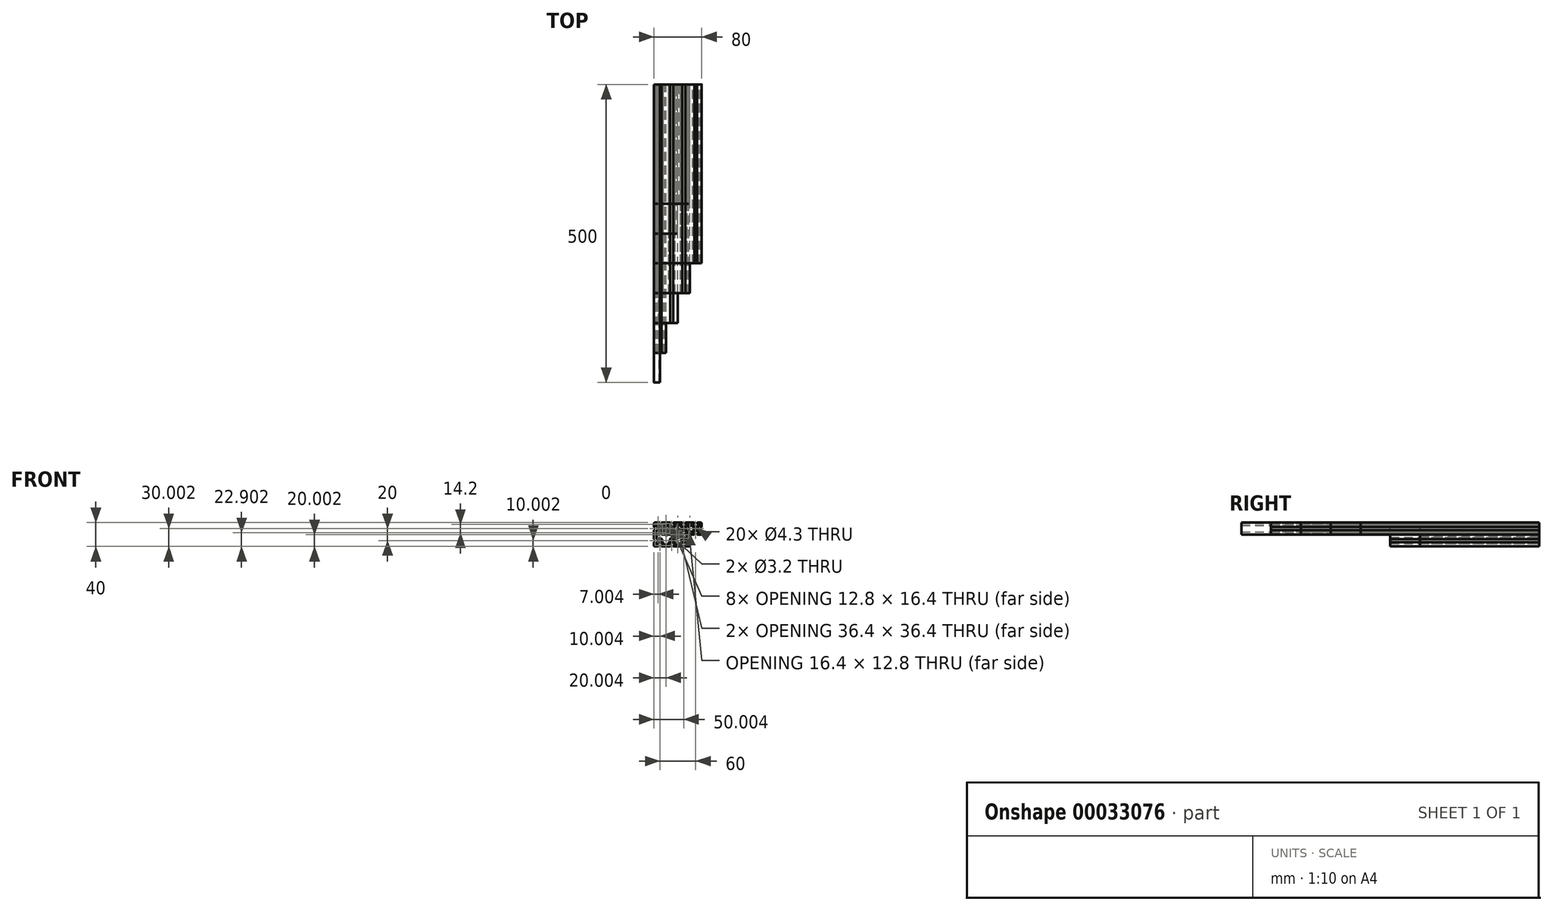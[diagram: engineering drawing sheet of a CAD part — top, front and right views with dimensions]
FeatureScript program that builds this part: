
annotation { "Feature Type Name" : "Feature", "Feature Type Description" : "" }
export const myFeature = defineFeature(function(context is Context, id is Id, definition is map)
    precondition{}
    {
        {
            var Q0;
            Q0=qCreatedBy(makeId("Front.planeOp"),FACE);
            var sketch = newSketch(context, id + "F0", { "sketchPlane" : qUnion([Q0])});
            skLineSegment(sketch, "E0.rect.bottom", {"start": v(-15.75, 9.71) * mm, "end": v(-10.29, 9.71) * mm});
            skLineSegment(sketch, "E0.rect.top", {"start": v(-17.22, -10.29) * mm, "end": v(-3.32, -10.29) * mm});
            skLineSegment(sketch, "E0.rect.left", {"start": v(-17.25, 8.21) * mm, "end": v(-17.25, 3.46) * mm});
            skLineSegment(sketch, "E0.rect.right", {"start": v(2.75, 8.21) * mm, "end": v(2.75, 3.46) * mm});
            skPoint(sketch, "E0.rect.middle", {"position": v(-7.25, -0.29) * mm});
            skCircle(sketch, "E1", {"center": v(-7.25, -0.29) * mm, "radius": 2.15 * mm});
            skPoint(sketch, "E2.visualSharp", {"position": v(-17.25, 9.71) * mm});
            skArc(sketch, "E2.filletArc", {"start": v(-15.75, 9.71) * mm, "mid": v(-16.82, 9.28) * mm, "end": v(-17.25, 8.21) * mm});
            skPoint(sketch, "E3.visualSharp", {"position": v(2.75, 9.71) * mm});
            skArc(sketch, "E3.filletArc", {"start": v(2.75, 8.21) * mm, "mid": v(2.3, 9.28) * mm, "end": v(1.25, 9.71) * mm});
            skPoint(sketch, "E4.visualSharp", {"position": v(2.75, -10.29) * mm});
            skArc(sketch, "E4.filletArc", {"start": v(1.25, -10.29) * mm, "mid": v(2.3, -9.85) * mm, "end": v(2.75, -8.79) * mm});
            skPoint(sketch, "E5.visualSharp", {"position": v(-17.25, -10.29) * mm});
            skArc(sketch, "E5.filletArc", {"start": v(-17.25, -7.29) * mm, "mid": v(-18.72, -8.8) * mm, "end": v(-17.22, -10.29) * mm});
            skLineSegment(sketch, "E6.rect.bottom", {"start": v(-15.7, 2.96) * mm, "end": v(-16.75, 2.96) * mm});
            skLineSegment(sketch, "E6.rect.top", {"start": v(-15.7, -2.04) * mm, "end": v(-16.75, -2.04) * mm});
            skLineSegment(sketch, "E6.rect.left", {"start": v(-10.85, 2.34) * mm, "end": v(-10.85, -2.4) * mm});
            skLineSegment(sketch, "E6.rect.right", {"start": v(-23.65, 2.96) * mm, "end": v(-23.65, -2.04) * mm});
            skPoint(sketch, "E6.rect.middle", {"position": v(-17.25, 0.46) * mm});
            skLineSegment(sketch, "E7.rect.bottom", {"start": v(-9.65, 16.11) * mm, "end": v(-4.65, 16.11) * mm});
            skLineSegment(sketch, "E7.rect.top", {"start": v(-9.24, 3.31) * mm, "end": v(-6.36, 3.31) * mm});
            skLineSegment(sketch, "E7.rect.left", {"start": v(-9.79, 9.21) * mm, "end": v(-9.79, 8.16) * mm});
            skLineSegment(sketch, "E7.rect.right", {"start": v(-4.65, 9.21) * mm, "end": v(-4.65, 8.16) * mm});
            skPoint(sketch, "E7.rect.middle", {"position": v(-7.25, 9.71) * mm});
            skLineSegment(sketch, "E8", {"start": v(-17.25, 9.71) * mm, "end": v(2.75, -10.29) * mm, "construction": true});
            skLineSegment(sketch, "E9", {"start": v(4.78, 7.91) * mm, "end": v(-4.79, 7.91) * mm, "construction": true});
            skLineSegment(sketch, "E10", {"start": v(-15.45, 13.5) * mm, "end": v(-15.45, -13.73) * mm, "construction": true});
            skLineSegment(sketch, "E11.0.MirrorCS", {"start": v(0.55, 2.96) * mm, "end": v(2.25, 2.96) * mm});
            skLineSegment(sketch, "E12.0.MirrorCS", {"start": v(0.94, -3.27) * mm, "end": v(2.34, -3.54) * mm});
            skLineSegment(sketch, "E13.0.MirrorCS", {"start": v(-2.06, 3.04) * mm, "end": v(-3.49, -1.5) * mm});
            skLineSegment(sketch, "E14.0.MirrorCS", {"start": v(-0.42, 17.7) * mm, "end": v(0.94, -9.51) * mm, "construction": true});
            skLineSegment(sketch, "E15.0.MirrorCS", {"start": v(-5.3, -9.79) * mm, "end": v(-5.3, -8.34) * mm});
            skLineSegment(sketch, "E16.0.MirrorCS", {"start": v(-3, -9.4) * mm, "end": v(-4.52, -8.14) * mm});
            skLineSegment(sketch, "E17.0.MirrorCS", {"start": v(-9.53, -2.76) * mm, "end": v(-5.93, -2.76) * mm});
            skLineSegment(sketch, "E18.0.MirrorCS", {"start": v(4.78, -8.09) * mm, "end": v(-18.65, -8.09) * mm, "construction": true});
            skLineSegment(sketch, "E19.0.MirrorCS", {"start": v(-6.64, -13.3) * mm, "end": v(-6.64, 14.98) * mm, "construction": true});
            skLineSegment(sketch, "E20", {"start": v(-10.3, 3.75) * mm, "end": v(-12.58, 6.04) * mm});
            skLineSegment(sketch, "E21", {"start": v(-11.3, 3.4) * mm, "end": v(-13.58, 5.69) * mm});
            skLineSegment(sketch, "E22", {"start": v(-10.85, -2.4) * mm, "end": v(-10.85, -7.57) * mm});
            skLineSegment(sketch, "E23", {"start": v(-11.03, -4.26) * mm, "end": v(-11.03, -6.99) * mm});
            skLineSegment(sketch, "E24", {"start": v(-4.87, -3.2) * mm, "end": v(-1.86, -6.2) * mm});
            skLineSegment(sketch, "E25", {"start": v(-3.12, -3) * mm, "end": v(-1.2, -4.92) * mm});
            skLineSegment(sketch, "E26", {"start": v(-2.13, 2.59) * mm, "end": v(-2.13, 7.9) * mm});
            skLineSegment(sketch, "E27", {"start": v(-4.86, 4.81) * mm, "end": v(-4.86, 6.81) * mm});
            skLineSegment(sketch, "E28", {"start": v(-4.4, 7.91) * mm, "end": v(-5.96, 7.91) * mm});
            skLineSegment(sketch, "E29", {"start": v(-10.04, 7.91) * mm, "end": v(-11.8, 7.91) * mm});
            skLineSegment(sketch, "E30", {"start": v(-15.45, 4.9) * mm, "end": v(-15.45, 3.21) * mm});
            skLineSegment(sketch, "E31", {"start": v(-15.45, -2.29) * mm, "end": v(-15.45, -4.67) * mm});
            skLineSegment(sketch, "E32", {"start": v(-9.93, -8.09) * mm, "end": v(-4.68, -8.09) * mm});
            skLineSegment(sketch, "E33", {"start": v(-5.06, -8.09) * mm, "end": v(-2.63, -8.09) * mm});
            skLineSegment(sketch, "E34", {"start": v(0.67, -4.09) * mm, "end": v(0.64, -3.53) * mm});
            skLineSegment(sketch, "E35", {"start": v(0.3, 3.2) * mm, "end": v(0.07, 7.96) * mm});
            skLineSegment(sketch, "E36.trimOffspring", {"start": v(-17.25, -2.54) * mm, "end": v(-17.25, -7.29) * mm});
            skLineSegment(sketch, "E37.trimOffspring", {"start": v(-4.15, 9.71) * mm, "end": v(1.25, 9.71) * mm});
            skLineSegment(sketch, "E38.trimOffspring", {"start": v(2.75, -4.04) * mm, "end": v(2.75, -8.79) * mm});
            skLineSegment(sketch, "E39.trimOffspring", {"start": v(-9.79, 7.91) * mm, "end": v(-18.65, 7.91) * mm, "construction": true});
            skLineSegment(sketch, "E40.trimOffspring", {"start": v(-4.8, -10.29) * mm, "end": v(1.25, -10.29) * mm});
            skPoint(sketch, "E41.0.MirrorCS.end.orphan", {"position": v(-5.3, -15.56) * mm});
            skPoint(sketch, "E41.0.MirrorCS.start.orphan", {"position": v(-2.3, -9.97) * mm});
            skPoint(sketch, "E42.visualSharp", {"position": v(-9.79, 9.71) * mm});
            skArc(sketch, "E42.filletArc", {"start": v(-9.79, 9.21) * mm, "mid": v(-9.93, 9.57) * mm, "end": v(-10.29, 9.71) * mm});
            skPoint(sketch, "E43.visualSharp", {"position": v(-4.65, 9.71) * mm});
            skArc(sketch, "E43.filletArc", {"start": v(-4.15, 9.71) * mm, "mid": v(-4.5, 9.57) * mm, "end": v(-4.65, 9.21) * mm});
            skPoint(sketch, "E44.visualSharp", {"position": v(2.75, 2.96) * mm});
            skArc(sketch, "E44.filletArc", {"start": v(2.25, 2.96) * mm, "mid": v(2.6, 3.11) * mm, "end": v(2.75, 3.46) * mm});
            skPoint(sketch, "E45.visualSharp", {"position": v(2.75, -3.62) * mm});
            skArc(sketch, "E45.filletArc", {"start": v(2.75, -4.04) * mm, "mid": v(2.63, -3.72) * mm, "end": v(2.34, -3.54) * mm});
            skPoint(sketch, "E46.visualSharp", {"position": v(-5.3, -10.29) * mm});
            skArc(sketch, "E46.filletArc", {"start": v(-5.3, -9.79) * mm, "mid": v(-5.16, -10.14) * mm, "end": v(-4.8, -10.29) * mm});
            skPoint(sketch, "E47.visualSharp", {"position": v(-1.93, -10.29) * mm});
            skArc(sketch, "E47.filletArc", {"start": v(-3.32, -10.29) * mm, "mid": v(-2.85, -9.95) * mm, "end": v(-3, -9.4) * mm});
            skPoint(sketch, "E48.visualSharp", {"position": v(-17.25, -2.04) * mm});
            skArc(sketch, "E48.filletArc", {"start": v(-16.75, -2.04) * mm, "mid": v(-17.1, -2.18) * mm, "end": v(-17.25, -2.54) * mm});
            skPoint(sketch, "E49.visualSharp", {"position": v(-17.25, 2.96) * mm});
            skArc(sketch, "E49.filletArc", {"start": v(-17.25, 3.46) * mm, "mid": v(-17.1, 3.11) * mm, "end": v(-16.75, 2.96) * mm});
            skPoint(sketch, "E50.visualSharp", {"position": v(-9.79, 7.91) * mm});
            skArc(sketch, "E50.filletArc", {"start": v(-10.04, 7.91) * mm, "mid": v(-9.86, 7.99) * mm, "end": v(-9.79, 8.16) * mm});
            skPoint(sketch, "E51.visualSharp", {"position": v(-4.79, 7.91) * mm});
            skArc(sketch, "E51.filletArc", {"start": v(-4.65, 8.16) * mm, "mid": v(-4.58, 7.99) * mm, "end": v(-4.4, 7.91) * mm});
            skPoint(sketch, "E52.visualSharp", {"position": v(0.32, 2.96) * mm});
            skArc(sketch, "E52.filletArc", {"start": v(0.3, 3.2) * mm, "mid": v(0.38, 3.03) * mm, "end": v(0.55, 2.96) * mm});
            skPoint(sketch, "E53.visualSharp", {"position": v(0.63, -3.21) * mm});
            skArc(sketch, "E53.filletArc", {"start": v(0.94, -3.27) * mm, "mid": v(0.73, -3.33) * mm, "end": v(0.64, -3.53) * mm});
            skPoint(sketch, "E54.visualSharp", {"position": v(-5.3, -8.09) * mm});
            skArc(sketch, "E54.filletArc", {"start": v(-5.06, -8.09) * mm, "mid": v(-5.24, -8.16) * mm, "end": v(-5.3, -8.34) * mm});
            skPoint(sketch, "E55.visualSharp", {"position": v(-4.59, -8.09) * mm});
            skArc(sketch, "E55.filletArc", {"start": v(-4.52, -8.14) * mm, "mid": v(-4.6, -8.1) * mm, "end": v(-4.68, -8.09) * mm});
            skPoint(sketch, "E56.visualSharp", {"position": v(-15.45, -2.04) * mm});
            skArc(sketch, "E56.filletArc", {"start": v(-15.45, -2.29) * mm, "mid": v(-15.53, -2.1) * mm, "end": v(-15.7, -2.04) * mm});
            skPoint(sketch, "E57.visualSharp", {"position": v(-15.45, 2.96) * mm});
            skArc(sketch, "E57.filletArc", {"start": v(-15.7, 2.96) * mm, "mid": v(-15.53, 3.04) * mm, "end": v(-15.45, 3.21) * mm});
            skPoint(sketch, "E58.visualSharp", {"position": v(-14.46, 7.91) * mm});
            skArc(sketch, "E58.filletArc", {"start": v(-11.8, 7.91) * mm, "mid": v(-12.82, 7.24) * mm, "end": v(-12.58, 6.04) * mm});
            skPoint(sketch, "E59.visualSharp", {"position": v(-4.86, 7.91) * mm});
            skArc(sketch, "E59.filletArc", {"start": v(-4.86, 6.81) * mm, "mid": v(-5.18, 7.6) * mm, "end": v(-5.96, 7.91) * mm});
            skPoint(sketch, "E60.visualSharp", {"position": v(-2.13, 51.68) * mm});
            skArc(sketch, "E60.filletArc", {"start": v(0.07, 7.96) * mm, "mid": v(-1.06, 9) * mm, "end": v(-2.13, 7.9) * mm});
            skPoint(sketch, "E61.visualSharp", {"position": v(0.81, -6.94) * mm});
            skArc(sketch, "E61.filletArc", {"start": v(-1.2, -4.92) * mm, "mid": v(0.02, -5.15) * mm, "end": v(0.67, -4.09) * mm});
            skPoint(sketch, "E62.visualSharp", {"position": v(0.02, -8.09) * mm});
            skArc(sketch, "E62.filletArc", {"start": v(-2.63, -8.09) * mm, "mid": v(-1.62, -7.4) * mm, "end": v(-1.86, -6.2) * mm});
            skPoint(sketch, "E63.visualSharp", {"position": v(-11.03, -8.09) * mm});
            skArc(sketch, "E63.filletArc", {"start": v(-11.03, -6.99) * mm, "mid": v(-10.7, -7.76) * mm, "end": v(-9.93, -8.09) * mm});
            skPoint(sketch, "E64.visualSharp", {"position": v(-15.45, -40569314724.49) * mm});
            skArc(sketch, "E64.filletArc", {"start": v(-15.45, -21166598987.53) * mm, "mid": v(-14.35, -21166598988.63) * mm, "end": v(-13.25, -21166598987.53) * mm});
            skPoint(sketch, "E65.visualSharp", {"position": v(-15.45, 7.56) * mm});
            skArc(sketch, "E65.filletArc", {"start": v(-13.58, 5.69) * mm, "mid": v(-14.78, 5.93) * mm, "end": v(-15.45, 4.9) * mm});
            skPoint(sketch, "E66.visualSharp", {"position": v(-9.86, 3.31) * mm});
            skArc(sketch, "E66.filletArc", {"start": v(-10.3, 3.75) * mm, "mid": v(-9.81, 3.43) * mm, "end": v(-9.24, 3.31) * mm});
            skPoint(sketch, "E67.visualSharp", {"position": v(-4.86, 3.31) * mm});
            skArc(sketch, "E67.filletArc", {"start": v(-6.36, 3.31) * mm, "mid": v(-5.3, 3.75) * mm, "end": v(-4.86, 4.81) * mm});
            skPoint(sketch, "E68.visualSharp", {"position": v(-2.09, 2.96) * mm});
            skArc(sketch, "E68.filletArc", {"start": v(-2.13, 2.59) * mm, "mid": v(0.85, 2.36) * mm, "end": v(-2.06, 3.04) * mm});
            skPoint(sketch, "E69.visualSharp", {"position": v(-3.76, -2.36) * mm});
            skArc(sketch, "E69.filletArc", {"start": v(-3.49, -1.5) * mm, "mid": v(-3.51, -2.3) * mm, "end": v(-3.12, -3) * mm});
            skPoint(sketch, "E70.visualSharp", {"position": v(-10.85, -2.04) * mm});
            skLineSegment(sketch, "E70.filletArc", {"start": v(-10.85, -2.4) * mm, "end": v(-10.85, -2.4) * mm});
            skPoint(sketch, "E71.visualSharp", {"position": v(-10.85, 2.96) * mm});
            skArc(sketch, "E71.filletArc", {"start": v(-10.85, 2.34) * mm, "mid": v(-10.97, 2.92) * mm, "end": v(-11.3, 3.4) * mm});
            skPoint(sketch, "E72.visualSharp", {"position": v(-11.03, -2.76) * mm});
            skArc(sketch, "E72.filletArc", {"start": v(-9.53, -2.76) * mm, "mid": v(-10.6, -3.2) * mm, "end": v(-11.03, -4.26) * mm});
            skPoint(sketch, "E73.visualSharp", {"position": v(-5.3, -2.76) * mm});
            skArc(sketch, "E73.filletArc", {"start": v(-4.87, -3.2) * mm, "mid": v(-5.36, -2.87) * mm, "end": v(-5.93, -2.76) * mm});
            skLineSegment(sketch, "E74", {"start": v(-15.75, 9.71) * mm, "end": v(-8.79, 9.71) * mm});
            skLineSegment(sketch, "E75.0.MirrorCS", {"start": v(-17.22, -10.29) * mm, "end": v(-8.79, -10.29) * mm});
            skLineSegment(sketch, "E76", {"start": v(-7.29, 8.21) * mm, "end": v(-7.29, -8.79) * mm});
            skPoint(sketch, "E77.visualSharp", {"position": v(-7.29, 9.71) * mm});
            skArc(sketch, "E77.filletArc", {"start": v(-7.29, 8.21) * mm, "mid": v(-7.73, 9.28) * mm, "end": v(-8.79, 9.71) * mm});
            skPoint(sketch, "E78.visualSharp", {"position": v(-7.29, -10.29) * mm});
            skArc(sketch, "E78.filletArc", {"start": v(-8.79, -10.29) * mm, "mid": v(-7.73, -9.85) * mm, "end": v(-7.29, -8.79) * mm});
            skLineSegment(sketch, "E79", {"start": v(-15.45, 7.56) * mm, "end": v(-2.13, 51.68) * mm, "construction": true});
            skLineSegment(sketch, "E80", {"start": v(-7.32, -20284657370.7) * mm, "end": v(0.81, -6.94) * mm, "construction": true});
            skLineSegment(sketch, "E81", {"start": v(-10.29, 9.21) * mm, "end": v(-3.32, -9.79) * mm, "construction": true});
            skCircle(sketch, "E82", {"center": v(-12.85, 16.2) * mm, "radius": 1.6 * mm});
            skCircle(sketch, "E83", {"center": v(0.81, -21.05) * mm, "radius": 1.6 * mm});
            skLineSegment(sketch, "E84", {"start": v(2.75, 9.71) * mm, "end": v(2.75, -10.29) * mm, "construction": true});
            skLineSegment(sketch, "E85.0.MirrorCS", {"start": v(9.64, 9.71) * mm, "end": v(4.25, 9.71) * mm});
            skArc(sketch, "E86.0.MirrorCS", {"start": v(9.64, 9.71) * mm, "mid": v(10, 9.57) * mm, "end": v(10.14, 9.21) * mm});
            skLineSegment(sketch, "E87.0.MirrorCS", {"start": v(10.14, 9.21) * mm, "end": v(10.14, 8.16) * mm});
            skArc(sketch, "E88.0.MirrorCS", {"start": v(10.14, 8.16) * mm, "mid": v(10.07, 7.99) * mm, "end": v(9.9, 7.91) * mm});
            skLineSegment(sketch, "E89.0.MirrorCS", {"start": v(9.9, 7.91) * mm, "end": v(11.45, 7.91) * mm});
            skArc(sketch, "E90.0.MirrorCS", {"start": v(10.35, 6.81) * mm, "mid": v(10.67, 7.6) * mm, "end": v(11.45, 7.91) * mm});
            skLineSegment(sketch, "E91.0.MirrorCS", {"start": v(10.35, 4.81) * mm, "end": v(10.35, 6.81) * mm});
            skArc(sketch, "E92.0.MirrorCS", {"start": v(11.85, 3.31) * mm, "mid": v(10.79, 3.75) * mm, "end": v(10.35, 4.81) * mm});
            skLineSegment(sketch, "E93.0.MirrorCS", {"start": v(14.73, 3.31) * mm, "end": v(11.85, 3.31) * mm});
            skArc(sketch, "E94.0.MirrorCS", {"start": v(15.79, 3.75) * mm, "mid": v(15.3, 3.43) * mm, "end": v(14.73, 3.31) * mm});
            skLineSegment(sketch, "E95.0.MirrorCS", {"start": v(15.79, 3.75) * mm, "end": v(18.07, 6.04) * mm});
            skArc(sketch, "E96.0.MirrorCS", {"start": v(17.3, 7.91) * mm, "mid": v(18.31, 7.24) * mm, "end": v(18.07, 6.04) * mm});
            skLineSegment(sketch, "E97.0.MirrorCS", {"start": v(15.53, 7.91) * mm, "end": v(17.3, 7.91) * mm});
            skArc(sketch, "E98.0.MirrorCS", {"start": v(15.53, 7.91) * mm, "mid": v(15.35, 7.99) * mm, "end": v(15.28, 8.16) * mm});
            skLineSegment(sketch, "E99.0.MirrorCS", {"start": v(15.28, 9.21) * mm, "end": v(15.28, 8.16) * mm});
            skArc(sketch, "E100.0.MirrorCS", {"start": v(15.28, 9.21) * mm, "mid": v(15.42, 9.57) * mm, "end": v(15.78, 9.71) * mm});
            skLineSegment(sketch, "E101.0.MirrorCS", {"start": v(21.25, 9.71) * mm, "end": v(15.78, 9.71) * mm});
            skArc(sketch, "E102.0.MirrorCS", {"start": v(21.25, 9.71) * mm, "mid": v(22.3, 9.28) * mm, "end": v(22.75, 8.21) * mm});
            skLineSegment(sketch, "E103.0.MirrorCS", {"start": v(22.75, 8.21) * mm, "end": v(22.75, 3.46) * mm});
            skArc(sketch, "E104.0.MirrorCS", {"start": v(22.75, 3.46) * mm, "mid": v(22.6, 3.11) * mm, "end": v(22.25, 2.96) * mm});
            skLineSegment(sketch, "E105.0.MirrorCS", {"start": v(21.2, 2.96) * mm, "end": v(22.25, 2.96) * mm});
            skArc(sketch, "E106.0.MirrorCS", {"start": v(21.2, 2.96) * mm, "mid": v(21.02, 3.04) * mm, "end": v(20.95, 3.21) * mm});
            skLineSegment(sketch, "E107.0.MirrorCS", {"start": v(20.95, 4.9) * mm, "end": v(20.95, 3.21) * mm});
            skArc(sketch, "E108.0.MirrorCS", {"start": v(19.07, 5.69) * mm, "mid": v(20.27, 5.93) * mm, "end": v(20.95, 4.9) * mm});
            skLineSegment(sketch, "E109.0.MirrorCS", {"start": v(16.78, 3.4) * mm, "end": v(19.07, 5.69) * mm});
            skArc(sketch, "E110.0.MirrorCS", {"start": v(16.35, 2.34) * mm, "mid": v(16.46, 2.92) * mm, "end": v(16.78, 3.4) * mm});
            skLineSegment(sketch, "E111.0.MirrorCS", {"start": v(16.35, 2.34) * mm, "end": v(16.35, -2.4) * mm});
            skLineSegment(sketch, "E112.0.MirrorCS", {"start": v(16.35, -2.4) * mm, "end": v(16.35, -2.4) * mm});
            skLineSegment(sketch, "E113.0.MirrorCS", {"start": v(16.35, -2.4) * mm, "end": v(16.35, -4.7) * mm});
            skArc(sketch, "E114.0.MirrorCS", {"start": v(20.95, -21166598987.53) * mm, "mid": v(19.85, -21166598988.63) * mm, "end": v(18.75, -21166598987.53) * mm});
            skLineSegment(sketch, "E115.0.MirrorCS", {"start": v(20.95, -2.29) * mm, "end": v(20.95, -4.67) * mm});
            skArc(sketch, "E116.0.MirrorCS", {"start": v(20.95, -2.29) * mm, "mid": v(21.02, -2.1) * mm, "end": v(21.2, -2.04) * mm});
            skLineSegment(sketch, "E117.0.MirrorCS", {"start": v(21.2, -2.04) * mm, "end": v(22.25, -2.04) * mm});
            skArc(sketch, "E118.0.MirrorCS", {"start": v(22.25, -2.04) * mm, "mid": v(22.6, -2.18) * mm, "end": v(22.75, -2.54) * mm});
            skLineSegment(sketch, "E119.0.MirrorCS", {"start": v(22.75, -2.54) * mm, "end": v(22.75, -7.29) * mm});
            skArc(sketch, "E120.0.MirrorCS", {"start": v(22.75, -7.29) * mm, "mid": v(24.2, -8.8) * mm, "end": v(22.7, -10.29) * mm});
            skLineSegment(sketch, "E121.0.MirrorCS", {"start": v(22.7, -10.29) * mm, "end": v(8.8, -10.29) * mm});
            skArc(sketch, "E122.0.MirrorCS", {"start": v(8.8, -10.29) * mm, "mid": v(8.34, -9.95) * mm, "end": v(8.49, -9.4) * mm});
            skLineSegment(sketch, "E123.0.MirrorCS", {"start": v(8.49, -9.4) * mm, "end": v(10, -8.14) * mm});
            skArc(sketch, "E124.0.MirrorCS", {"start": v(10, -8.14) * mm, "mid": v(10.08, -8.1) * mm, "end": v(10.17, -8.09) * mm});
            skLineSegment(sketch, "E125.0.MirrorCS", {"start": v(15.42, -8.09) * mm, "end": v(10.17, -8.09) * mm});
            skArc(sketch, "E126.0.MirrorCS", {"start": v(16.52, -6.99) * mm, "mid": v(16.2, -7.76) * mm, "end": v(15.42, -8.09) * mm});
            skLineSegment(sketch, "E127.0.MirrorCS", {"start": v(16.52, -4.26) * mm, "end": v(16.52, -6.99) * mm});
            skArc(sketch, "E128.0.MirrorCS", {"start": v(15.02, -2.76) * mm, "mid": v(16.08, -3.2) * mm, "end": v(16.52, -4.26) * mm});
            skLineSegment(sketch, "E129.0.MirrorCS", {"start": v(15.02, -2.76) * mm, "end": v(11.42, -2.76) * mm});
            skArc(sketch, "E130.0.MirrorCS", {"start": v(10.36, -3.2) * mm, "mid": v(10.85, -2.87) * mm, "end": v(11.42, -2.76) * mm});
            skLineSegment(sketch, "E131.0.MirrorCS", {"start": v(10.36, -3.2) * mm, "end": v(7.35, -6.2) * mm});
            skArc(sketch, "E132.0.MirrorCS", {"start": v(8.12, -8.09) * mm, "mid": v(7.1, -7.4) * mm, "end": v(7.35, -6.2) * mm});
            skLineSegment(sketch, "E133.0.MirrorCS", {"start": v(10.55, -8.09) * mm, "end": v(8.12, -8.09) * mm});
            skArc(sketch, "E134.0.MirrorCS", {"start": v(10.55, -8.09) * mm, "mid": v(10.73, -8.16) * mm, "end": v(10.8, -8.34) * mm});
            skLineSegment(sketch, "E135.0.MirrorCS", {"start": v(10.8, -9.79) * mm, "end": v(10.8, -8.34) * mm});
            skArc(sketch, "E136.0.MirrorCS", {"start": v(10.8, -9.79) * mm, "mid": v(10.65, -10.14) * mm, "end": v(10.3, -10.29) * mm});
            skLineSegment(sketch, "E137.0.MirrorCS", {"start": v(10.3, -10.29) * mm, "end": v(4.25, -10.29) * mm});
            skCircle(sketch, "E138.0.MirrorC", {"center": v(12.75, -0.29) * mm, "radius": 2.15 * mm});
            skLineSegment(sketch, "E139.0.MirrorCS", {"start": v(7.55, 3.04) * mm, "end": v(8.98, -1.5) * mm});
            skArc(sketch, "E140.0.MirrorCS", {"start": v(7.62, 2.59) * mm, "mid": v(4.64, 2.36) * mm, "end": v(7.55, 3.04) * mm});
            skArc(sketch, "E141.0.MirrorCS", {"start": v(8.98, -1.5) * mm, "mid": v(9, -2.3) * mm, "end": v(8.6, -3) * mm});
            skLineSegment(sketch, "E142.0.MirrorCS", {"start": v(8.6, -3) * mm, "end": v(6.7, -4.92) * mm});
            skLineSegment(sketch, "E143.0.MirrorCS", {"start": v(7.62, 2.59) * mm, "end": v(7.62, 7.9) * mm});
            skArc(sketch, "E144.0.MirrorCS", {"start": v(5.42, 7.96) * mm, "mid": v(6.55, 9) * mm, "end": v(7.62, 7.9) * mm});
            skArc(sketch, "E145.0.MirrorCS", {"start": v(6.7, -4.92) * mm, "mid": v(5.47, -5.15) * mm, "end": v(4.82, -4.09) * mm});
            skLineSegment(sketch, "E146.0.MirrorCS", {"start": v(5.91, 17.7) * mm, "end": v(4.55, -9.51) * mm, "construction": true});
            skLineSegment(sketch, "E147.0.MirrorCS", {"start": v(20.95, 13.5) * mm, "end": v(20.95, -13.73) * mm, "construction": true});
            skLineSegment(sketch, "E148.0.MirrorCS", {"start": v(0.71, -8.09) * mm, "end": v(24.14, -8.09) * mm, "construction": true});
            skLineSegment(sketch, "E149.0.MirrorCS", {"start": v(15.28, 7.91) * mm, "end": v(24.14, 7.91) * mm, "construction": true});
            skLineSegment(sketch, "E150.0.MirrorCS", {"start": v(0.71, 7.91) * mm, "end": v(10.28, 7.91) * mm, "construction": true});
            skPoint(sketch, "E151.orphan", {"position": v(14.28, 9.71) * mm});
            skPoint(sketch, "E152.orphan", {"position": v(14.28, -10.29) * mm});
            skLineSegment(sketch, "E153", {"start": v(4.25, 9.71) * mm, "end": v(1.25, 9.71) * mm});
            skLineSegment(sketch, "E154", {"start": v(4.25, -10.29) * mm, "end": v(1.25, -10.29) * mm});
            skLineSegment(sketch, "E155", {"start": v(-2.13, 6.41) * mm, "end": v(-2.13, 7.9) * mm});
            skLineSegment(sketch, "E156", {"start": v(7.62, 6.41) * mm, "end": v(7.62, 7.9) * mm});
            skLineSegment(sketch, "E157", {"start": v(6.12, 7.91) * mm, "end": v(-0.63, 7.91) * mm});
            skLineSegment(sketch, "E158", {"start": v(-1.2, -4.92) * mm, "end": v(1.52, -7.65) * mm});
            skLineSegment(sketch, "E159", {"start": v(6.7, -4.92) * mm, "end": v(3.97, -7.65) * mm});
            skLineSegment(sketch, "E160", {"start": v(2.9, -8.09) * mm, "end": v(2.58, -8.09) * mm});
            skPoint(sketch, "E161.visualSharp", {"position": v(-2.13, 7.91) * mm});
            skArc(sketch, "E161.filletArc", {"start": v(-0.63, 7.91) * mm, "mid": v(-1.7, 7.48) * mm, "end": v(-2.13, 6.41) * mm});
            skPoint(sketch, "E162.visualSharp", {"position": v(7.62, 7.91) * mm});
            skArc(sketch, "E162.filletArc", {"start": v(7.62, 6.41) * mm, "mid": v(7.18, 7.48) * mm, "end": v(6.12, 7.91) * mm});
            skPoint(sketch, "E163.visualSharp", {"position": v(3.53, -8.09) * mm});
            skArc(sketch, "E163.filletArc", {"start": v(2.9, -8.09) * mm, "mid": v(3.48, -7.97) * mm, "end": v(3.97, -7.65) * mm});
            skPoint(sketch, "E164.visualSharp", {"position": v(1.96, -8.09) * mm});
            skArc(sketch, "E164.filletArc", {"start": v(1.52, -7.65) * mm, "mid": v(2, -7.97) * mm, "end": v(2.58, -8.09) * mm});
            skSolve(sketch);
        }
        {
            var Q0;
            Q0=qCreatedBy(makeId("Front.planeOp"),FACE);
            var sketch = newSketch(context, id + "F1", { "sketchPlane" : qUnion([Q0])});
            skLineSegment(sketch, "E165.0", {"start": v(-17.29, 8.5) * mm, "end": v(-17.29, 3) * mm});
            skArc(sketch, "E166.0", {"start": v(-15.79, 10) * mm, "mid": v(-16.85, 9.56) * mm, "end": v(-17.29, 8.5) * mm});
            skArc(sketch, "E167.0", {"start": v(-7.29, 8.5) * mm, "mid": v(-7.73, 9.56) * mm, "end": v(-8.79, 10) * mm});
            skLineSegment(sketch, "E168.0", {"start": v(-7.29, 8.5) * mm, "end": v(-7.29, -8.5) * mm});
            skArc(sketch, "E169.0", {"start": v(-8.79, -10) * mm, "mid": v(-7.73, -9.56) * mm, "end": v(-7.29, -8.5) * mm});
            skArc(sketch, "E170.0", {"start": v(-17.29, -8.5) * mm, "mid": v(-16.85, -9.56) * mm, "end": v(-15.79, -10) * mm});
            skLineSegment(sketch, "E171.0", {"start": v(-17.29, -3) * mm, "end": v(-17.29, -8.5) * mm});
            skArc(sketch, "E172.0", {"start": v(-17.29, 3) * mm, "mid": v(-17.14, 2.65) * mm, "end": v(-16.79, 2.5) * mm});
            skArc(sketch, "E173.0", {"start": v(-16.79, -2.5) * mm, "mid": v(-17.14, -2.64) * mm, "end": v(-17.29, -3) * mm});
            skLineSegment(sketch, "E174.0", {"start": v(-15.74, -2.5) * mm, "end": v(-16.79, -2.5) * mm});
            skLineSegment(sketch, "E175.0", {"start": v(-15.74, 2.5) * mm, "end": v(-16.79, 2.5) * mm});
            skArc(sketch, "E176.0", {"start": v(-15.74, 2.5) * mm, "mid": v(-15.56, 2.58) * mm, "end": v(-15.49, 2.75) * mm});
            skArc(sketch, "E177.0", {"start": v(-15.49, -2.75) * mm, "mid": v(-15.56, -2.57) * mm, "end": v(-15.74, -2.5) * mm});
            skLineSegment(sketch, "E178.0", {"start": v(-15.49, -2.75) * mm, "end": v(-15.49, -4.44) * mm});
            skLineSegment(sketch, "E179.0", {"start": v(-15.49, 4.45) * mm, "end": v(-15.49, 2.75) * mm});
            skArc(sketch, "E180.0", {"start": v(-13.6, 5.22) * mm, "mid": v(-14.8, 5.46) * mm, "end": v(-15.49, 4.45) * mm});
            skLineSegment(sketch, "E181.0", {"start": v(-11.33, 2.94) * mm, "end": v(-13.6, 5.22) * mm});
            skArc(sketch, "E182.0", {"start": v(-10.89, 1.88) * mm, "mid": v(-11, 2.45) * mm, "end": v(-11.33, 2.94) * mm});
            skLineSegment(sketch, "E183.0", {"start": v(-10.89, 1.88) * mm, "end": v(-10.89, -1.88) * mm});
            skArc(sketch, "E184.0", {"start": v(-11.33, -2.94) * mm, "mid": v(-11, -2.45) * mm, "end": v(-10.89, -1.88) * mm});
            skLineSegment(sketch, "E185.0", {"start": v(-11.33, -2.94) * mm, "end": v(-13.6, -5.22) * mm});
            skArc(sketch, "E186.0", {"start": v(-15.49, -4.44) * mm, "mid": v(-14.8, -5.46) * mm, "end": v(-13.6, -5.22) * mm});
            skCircle(sketch, "E187.0", {"center": v(-10.29, -7.1) * mm, "radius": 1.6 * mm});
            skCircle(sketch, "E188.0", {"center": v(-10.29, 7.1) * mm, "radius": 1.6 * mm});
            skLineSegment(sketch, "E189", {"start": v(-15.79, 10) * mm, "end": v(-8.79, 10) * mm});
            skLineSegment(sketch, "E190", {"start": v(-15.79, -10) * mm, "end": v(-8.79, -10) * mm});
            skSolve(sketch);
        }
        {
            var Q0;
            Q0=qCreatedBy(makeId("Front.planeOp"),FACE);
            var sketch = newSketch(context, id + "F2", { "sketchPlane" : qUnion([Q0])});
            skArc(sketch, "E191.0", {"start": v(-15.79, 10) * mm, "mid": v(-16.85, 9.56) * mm, "end": v(-17.29, 8.5) * mm});
            skLineSegment(sketch, "E192.0", {"start": v(-17.29, 8.5) * mm, "end": v(-17.29, 3) * mm});
            skArc(sketch, "E193.0", {"start": v(-9.79, 9.5) * mm, "mid": v(-9.93, 9.86) * mm, "end": v(-10.29, 10) * mm});
            skLineSegment(sketch, "E194.0", {"start": v(-9.79, 9.5) * mm, "end": v(-9.79, 8.45) * mm});
            skLineSegment(sketch, "E195.0", {"start": v(-10.04, 8.2) * mm, "end": v(-11.73, 8.2) * mm});
            skArc(sketch, "E196.0", {"start": v(-11.73, 8.2) * mm, "mid": v(-12.75, 7.52) * mm, "end": v(-12.5, 6.32) * mm});
            skLineSegment(sketch, "E197.0", {"start": v(-10.23, 4.04) * mm, "end": v(-12.5, 6.32) * mm});
            skArc(sketch, "E198.0", {"start": v(-10.23, 4.04) * mm, "mid": v(-9.74, 3.72) * mm, "end": v(-9.16, 3.6) * mm});
            skLineSegment(sketch, "E199.0", {"start": v(-9.16, 3.6) * mm, "end": v(-5.4, 3.6) * mm});
            skArc(sketch, "E200.0", {"start": v(-5.4, 3.6) * mm, "mid": v(-4.83, 3.72) * mm, "end": v(-4.35, 4.04) * mm});
            skLineSegment(sketch, "E201.0", {"start": v(-4.35, 4.04) * mm, "end": v(-2.06, 6.32) * mm});
            skArc(sketch, "E202.0", {"start": v(-2.06, 6.32) * mm, "mid": v(-1.83, 7.52) * mm, "end": v(-2.84, 8.2) * mm});
            skLineSegment(sketch, "E203.0", {"start": v(-2.84, 8.2) * mm, "end": v(-4.54, 8.2) * mm});
            skArc(sketch, "E204.0", {"start": v(-4.29, 10) * mm, "mid": v(-4.64, 9.86) * mm, "end": v(-4.79, 9.5) * mm});
            skLineSegment(sketch, "E205.0", {"start": v(-4.29, 10) * mm, "end": v(1.21, 10) * mm});
            skArc(sketch, "E206.0", {"start": v(2.71, 8.5) * mm, "mid": v(2.27, 9.56) * mm, "end": v(1.21, 10) * mm});
            skLineSegment(sketch, "E207.0", {"start": v(2.71, 8.5) * mm, "end": v(2.71, 3) * mm});
            skArc(sketch, "E208.0", {"start": v(2.21, 2.5) * mm, "mid": v(2.57, 2.65) * mm, "end": v(2.71, 3) * mm});
            skLineSegment(sketch, "E209.0", {"start": v(1.16, 2.5) * mm, "end": v(2.21, 2.5) * mm});
            skLineSegment(sketch, "E210.0", {"start": v(-15.79, 10) * mm, "end": v(-10.29, 10) * mm});
            skArc(sketch, "E211.0", {"start": v(-17.29, 3) * mm, "mid": v(-17.14, 2.65) * mm, "end": v(-16.79, 2.5) * mm});
            skLineSegment(sketch, "E212.0", {"start": v(-15.74, 2.5) * mm, "end": v(-16.79, 2.5) * mm});
            skArc(sketch, "E213.0", {"start": v(-15.74, 2.5) * mm, "mid": v(-15.56, 2.58) * mm, "end": v(-15.49, 2.75) * mm});
            skLineSegment(sketch, "E213.1", {"start": v(-15.49, 4.45) * mm, "end": v(-15.49, 2.75) * mm});
            skArc(sketch, "E213.2", {"start": v(-13.6, 5.22) * mm, "mid": v(-14.8, 5.46) * mm, "end": v(-15.49, 4.45) * mm});
            skLineSegment(sketch, "E214.0", {"start": v(-11.33, 2.94) * mm, "end": v(-13.6, 5.22) * mm});
            skArc(sketch, "E215.0", {"start": v(-10.89, 1.88) * mm, "mid": v(-11, 2.45) * mm, "end": v(-11.33, 2.94) * mm});
            skLineSegment(sketch, "E216.0", {"start": v(-10.89, 1.88) * mm, "end": v(-10.89, -1.88) * mm});
            skArc(sketch, "E217.0", {"start": v(-11.33, -2.94) * mm, "mid": v(-11, -2.45) * mm, "end": v(-10.89, -1.88) * mm});
            skLineSegment(sketch, "E218.0", {"start": v(-11.33, -2.94) * mm, "end": v(-13.6, -5.22) * mm});
            skArc(sketch, "E219.0", {"start": v(-15.49, -4.44) * mm, "mid": v(-14.8, -5.46) * mm, "end": v(-13.6, -5.22) * mm});
            skLineSegment(sketch, "E220.0", {"start": v(-15.49, -2.75) * mm, "end": v(-15.49, -4.44) * mm});
            skArc(sketch, "E221.0", {"start": v(-15.49, -2.75) * mm, "mid": v(-15.56, -2.57) * mm, "end": v(-15.74, -2.5) * mm});
            skLineSegment(sketch, "E222.0", {"start": v(-15.74, -2.5) * mm, "end": v(-16.79, -2.5) * mm});
            skArc(sketch, "E223.0", {"start": v(-16.79, -2.5) * mm, "mid": v(-17.14, -2.64) * mm, "end": v(-17.29, -3) * mm});
            skLineSegment(sketch, "E224.0", {"start": v(-17.29, -3) * mm, "end": v(-17.29, -8.5) * mm});
            skArc(sketch, "E225.0", {"start": v(-17.29, -8.5) * mm, "mid": v(-16.85, -9.56) * mm, "end": v(-15.79, -10) * mm});
            skLineSegment(sketch, "E226.0", {"start": v(-15.79, -10) * mm, "end": v(-10.29, -10) * mm});
            skArc(sketch, "E227.0", {"start": v(-10.29, -10) * mm, "mid": v(-9.93, -9.85) * mm, "end": v(-9.79, -9.5) * mm});
            skLineSegment(sketch, "E228.0", {"start": v(-9.79, -9.5) * mm, "end": v(-9.79, -8.45) * mm});
            skArc(sketch, "E229.0", {"start": v(-9.79, -8.45) * mm, "mid": v(-9.86, -8.27) * mm, "end": v(-10.04, -8.2) * mm});
            skLineSegment(sketch, "E230.0", {"start": v(-11.73, -8.2) * mm, "end": v(-10.04, -8.2) * mm});
            skArc(sketch, "E231.0", {"start": v(-12.5, -6.32) * mm, "mid": v(-12.75, -7.52) * mm, "end": v(-11.73, -8.2) * mm});
            skLineSegment(sketch, "E232.0", {"start": v(-10.23, -4.04) * mm, "end": v(-12.5, -6.32) * mm});
            skArc(sketch, "E233.0", {"start": v(-9.16, -3.6) * mm, "mid": v(-9.74, -3.71) * mm, "end": v(-10.23, -4.04) * mm});
            skLineSegment(sketch, "E234.0", {"start": v(-9.16, -3.6) * mm, "end": v(-5.4, -3.6) * mm});
            skArc(sketch, "E235.0", {"start": v(-4.35, -4.04) * mm, "mid": v(-4.83, -3.71) * mm, "end": v(-5.4, -3.6) * mm});
            skLineSegment(sketch, "E236.0", {"start": v(-4.35, -4.04) * mm, "end": v(-2.06, -6.32) * mm});
            skArc(sketch, "E237.0", {"start": v(-2.84, -8.2) * mm, "mid": v(-1.83, -7.52) * mm, "end": v(-2.06, -6.32) * mm});
            skLineSegment(sketch, "E238.0", {"start": v(-4.54, -8.2) * mm, "end": v(-2.84, -8.2) * mm});
            skArc(sketch, "E239.0", {"start": v(-4.54, -8.2) * mm, "mid": v(-4.71, -8.27) * mm, "end": v(-4.79, -8.45) * mm});
            skLineSegment(sketch, "E240.0", {"start": v(-4.79, -9.5) * mm, "end": v(-4.79, -8.45) * mm});
            skArc(sketch, "E241.0", {"start": v(-4.79, -9.5) * mm, "mid": v(-4.64, -9.85) * mm, "end": v(-4.29, -10) * mm});
            skLineSegment(sketch, "E242.0", {"start": v(-4.29, -10) * mm, "end": v(1.21, -10) * mm});
            skArc(sketch, "E243.0", {"start": v(1.21, -10) * mm, "mid": v(2.27, -9.56) * mm, "end": v(2.71, -8.5) * mm});
            skLineSegment(sketch, "E244.0", {"start": v(2.71, -3) * mm, "end": v(2.71, -8.5) * mm});
            skArc(sketch, "E245.0", {"start": v(2.71, -3) * mm, "mid": v(2.57, -2.64) * mm, "end": v(2.21, -2.5) * mm});
            skLineSegment(sketch, "E246.0", {"start": v(1.16, -2.5) * mm, "end": v(2.21, -2.5) * mm});
            skArc(sketch, "E247.0", {"start": v(1.16, -2.5) * mm, "mid": v(0.99, -2.57) * mm, "end": v(0.91, -2.75) * mm});
            skLineSegment(sketch, "E248.0", {"start": v(0.91, -4.44) * mm, "end": v(0.91, -2.75) * mm});
            skArc(sketch, "E249.0", {"start": v(-0.96, -5.22) * mm, "mid": v(0.23, -5.46) * mm, "end": v(0.91, -4.44) * mm});
            skLineSegment(sketch, "E250.0", {"start": v(-3.25, -2.94) * mm, "end": v(-0.96, -5.22) * mm});
            skArc(sketch, "E251.0", {"start": v(-3.69, -1.88) * mm, "mid": v(-3.57, -2.45) * mm, "end": v(-3.25, -2.94) * mm});
            skLineSegment(sketch, "E252.0", {"start": v(-3.69, 1.88) * mm, "end": v(-3.69, -1.88) * mm});
            skArc(sketch, "E253.0", {"start": v(-3.25, 2.94) * mm, "mid": v(-3.57, 2.45) * mm, "end": v(-3.69, 1.88) * mm});
            skLineSegment(sketch, "E254.0", {"start": v(-3.25, 2.94) * mm, "end": v(-0.96, 5.22) * mm});
            skArc(sketch, "E255.0", {"start": v(0.91, 4.45) * mm, "mid": v(0.23, 5.46) * mm, "end": v(-0.96, 5.22) * mm});
            skLineSegment(sketch, "E256.0", {"start": v(0.91, 2.75) * mm, "end": v(0.91, 4.45) * mm});
            skArc(sketch, "E257.0", {"start": v(0.91, 2.75) * mm, "mid": v(0.99, 2.58) * mm, "end": v(1.16, 2.5) * mm});
            skLineSegment(sketch, "E258.0", {"start": v(-4.79, 9.5) * mm, "end": v(-4.79, 8.45) * mm});
            skArc(sketch, "E259.0", {"start": v(-4.79, 8.45) * mm, "mid": v(-4.71, 8.28) * mm, "end": v(-4.54, 8.2) * mm});
            skArc(sketch, "E260.0", {"start": v(-10.04, 8.2) * mm, "mid": v(-9.86, 8.28) * mm, "end": v(-9.79, 8.45) * mm});
            skCircle(sketch, "E261.0", {"center": v(-7.29, 0) * mm, "radius": 2.15 * mm});
            skSolve(sketch);
        }
        {
            var Q0;
            Q0=qCreatedBy(makeId("Front.planeOp"),FACE);
            var sketch = newSketch(context, id + "F3", { "sketchPlane" : qUnion([Q0])});
            skArc(sketch, "E262.0", {"start": v(-15.79, 10) * mm, "mid": v(-16.85, 9.56) * mm, "end": v(-17.29, 8.5) * mm});
            skLineSegment(sketch, "E263.0", {"start": v(-15.79, 10) * mm, "end": v(-10.29, 10) * mm});
            skArc(sketch, "E264.0", {"start": v(-9.79, 9.5) * mm, "mid": v(-9.93, 9.86) * mm, "end": v(-10.29, 10) * mm});
            skLineSegment(sketch, "E265.0", {"start": v(-9.79, 9.5) * mm, "end": v(-9.79, 8.45) * mm});
            skArc(sketch, "E266.0", {"start": v(-10.04, 8.2) * mm, "mid": v(-9.86, 8.28) * mm, "end": v(-9.79, 8.45) * mm});
            skLineSegment(sketch, "E267.0", {"start": v(-10.04, 8.2) * mm, "end": v(-11.73, 8.2) * mm});
            skArc(sketch, "E268.0", {"start": v(-11.73, 8.2) * mm, "mid": v(-12.75, 7.52) * mm, "end": v(-12.5, 6.32) * mm});
            skLineSegment(sketch, "E269.0", {"start": v(-10.23, 4.04) * mm, "end": v(-12.5, 6.32) * mm});
            skArc(sketch, "E270.0", {"start": v(-10.23, 4.04) * mm, "mid": v(-9.74, 3.72) * mm, "end": v(-9.16, 3.6) * mm});
            skLineSegment(sketch, "E271.0", {"start": v(-9.16, 3.6) * mm, "end": v(-5.4, 3.6) * mm});
            skArc(sketch, "E272.0", {"start": v(-5.4, 3.6) * mm, "mid": v(-4.83, 3.72) * mm, "end": v(-4.35, 4.04) * mm});
            skLineSegment(sketch, "E273.0", {"start": v(-4.35, 4.04) * mm, "end": v(-2.06, 6.32) * mm});
            skArc(sketch, "E274.0", {"start": v(-2.06, 6.32) * mm, "mid": v(-1.83, 7.52) * mm, "end": v(-2.84, 8.2) * mm});
            skLineSegment(sketch, "E275.0", {"start": v(-2.84, 8.2) * mm, "end": v(-4.54, 8.2) * mm});
            skArc(sketch, "E276.0", {"start": v(-4.79, 8.45) * mm, "mid": v(-4.71, 8.28) * mm, "end": v(-4.54, 8.2) * mm});
            skLineSegment(sketch, "E277.0", {"start": v(-4.79, 9.5) * mm, "end": v(-4.79, 8.45) * mm});
            skArc(sketch, "E278.0", {"start": v(-4.29, 10) * mm, "mid": v(-4.64, 9.86) * mm, "end": v(-4.79, 9.5) * mm});
            skLineSegment(sketch, "E279.0", {"start": v(-17.29, 8.5) * mm, "end": v(-17.29, 3) * mm});
            skArc(sketch, "E280.0", {"start": v(-17.29, 3) * mm, "mid": v(-17.14, 2.65) * mm, "end": v(-16.79, 2.5) * mm});
            skLineSegment(sketch, "E281.0", {"start": v(-15.74, 2.5) * mm, "end": v(-16.79, 2.5) * mm});
            skArc(sketch, "E282.0", {"start": v(-15.74, 2.5) * mm, "mid": v(-15.56, 2.58) * mm, "end": v(-15.49, 2.75) * mm});
            skLineSegment(sketch, "E283.0", {"start": v(-15.49, 4.45) * mm, "end": v(-15.49, 2.75) * mm});
            skArc(sketch, "E284.0", {"start": v(-13.6, 5.22) * mm, "mid": v(-14.8, 5.46) * mm, "end": v(-15.49, 4.45) * mm});
            skLineSegment(sketch, "E285.0", {"start": v(-11.33, 2.94) * mm, "end": v(-13.6, 5.22) * mm});
            skArc(sketch, "E286.0", {"start": v(-10.89, 1.88) * mm, "mid": v(-11, 2.45) * mm, "end": v(-11.33, 2.94) * mm});
            skLineSegment(sketch, "E287.0", {"start": v(-10.89, 1.88) * mm, "end": v(-10.89, -1.88) * mm});
            skArc(sketch, "E288.0", {"start": v(-11.33, -2.94) * mm, "mid": v(-11, -2.45) * mm, "end": v(-10.89, -1.88) * mm});
            skLineSegment(sketch, "E289.0", {"start": v(-11.33, -2.94) * mm, "end": v(-13.6, -5.22) * mm});
            skArc(sketch, "E290.0", {"start": v(-15.49, -4.44) * mm, "mid": v(-14.8, -5.46) * mm, "end": v(-13.6, -5.22) * mm});
            skLineSegment(sketch, "E291.0", {"start": v(-15.49, -2.75) * mm, "end": v(-15.49, -4.44) * mm});
            skArc(sketch, "E292.0", {"start": v(-15.49, -2.75) * mm, "mid": v(-15.56, -2.57) * mm, "end": v(-15.74, -2.5) * mm});
            skLineSegment(sketch, "E293.0", {"start": v(-15.74, -2.5) * mm, "end": v(-16.79, -2.5) * mm});
            skArc(sketch, "E294.0", {"start": v(-16.79, -2.5) * mm, "mid": v(-17.14, -2.64) * mm, "end": v(-17.29, -3) * mm});
            skLineSegment(sketch, "E295.0", {"start": v(-17.29, -3) * mm, "end": v(-17.29, -8.5) * mm});
            skArc(sketch, "E296.0", {"start": v(-17.29, -8.5) * mm, "mid": v(-16.85, -9.56) * mm, "end": v(-15.79, -10) * mm});
            skLineSegment(sketch, "E297.0", {"start": v(-15.79, -10) * mm, "end": v(-10.29, -10) * mm});
            skArc(sketch, "E298.0", {"start": v(-10.29, -10) * mm, "mid": v(-9.93, -9.85) * mm, "end": v(-9.79, -9.5) * mm});
            skLineSegment(sketch, "E299.0", {"start": v(-9.79, -9.5) * mm, "end": v(-9.79, -8.45) * mm});
            skArc(sketch, "E300.0", {"start": v(-9.79, -8.45) * mm, "mid": v(-9.86, -8.27) * mm, "end": v(-10.04, -8.2) * mm});
            skLineSegment(sketch, "E301.0", {"start": v(-11.73, -8.2) * mm, "end": v(-10.04, -8.2) * mm});
            skArc(sketch, "E302.0", {"start": v(-12.5, -6.32) * mm, "mid": v(-12.75, -7.52) * mm, "end": v(-11.73, -8.2) * mm});
            skLineSegment(sketch, "E303.0", {"start": v(-10.23, -4.04) * mm, "end": v(-12.5, -6.32) * mm});
            skArc(sketch, "E304.0", {"start": v(-9.16, -3.6) * mm, "mid": v(-9.74, -3.71) * mm, "end": v(-10.23, -4.04) * mm});
            skLineSegment(sketch, "E305.0", {"start": v(-9.16, -3.6) * mm, "end": v(-5.4, -3.6) * mm});
            skArc(sketch, "E306.0", {"start": v(-4.35, -4.04) * mm, "mid": v(-4.83, -3.71) * mm, "end": v(-5.4, -3.6) * mm});
            skCircle(sketch, "E307.0", {"center": v(-7.29, 0) * mm, "radius": 2.15 * mm});
            skLineSegment(sketch, "E308.0", {"start": v(-4.35, -4.04) * mm, "end": v(-2.06, -6.32) * mm});
            skArc(sketch, "E309.0", {"start": v(-2.84, -8.2) * mm, "mid": v(-1.83, -7.52) * mm, "end": v(-2.06, -6.32) * mm});
            skLineSegment(sketch, "E310.0", {"start": v(-4.54, -8.2) * mm, "end": v(-2.84, -8.2) * mm});
            skArc(sketch, "E311.0", {"start": v(-4.54, -8.2) * mm, "mid": v(-4.71, -8.27) * mm, "end": v(-4.79, -8.45) * mm});
            skLineSegment(sketch, "E312.0", {"start": v(-4.79, -9.5) * mm, "end": v(-4.79, -8.45) * mm});
            skArc(sketch, "E313.0", {"start": v(-4.79, -9.5) * mm, "mid": v(-4.64, -9.85) * mm, "end": v(-4.29, -10) * mm});
            skArc(sketch, "E314.0", {"start": v(-3.25, 2.94) * mm, "mid": v(-3.57, 2.45) * mm, "end": v(-3.69, 1.88) * mm});
            skLineSegment(sketch, "E315.0", {"start": v(-3.69, 1.88) * mm, "end": v(-3.69, -1.88) * mm});
            skArc(sketch, "E316.0", {"start": v(-3.69, -1.88) * mm, "mid": v(-3.57, -2.45) * mm, "end": v(-3.25, -2.94) * mm});
            skArc(sketch, "E317.0", {"start": v(2.64, 8.2) * mm, "mid": v(2.06, 8.09) * mm, "end": v(1.57, 7.76) * mm});
            skArc(sketch, "E318.0", {"start": v(3.85, 7.76) * mm, "mid": v(3.37, 8.09) * mm, "end": v(2.8, 8.2) * mm});
            skArc(sketch, "E319.0", {"start": v(8.67, 2.94) * mm, "mid": v(9, 2.45) * mm, "end": v(9.11, 1.88) * mm});
            skLineSegment(sketch, "E320.0", {"start": v(9.11, 1.88) * mm, "end": v(9.11, -1.88) * mm});
            skArc(sketch, "E321.0", {"start": v(9.11, -1.88) * mm, "mid": v(9, -2.45) * mm, "end": v(8.67, -2.94) * mm});
            skArc(sketch, "E322.0", {"start": v(1.57, -7.76) * mm, "mid": v(2.06, -8.08) * mm, "end": v(2.64, -8.2) * mm});
            skArc(sketch, "E323.0", {"start": v(2.8, -8.2) * mm, "mid": v(3.37, -8.08) * mm, "end": v(3.85, -7.76) * mm});
            skLineSegment(sketch, "E324.0", {"start": v(2.8, -8.2) * mm, "end": v(2.64, -8.2) * mm});
            skLineSegment(sketch, "E325.0", {"start": v(2.8, 8.2) * mm, "end": v(2.64, 8.2) * mm});
            skArc(sketch, "E326.0", {"start": v(9.71, 10) * mm, "mid": v(10.07, 9.86) * mm, "end": v(10.21, 9.5) * mm});
            skLineSegment(sketch, "E327.0", {"start": v(10.21, 9.5) * mm, "end": v(10.21, 8.45) * mm});
            skArc(sketch, "E328.0", {"start": v(10.21, 8.45) * mm, "mid": v(10.14, 8.28) * mm, "end": v(9.96, 8.2) * mm});
            skLineSegment(sketch, "E329.0", {"start": v(8.27, 8.2) * mm, "end": v(9.96, 8.2) * mm});
            skArc(sketch, "E330.0", {"start": v(7.5, 6.32) * mm, "mid": v(7.25, 7.52) * mm, "end": v(8.27, 8.2) * mm});
            skLineSegment(sketch, "E331.0", {"start": v(9.77, 4.04) * mm, "end": v(7.5, 6.32) * mm});
            skArc(sketch, "E332.0", {"start": v(10.84, 3.6) * mm, "mid": v(10.26, 3.72) * mm, "end": v(9.77, 4.04) * mm});
            skLineSegment(sketch, "E333.0", {"start": v(14.6, 3.6) * mm, "end": v(10.84, 3.6) * mm});
            skArc(sketch, "E334.0", {"start": v(15.65, 4.04) * mm, "mid": v(15.17, 3.72) * mm, "end": v(14.6, 3.6) * mm});
            skLineSegment(sketch, "E335.0", {"start": v(15.65, 4.04) * mm, "end": v(17.94, 6.32) * mm});
            skArc(sketch, "E336.0", {"start": v(17.16, 8.2) * mm, "mid": v(18.17, 7.52) * mm, "end": v(17.94, 6.32) * mm});
            skLineSegment(sketch, "E337.0", {"start": v(15.46, 8.2) * mm, "end": v(17.16, 8.2) * mm});
            skArc(sketch, "E338.0", {"start": v(15.46, 8.2) * mm, "mid": v(15.29, 8.28) * mm, "end": v(15.21, 8.45) * mm});
            skLineSegment(sketch, "E339.0", {"start": v(15.21, 9.5) * mm, "end": v(15.21, 8.45) * mm});
            skArc(sketch, "E340.0", {"start": v(15.21, 9.5) * mm, "mid": v(15.36, 9.86) * mm, "end": v(15.71, 10) * mm});
            skLineSegment(sketch, "E341.0", {"start": v(21.21, 10) * mm, "end": v(15.71, 10) * mm});
            skArc(sketch, "E342.0", {"start": v(21.21, 10) * mm, "mid": v(22.27, 9.56) * mm, "end": v(22.71, 8.5) * mm});
            skLineSegment(sketch, "E343.0", {"start": v(22.71, 8.5) * mm, "end": v(22.71, 3) * mm});
            skArc(sketch, "E344.0", {"start": v(22.71, 3) * mm, "mid": v(22.57, 2.65) * mm, "end": v(22.21, 2.5) * mm});
            skLineSegment(sketch, "E345.0", {"start": v(21.16, 2.5) * mm, "end": v(22.21, 2.5) * mm});
            skArc(sketch, "E346.0", {"start": v(21.16, 2.5) * mm, "mid": v(20.99, 2.58) * mm, "end": v(20.91, 2.75) * mm});
            skLineSegment(sketch, "E347.0", {"start": v(20.91, 4.45) * mm, "end": v(20.91, 2.75) * mm});
            skArc(sketch, "E348.0", {"start": v(19.04, 5.22) * mm, "mid": v(20.23, 5.46) * mm, "end": v(20.91, 4.45) * mm});
            skLineSegment(sketch, "E349.0", {"start": v(16.75, 2.94) * mm, "end": v(19.04, 5.22) * mm});
            skArc(sketch, "E350.0", {"start": v(16.31, 1.88) * mm, "mid": v(16.43, 2.45) * mm, "end": v(16.75, 2.94) * mm});
            skLineSegment(sketch, "E351.0", {"start": v(16.31, 1.88) * mm, "end": v(16.31, -1.88) * mm});
            skCircle(sketch, "E352.0", {"center": v(12.71, 0) * mm, "radius": 2.15 * mm});
            skArc(sketch, "E353.0", {"start": v(16.75, -2.94) * mm, "mid": v(16.43, -2.45) * mm, "end": v(16.31, -1.88) * mm});
            skLineSegment(sketch, "E354.0", {"start": v(16.75, -2.94) * mm, "end": v(19.04, -5.22) * mm});
            skArc(sketch, "E355.0", {"start": v(20.91, -4.44) * mm, "mid": v(20.23, -5.46) * mm, "end": v(19.04, -5.22) * mm});
            skLineSegment(sketch, "E356.0", {"start": v(20.91, -2.75) * mm, "end": v(20.91, -4.44) * mm});
            skArc(sketch, "E357.0", {"start": v(20.91, -2.75) * mm, "mid": v(20.99, -2.57) * mm, "end": v(21.16, -2.5) * mm});
            skLineSegment(sketch, "E358.0", {"start": v(21.16, -2.5) * mm, "end": v(22.21, -2.5) * mm});
            skArc(sketch, "E359.0", {"start": v(22.21, -2.5) * mm, "mid": v(22.57, -2.64) * mm, "end": v(22.71, -3) * mm});
            skLineSegment(sketch, "E360.0", {"start": v(22.71, -3) * mm, "end": v(22.71, -8.5) * mm});
            skArc(sketch, "E361.0", {"start": v(22.71, -8.5) * mm, "mid": v(22.27, -9.56) * mm, "end": v(21.21, -10) * mm});
            skLineSegment(sketch, "E362.0", {"start": v(21.21, -10) * mm, "end": v(15.71, -10) * mm});
            skArc(sketch, "E363.0", {"start": v(15.71, -10) * mm, "mid": v(15.36, -9.85) * mm, "end": v(15.21, -9.5) * mm});
            skLineSegment(sketch, "E364.0", {"start": v(15.21, -9.5) * mm, "end": v(15.21, -8.45) * mm});
            skArc(sketch, "E365.0", {"start": v(15.21, -8.45) * mm, "mid": v(15.29, -8.27) * mm, "end": v(15.46, -8.2) * mm});
            skLineSegment(sketch, "E366.0", {"start": v(17.16, -8.2) * mm, "end": v(15.46, -8.2) * mm});
            skArc(sketch, "E367.0", {"start": v(17.94, -6.32) * mm, "mid": v(18.17, -7.52) * mm, "end": v(17.16, -8.2) * mm});
            skLineSegment(sketch, "E368.0", {"start": v(15.65, -4.04) * mm, "end": v(17.94, -6.32) * mm});
            skArc(sketch, "E369.0", {"start": v(14.6, -3.6) * mm, "mid": v(15.17, -3.71) * mm, "end": v(15.65, -4.04) * mm});
            skLineSegment(sketch, "E370.0", {"start": v(14.6, -3.6) * mm, "end": v(10.84, -3.6) * mm});
            skArc(sketch, "E371.0", {"start": v(9.77, -4.04) * mm, "mid": v(10.26, -3.71) * mm, "end": v(10.84, -3.6) * mm});
            skLineSegment(sketch, "E372.0", {"start": v(9.77, -4.04) * mm, "end": v(7.5, -6.32) * mm});
            skArc(sketch, "E373.0", {"start": v(8.27, -8.2) * mm, "mid": v(7.25, -7.52) * mm, "end": v(7.5, -6.32) * mm});
            skLineSegment(sketch, "E374.0", {"start": v(9.96, -8.2) * mm, "end": v(8.27, -8.2) * mm});
            skArc(sketch, "E375.0", {"start": v(9.96, -8.2) * mm, "mid": v(10.14, -8.27) * mm, "end": v(10.21, -8.45) * mm});
            skLineSegment(sketch, "E376.0", {"start": v(10.21, -9.5) * mm, "end": v(10.21, -8.45) * mm});
            skArc(sketch, "E377.0", {"start": v(10.21, -9.5) * mm, "mid": v(10.07, -9.85) * mm, "end": v(9.71, -10) * mm});
            skLineSegment(sketch, "E378", {"start": v(-4.29, 10) * mm, "end": v(9.71, 10) * mm});
            skLineSegment(sketch, "E379", {"start": v(-3.25, 2.94) * mm, "end": v(1.57, 7.76) * mm});
            skLineSegment(sketch, "E380", {"start": v(3.85, 7.76) * mm, "end": v(8.67, 2.94) * mm});
            skLineSegment(sketch, "E381", {"start": v(8.67, -2.94) * mm, "end": v(3.85, -7.76) * mm});
            skLineSegment(sketch, "E382", {"start": v(1.57, -7.76) * mm, "end": v(-3.25, -2.94) * mm});
            skLineSegment(sketch, "E383", {"start": v(-4.29, -10) * mm, "end": v(9.71, -10) * mm});
            skSolve(sketch);
        }
        {
            var Q0;
            Q0=qCreatedBy(makeId("Front.planeOp"),FACE);
            var sketch = newSketch(context, id + "F4", { "sketchPlane" : qUnion([Q0])});
            skLineSegment(sketch, "E384.0.0", {"start": v(-10.29, 10) * mm, "end": v(-15.79, 10) * mm});
            skArc(sketch, "E384.0.1", {"start": v(-15.79, 10) * mm, "mid": v(-16.85, 9.56) * mm, "end": v(-17.29, 8.5) * mm});
            skLineSegment(sketch, "E384.0.2", {"start": v(-17.29, 8.5) * mm, "end": v(-17.29, 3) * mm});
            skArc(sketch, "E384.0.3", {"start": v(-17.29, 3) * mm, "mid": v(-17.14, 2.65) * mm, "end": v(-16.79, 2.5) * mm});
            skLineSegment(sketch, "E384.0.4", {"start": v(-16.79, 2.5) * mm, "end": v(-15.74, 2.5) * mm});
            skArc(sketch, "E384.0.5", {"start": v(-15.74, 2.5) * mm, "mid": v(-15.56, 2.58) * mm, "end": v(-15.49, 2.75) * mm});
            skLineSegment(sketch, "E384.0.6", {"start": v(-15.49, 2.75) * mm, "end": v(-15.49, 4.45) * mm});
            skArc(sketch, "E384.0.7", {"start": v(-15.49, 4.45) * mm, "mid": v(-14.8, 5.46) * mm, "end": v(-13.6, 5.22) * mm});
            skLineSegment(sketch, "E384.0.8", {"start": v(-13.6, 5.22) * mm, "end": v(-11.33, 2.94) * mm});
            skArc(sketch, "E384.0.9", {"start": v(-11.33, 2.94) * mm, "mid": v(-11, 2.45) * mm, "end": v(-10.89, 1.88) * mm});
            skLineSegment(sketch, "E384.0.10", {"start": v(-10.89, 1.88) * mm, "end": v(-10.89, -1.88) * mm});
            skArc(sketch, "E384.0.11", {"start": v(-10.89, -1.88) * mm, "mid": v(-11, -2.45) * mm, "end": v(-11.33, -2.94) * mm});
            skLineSegment(sketch, "E384.0.12", {"start": v(-11.33, -2.94) * mm, "end": v(-13.6, -5.22) * mm});
            skArc(sketch, "E384.0.13", {"start": v(-13.6, -5.22) * mm, "mid": v(-14.8, -5.46) * mm, "end": v(-15.49, -4.44) * mm});
            skLineSegment(sketch, "E384.0.14", {"start": v(-15.49, -4.44) * mm, "end": v(-15.49, -2.75) * mm});
            skArc(sketch, "E384.0.15", {"start": v(-15.49, -2.75) * mm, "mid": v(-15.56, -2.57) * mm, "end": v(-15.74, -2.5) * mm});
            skLineSegment(sketch, "E384.0.16", {"start": v(-15.74, -2.5) * mm, "end": v(-16.79, -2.5) * mm});
            skArc(sketch, "E384.0.17", {"start": v(-16.79, -2.5) * mm, "mid": v(-17.14, -2.64) * mm, "end": v(-17.29, -3) * mm});
            skLineSegment(sketch, "E384.0.18", {"start": v(-17.29, -3) * mm, "end": v(-17.29, -8.5) * mm});
            skArc(sketch, "E384.0.19", {"start": v(-17.29, -8.5) * mm, "mid": v(-16.85, -9.56) * mm, "end": v(-15.79, -10) * mm});
            skLineSegment(sketch, "E384.0.20", {"start": v(-15.79, -10) * mm, "end": v(-10.29, -10) * mm});
            skArc(sketch, "E384.0.21", {"start": v(-10.29, -10) * mm, "mid": v(-9.93, -9.85) * mm, "end": v(-9.79, -9.5) * mm});
            skLineSegment(sketch, "E384.0.22", {"start": v(-9.79, -9.5) * mm, "end": v(-9.79, -8.45) * mm});
            skArc(sketch, "E384.0.23", {"start": v(-9.79, -8.45) * mm, "mid": v(-9.86, -8.27) * mm, "end": v(-10.04, -8.2) * mm});
            skLineSegment(sketch, "E384.0.24", {"start": v(-10.04, -8.2) * mm, "end": v(-11.73, -8.2) * mm});
            skArc(sketch, "E384.0.25", {"start": v(-11.73, -8.2) * mm, "mid": v(-12.75, -7.52) * mm, "end": v(-12.5, -6.32) * mm});
            skLineSegment(sketch, "E384.0.26", {"start": v(-12.5, -6.32) * mm, "end": v(-10.23, -4.04) * mm});
            skArc(sketch, "E384.0.27", {"start": v(-10.23, -4.04) * mm, "mid": v(-9.74, -3.71) * mm, "end": v(-9.16, -3.6) * mm});
            skLineSegment(sketch, "E384.0.28", {"start": v(-9.16, -3.6) * mm, "end": v(-5.4, -3.6) * mm});
            skArc(sketch, "E384.0.29", {"start": v(-5.4, -3.6) * mm, "mid": v(-4.83, -3.71) * mm, "end": v(-4.35, -4.04) * mm});
            skLineSegment(sketch, "E384.0.30", {"start": v(-4.35, -4.04) * mm, "end": v(-2.06, -6.32) * mm});
            skArc(sketch, "E384.0.31", {"start": v(-2.06, -6.32) * mm, "mid": v(-1.83, -7.52) * mm, "end": v(-2.84, -8.2) * mm});
            skLineSegment(sketch, "E384.0.32", {"start": v(-2.84, -8.2) * mm, "end": v(-4.54, -8.2) * mm});
            skArc(sketch, "E384.0.33", {"start": v(-4.54, -8.2) * mm, "mid": v(-4.71, -8.27) * mm, "end": v(-4.79, -8.45) * mm});
            skLineSegment(sketch, "E384.0.34", {"start": v(-4.79, -8.45) * mm, "end": v(-4.79, -9.5) * mm});
            skArc(sketch, "E384.0.35", {"start": v(-4.79, -9.5) * mm, "mid": v(-4.64, -9.85) * mm, "end": v(-4.29, -10) * mm});
            skLineSegment(sketch, "E384.0.36", {"start": v(-4.29, -10) * mm, "end": v(9.71, -10) * mm});
            skArc(sketch, "E384.0.37", {"start": v(9.71, -10) * mm, "mid": v(10.07, -9.85) * mm, "end": v(10.21, -9.5) * mm});
            skLineSegment(sketch, "E384.0.38", {"start": v(10.21, -9.5) * mm, "end": v(10.21, -8.45) * mm});
            skArc(sketch, "E384.0.39", {"start": v(10.21, -8.45) * mm, "mid": v(10.14, -8.27) * mm, "end": v(9.96, -8.2) * mm});
            skLineSegment(sketch, "E384.0.40", {"start": v(9.96, -8.2) * mm, "end": v(8.27, -8.2) * mm});
            skArc(sketch, "E384.0.41", {"start": v(8.27, -8.2) * mm, "mid": v(7.25, -7.52) * mm, "end": v(7.5, -6.32) * mm});
            skLineSegment(sketch, "E384.0.42", {"start": v(7.5, -6.32) * mm, "end": v(9.77, -4.04) * mm});
            skArc(sketch, "E384.0.43", {"start": v(9.77, -4.04) * mm, "mid": v(10.26, -3.71) * mm, "end": v(10.84, -3.6) * mm});
            skLineSegment(sketch, "E384.0.44", {"start": v(10.84, -3.6) * mm, "end": v(14.6, -3.6) * mm});
            skArc(sketch, "E384.0.45", {"start": v(14.6, -3.6) * mm, "mid": v(15.17, -3.71) * mm, "end": v(15.65, -4.04) * mm});
            skLineSegment(sketch, "E384.0.46", {"start": v(15.65, -4.04) * mm, "end": v(17.94, -6.32) * mm});
            skArc(sketch, "E384.0.47", {"start": v(17.94, -6.32) * mm, "mid": v(18.17, -7.52) * mm, "end": v(17.16, -8.2) * mm});
            skLineSegment(sketch, "E384.0.48", {"start": v(17.16, -8.2) * mm, "end": v(15.46, -8.2) * mm});
            skArc(sketch, "E384.0.49", {"start": v(15.46, -8.2) * mm, "mid": v(15.29, -8.27) * mm, "end": v(15.21, -8.45) * mm});
            skLineSegment(sketch, "E384.0.50", {"start": v(15.21, -8.45) * mm, "end": v(15.21, -9.5) * mm});
            skArc(sketch, "E384.0.51", {"start": v(15.21, -9.5) * mm, "mid": v(15.36, -9.85) * mm, "end": v(15.71, -10) * mm});
            skArc(sketch, "E384.0.61", {"start": v(16.75, -2.94) * mm, "mid": v(16.43, -2.45) * mm, "end": v(16.31, -1.88) * mm});
            skLineSegment(sketch, "E384.0.62", {"start": v(16.31, -1.88) * mm, "end": v(16.31, 1.88) * mm});
            skArc(sketch, "E384.0.63", {"start": v(16.31, 1.88) * mm, "mid": v(16.43, 2.45) * mm, "end": v(16.75, 2.94) * mm});
            skArc(sketch, "E384.0.73", {"start": v(15.71, 10) * mm, "mid": v(15.36, 9.86) * mm, "end": v(15.21, 9.5) * mm});
            skLineSegment(sketch, "E384.0.74", {"start": v(15.21, 9.5) * mm, "end": v(15.21, 8.45) * mm});
            skArc(sketch, "E384.0.75", {"start": v(15.21, 8.45) * mm, "mid": v(15.29, 8.28) * mm, "end": v(15.46, 8.2) * mm});
            skLineSegment(sketch, "E384.0.76", {"start": v(15.46, 8.2) * mm, "end": v(17.16, 8.2) * mm});
            skArc(sketch, "E384.0.77", {"start": v(17.16, 8.2) * mm, "mid": v(18.17, 7.52) * mm, "end": v(17.94, 6.32) * mm});
            skLineSegment(sketch, "E384.0.78", {"start": v(17.94, 6.32) * mm, "end": v(15.65, 4.04) * mm});
            skArc(sketch, "E384.0.79", {"start": v(15.65, 4.04) * mm, "mid": v(15.17, 3.72) * mm, "end": v(14.6, 3.6) * mm});
            skLineSegment(sketch, "E384.0.80", {"start": v(14.6, 3.6) * mm, "end": v(10.84, 3.6) * mm});
            skArc(sketch, "E384.0.81", {"start": v(10.84, 3.6) * mm, "mid": v(10.26, 3.72) * mm, "end": v(9.77, 4.04) * mm});
            skLineSegment(sketch, "E384.0.82", {"start": v(9.77, 4.04) * mm, "end": v(7.5, 6.32) * mm});
            skArc(sketch, "E384.0.83", {"start": v(7.5, 6.32) * mm, "mid": v(7.25, 7.52) * mm, "end": v(8.27, 8.2) * mm});
            skLineSegment(sketch, "E384.0.84", {"start": v(8.27, 8.2) * mm, "end": v(9.96, 8.2) * mm});
            skArc(sketch, "E384.0.85", {"start": v(9.96, 8.2) * mm, "mid": v(10.14, 8.28) * mm, "end": v(10.21, 8.45) * mm});
            skLineSegment(sketch, "E384.0.86", {"start": v(10.21, 8.45) * mm, "end": v(10.21, 9.5) * mm});
            skArc(sketch, "E384.0.87", {"start": v(10.21, 9.5) * mm, "mid": v(10.07, 9.86) * mm, "end": v(9.71, 10) * mm});
            skLineSegment(sketch, "E384.0.88", {"start": v(9.71, 10) * mm, "end": v(-4.29, 10) * mm});
            skArc(sketch, "E384.0.89", {"start": v(-4.29, 10) * mm, "mid": v(-4.64, 9.86) * mm, "end": v(-4.79, 9.5) * mm});
            skLineSegment(sketch, "E384.0.90", {"start": v(-4.79, 9.5) * mm, "end": v(-4.79, 8.45) * mm});
            skArc(sketch, "E384.0.91", {"start": v(-4.79, 8.45) * mm, "mid": v(-4.71, 8.28) * mm, "end": v(-4.54, 8.2) * mm});
            skLineSegment(sketch, "E384.0.92", {"start": v(-4.54, 8.2) * mm, "end": v(-2.84, 8.2) * mm});
            skArc(sketch, "E384.0.93", {"start": v(-2.84, 8.2) * mm, "mid": v(-1.83, 7.52) * mm, "end": v(-2.06, 6.32) * mm});
            skLineSegment(sketch, "E384.0.94", {"start": v(-2.06, 6.32) * mm, "end": v(-4.35, 4.04) * mm});
            skArc(sketch, "E384.0.95", {"start": v(-4.35, 4.04) * mm, "mid": v(-4.83, 3.72) * mm, "end": v(-5.4, 3.6) * mm});
            skLineSegment(sketch, "E384.0.96", {"start": v(-5.4, 3.6) * mm, "end": v(-9.16, 3.6) * mm});
            skArc(sketch, "E384.0.97", {"start": v(-9.16, 3.6) * mm, "mid": v(-9.74, 3.72) * mm, "end": v(-10.23, 4.04) * mm});
            skLineSegment(sketch, "E384.0.98", {"start": v(-10.23, 4.04) * mm, "end": v(-12.5, 6.32) * mm});
            skArc(sketch, "E384.0.99", {"start": v(-12.5, 6.32) * mm, "mid": v(-12.75, 7.52) * mm, "end": v(-11.73, 8.2) * mm});
            skLineSegment(sketch, "E384.0.100", {"start": v(-11.73, 8.2) * mm, "end": v(-10.04, 8.2) * mm});
            skArc(sketch, "E384.0.101", {"start": v(-10.04, 8.2) * mm, "mid": v(-9.86, 8.28) * mm, "end": v(-9.79, 8.45) * mm});
            skLineSegment(sketch, "E384.0.102", {"start": v(-9.79, 8.45) * mm, "end": v(-9.79, 9.5) * mm});
            skArc(sketch, "E384.0.103", {"start": v(-9.79, 9.5) * mm, "mid": v(-9.93, 9.86) * mm, "end": v(-10.29, 10) * mm});
            skLineSegment(sketch, "E385.0.0", {"start": v(1.57, 7.76) * mm, "end": v(-3.25, 2.94) * mm});
            skArc(sketch, "E385.0.1", {"start": v(-3.25, 2.94) * mm, "mid": v(-3.57, 2.45) * mm, "end": v(-3.69, 1.88) * mm});
            skLineSegment(sketch, "E385.0.2", {"start": v(-3.69, 1.88) * mm, "end": v(-3.69, -1.88) * mm});
            skArc(sketch, "E385.0.3", {"start": v(-3.69, -1.88) * mm, "mid": v(-3.57, -2.45) * mm, "end": v(-3.25, -2.94) * mm});
            skLineSegment(sketch, "E385.0.4", {"start": v(-3.25, -2.94) * mm, "end": v(1.57, -7.76) * mm});
            skArc(sketch, "E385.0.5", {"start": v(1.57, -7.76) * mm, "mid": v(2.06, -8.08) * mm, "end": v(2.64, -8.2) * mm});
            skLineSegment(sketch, "E385.0.6", {"start": v(2.64, -8.2) * mm, "end": v(2.8, -8.2) * mm});
            skArc(sketch, "E385.0.7", {"start": v(2.8, -8.2) * mm, "mid": v(3.37, -8.08) * mm, "end": v(3.85, -7.76) * mm});
            skLineSegment(sketch, "E385.0.8", {"start": v(3.85, -7.76) * mm, "end": v(8.67, -2.94) * mm});
            skArc(sketch, "E385.0.9", {"start": v(8.67, -2.94) * mm, "mid": v(9, -2.45) * mm, "end": v(9.11, -1.88) * mm});
            skLineSegment(sketch, "E385.0.10", {"start": v(9.11, -1.88) * mm, "end": v(9.11, 1.88) * mm});
            skArc(sketch, "E385.0.11", {"start": v(9.11, 1.88) * mm, "mid": v(9, 2.45) * mm, "end": v(8.67, 2.94) * mm});
            skLineSegment(sketch, "E385.0.12", {"start": v(8.67, 2.94) * mm, "end": v(3.85, 7.76) * mm});
            skArc(sketch, "E385.0.13", {"start": v(3.85, 7.76) * mm, "mid": v(3.37, 8.09) * mm, "end": v(2.8, 8.2) * mm});
            skLineSegment(sketch, "E385.0.14", {"start": v(2.8, 8.2) * mm, "end": v(2.64, 8.2) * mm});
            skArc(sketch, "E385.0.15", {"start": v(2.64, 8.2) * mm, "mid": v(2.06, 8.09) * mm, "end": v(1.57, 7.76) * mm});
            skCircle(sketch, "E386.0", {"center": v(-7.29, 0) * mm, "radius": 2.15 * mm});
            skCircle(sketch, "E387.0", {"center": v(12.71, 0) * mm, "radius": 2.15 * mm});
            skLineSegment(sketch, "E388", {"start": v(12.71, 11.72) * mm, "end": v(12.71, -12.08) * mm, "construction": true});
            skLineSegment(sketch, "E389.0.MirrorCS", {"start": v(16.75, 2.94) * mm, "end": v(21.57, 7.76) * mm});
            skLineSegment(sketch, "E390.0.MirrorCS", {"start": v(21.57, -7.76) * mm, "end": v(16.75, -2.94) * mm});
            skArc(sketch, "E391.0.MirrorCS", {"start": v(22.64, -8.2) * mm, "mid": v(22.06, -8.08) * mm, "end": v(21.57, -7.76) * mm});
            skArc(sketch, "E392.0.MirrorCS", {"start": v(21.57, 7.76) * mm, "mid": v(22.06, 8.09) * mm, "end": v(22.64, 8.2) * mm});
            skLineSegment(sketch, "E393.0.MirrorCS", {"start": v(22.64, 8.2) * mm, "end": v(22.8, 8.2) * mm});
            skArc(sketch, "E394.0.MirrorCS", {"start": v(22.8, 8.2) * mm, "mid": v(23.37, 8.09) * mm, "end": v(23.85, 7.76) * mm});
            skLineSegment(sketch, "E395.0.MirrorCS", {"start": v(23.85, 7.76) * mm, "end": v(28.67, 2.94) * mm});
            skArc(sketch, "E396.0.MirrorCS", {"start": v(28.67, 2.94) * mm, "mid": v(29, 2.45) * mm, "end": v(29.11, 1.88) * mm});
            skLineSegment(sketch, "E397.0.MirrorCS", {"start": v(29.11, 1.88) * mm, "end": v(29.11, -1.88) * mm});
            skArc(sketch, "E398.0.MirrorCS", {"start": v(29.11, -1.88) * mm, "mid": v(29, -2.45) * mm, "end": v(28.67, -2.94) * mm});
            skLineSegment(sketch, "E399.0.MirrorCS", {"start": v(28.67, -2.94) * mm, "end": v(23.85, -7.76) * mm});
            skArc(sketch, "E400.0.MirrorCS", {"start": v(23.85, -7.76) * mm, "mid": v(23.37, -8.08) * mm, "end": v(22.8, -8.2) * mm});
            skLineSegment(sketch, "E401.0.MirrorCS", {"start": v(22.8, -8.2) * mm, "end": v(22.64, -8.2) * mm});
            skLineSegment(sketch, "E402.0.MirrorCS", {"start": v(29.71, -10) * mm, "end": v(15.71, -10) * mm});
            skLineSegment(sketch, "E403.0.MirrorCS", {"start": v(15.71, 10) * mm, "end": v(29.71, 10) * mm});
            skArc(sketch, "E404.0.MirrorCS", {"start": v(29.71, 10) * mm, "mid": v(30.07, 9.86) * mm, "end": v(30.21, 9.5) * mm});
            skLineSegment(sketch, "E405.0.MirrorCS", {"start": v(30.21, 9.5) * mm, "end": v(30.21, 8.45) * mm});
            skArc(sketch, "E406.0.MirrorCS", {"start": v(30.21, 8.45) * mm, "mid": v(30.14, 8.28) * mm, "end": v(29.96, 8.2) * mm});
            skLineSegment(sketch, "E407.0.MirrorCS", {"start": v(29.96, 8.2) * mm, "end": v(28.27, 8.2) * mm});
            skArc(sketch, "E408.0.MirrorCS", {"start": v(28.27, 8.2) * mm, "mid": v(27.25, 7.52) * mm, "end": v(27.5, 6.32) * mm});
            skLineSegment(sketch, "E409.0.MirrorCS", {"start": v(27.5, 6.32) * mm, "end": v(29.77, 4.04) * mm});
            skArc(sketch, "E410.0.MirrorCS", {"start": v(29.77, 4.04) * mm, "mid": v(30.26, 3.72) * mm, "end": v(30.84, 3.6) * mm});
            skLineSegment(sketch, "E411.0.MirrorCS", {"start": v(30.84, 3.6) * mm, "end": v(34.6, 3.6) * mm});
            skArc(sketch, "E412.0.MirrorCS", {"start": v(34.6, 3.6) * mm, "mid": v(35.17, 3.72) * mm, "end": v(35.65, 4.04) * mm});
            skLineSegment(sketch, "E413.0.MirrorCS", {"start": v(35.65, 4.04) * mm, "end": v(37.94, 6.32) * mm});
            skArc(sketch, "E414.0.MirrorCS", {"start": v(37.94, 6.32) * mm, "mid": v(38.17, 7.52) * mm, "end": v(37.16, 8.2) * mm});
            skLineSegment(sketch, "E415.0.MirrorCS", {"start": v(37.16, 8.2) * mm, "end": v(35.46, 8.2) * mm});
            skArc(sketch, "E416.0.MirrorCS", {"start": v(35.46, 8.2) * mm, "mid": v(35.29, 8.28) * mm, "end": v(35.21, 8.45) * mm});
            skLineSegment(sketch, "E417.0.MirrorCS", {"start": v(35.21, 8.45) * mm, "end": v(35.21, 9.5) * mm});
            skArc(sketch, "E418.0.MirrorCS", {"start": v(35.21, 9.5) * mm, "mid": v(35.36, 9.86) * mm, "end": v(35.71, 10) * mm});
            skLineSegment(sketch, "E419.0.MirrorCS", {"start": v(35.71, 10) * mm, "end": v(41.21, 10) * mm});
            skArc(sketch, "E420.0.MirrorCS", {"start": v(41.21, 10) * mm, "mid": v(42.27, 9.56) * mm, "end": v(42.71, 8.5) * mm});
            skLineSegment(sketch, "E421.0.MirrorCS", {"start": v(42.71, 8.5) * mm, "end": v(42.71, 3) * mm});
            skArc(sketch, "E422.0.MirrorCS", {"start": v(42.71, 3) * mm, "mid": v(42.57, 2.65) * mm, "end": v(42.21, 2.5) * mm});
            skLineSegment(sketch, "E423.0.MirrorCS", {"start": v(42.21, 2.5) * mm, "end": v(41.16, 2.5) * mm});
            skArc(sketch, "E424.0.MirrorCS", {"start": v(41.16, 2.5) * mm, "mid": v(40.99, 2.58) * mm, "end": v(40.91, 2.75) * mm});
            skLineSegment(sketch, "E425.0.MirrorCS", {"start": v(40.91, 2.75) * mm, "end": v(40.91, 4.45) * mm});
            skArc(sketch, "E426.0.MirrorCS", {"start": v(40.91, 4.45) * mm, "mid": v(40.23, 5.46) * mm, "end": v(39.04, 5.22) * mm});
            skLineSegment(sketch, "E427.0.MirrorCS", {"start": v(39.04, 5.22) * mm, "end": v(36.75, 2.94) * mm});
            skArc(sketch, "E428.0.MirrorCS", {"start": v(36.75, 2.94) * mm, "mid": v(36.43, 2.45) * mm, "end": v(36.31, 1.88) * mm});
            skLineSegment(sketch, "E429.0.MirrorCS", {"start": v(36.31, 1.88) * mm, "end": v(36.31, -1.88) * mm});
            skArc(sketch, "E430.0.MirrorCS", {"start": v(36.31, -1.88) * mm, "mid": v(36.43, -2.45) * mm, "end": v(36.75, -2.94) * mm});
            skLineSegment(sketch, "E431.0.MirrorCS", {"start": v(36.75, -2.94) * mm, "end": v(39.04, -5.22) * mm});
            skArc(sketch, "E432.0.MirrorCS", {"start": v(39.04, -5.22) * mm, "mid": v(40.23, -5.46) * mm, "end": v(40.91, -4.44) * mm});
            skLineSegment(sketch, "E433.0.MirrorCS", {"start": v(40.91, -4.44) * mm, "end": v(40.91, -2.75) * mm});
            skArc(sketch, "E434.0.MirrorCS", {"start": v(40.91, -2.75) * mm, "mid": v(40.99, -2.57) * mm, "end": v(41.16, -2.5) * mm});
            skLineSegment(sketch, "E435.0.MirrorCS", {"start": v(41.16, -2.5) * mm, "end": v(42.21, -2.5) * mm});
            skArc(sketch, "E436.0.MirrorCS", {"start": v(42.21, -2.5) * mm, "mid": v(42.57, -2.64) * mm, "end": v(42.71, -3) * mm});
            skLineSegment(sketch, "E437.0.MirrorCS", {"start": v(42.71, -3) * mm, "end": v(42.71, -8.5) * mm});
            skArc(sketch, "E438.0.MirrorCS", {"start": v(42.71, -8.5) * mm, "mid": v(42.27, -9.56) * mm, "end": v(41.21, -10) * mm});
            skLineSegment(sketch, "E439.0.MirrorCS", {"start": v(41.21, -10) * mm, "end": v(35.71, -10) * mm});
            skArc(sketch, "E440.0.MirrorCS", {"start": v(35.71, -10) * mm, "mid": v(35.36, -9.85) * mm, "end": v(35.21, -9.5) * mm});
            skLineSegment(sketch, "E441.0.MirrorCS", {"start": v(35.21, -9.5) * mm, "end": v(35.21, -8.45) * mm});
            skArc(sketch, "E442.0.MirrorCS", {"start": v(35.21, -8.45) * mm, "mid": v(35.29, -8.27) * mm, "end": v(35.46, -8.2) * mm});
            skLineSegment(sketch, "E443.0.MirrorCS", {"start": v(35.46, -8.2) * mm, "end": v(37.16, -8.2) * mm});
            skArc(sketch, "E444.0.MirrorCS", {"start": v(37.16, -8.2) * mm, "mid": v(38.17, -7.52) * mm, "end": v(37.94, -6.32) * mm});
            skLineSegment(sketch, "E445.0.MirrorCS", {"start": v(37.94, -6.32) * mm, "end": v(35.65, -4.04) * mm});
            skArc(sketch, "E446.0.MirrorCS", {"start": v(35.65, -4.04) * mm, "mid": v(35.17, -3.71) * mm, "end": v(34.6, -3.6) * mm});
            skLineSegment(sketch, "E447.0.MirrorCS", {"start": v(34.6, -3.6) * mm, "end": v(30.84, -3.6) * mm});
            skArc(sketch, "E448.0.MirrorCS", {"start": v(30.84, -3.6) * mm, "mid": v(30.26, -3.71) * mm, "end": v(29.77, -4.04) * mm});
            skLineSegment(sketch, "E449.0.MirrorCS", {"start": v(29.77, -4.04) * mm, "end": v(27.5, -6.32) * mm});
            skArc(sketch, "E450.0.MirrorCS", {"start": v(27.5, -6.32) * mm, "mid": v(27.25, -7.52) * mm, "end": v(28.27, -8.2) * mm});
            skLineSegment(sketch, "E451.0.MirrorCS", {"start": v(28.27, -8.2) * mm, "end": v(29.96, -8.2) * mm});
            skArc(sketch, "E452.0.MirrorCS", {"start": v(29.96, -8.2) * mm, "mid": v(30.14, -8.27) * mm, "end": v(30.21, -8.45) * mm});
            skLineSegment(sketch, "E453.0.MirrorCS", {"start": v(30.21, -8.45) * mm, "end": v(30.21, -9.5) * mm});
            skArc(sketch, "E454.0.MirrorCS", {"start": v(30.21, -9.5) * mm, "mid": v(30.07, -9.85) * mm, "end": v(29.71, -10) * mm});
            skCircle(sketch, "E455.0.MirrorC", {"center": v(32.71, 0) * mm, "radius": 2.15 * mm});
            skSolve(sketch);
        }
        {
            var Q0;
            Q0=qCreatedBy(makeId("Front.planeOp"),FACE);
            var sketch = newSketch(context, id + "F5", { "sketchPlane" : qUnion([Q0])});
            skLineSegment(sketch, "E456.0.0", {"start": v(-10.29, 10) * mm, "end": v(-15.79, 10) * mm});
            skArc(sketch, "E456.0.1", {"start": v(-15.79, 10) * mm, "mid": v(-16.85, 9.56) * mm, "end": v(-17.29, 8.5) * mm});
            skLineSegment(sketch, "E456.0.2", {"start": v(-17.29, 8.5) * mm, "end": v(-17.29, 3) * mm});
            skArc(sketch, "E456.0.3", {"start": v(-17.29, 3) * mm, "mid": v(-17.14, 2.65) * mm, "end": v(-16.79, 2.5) * mm});
            skLineSegment(sketch, "E456.0.4", {"start": v(-16.79, 2.5) * mm, "end": v(-15.74, 2.5) * mm});
            skArc(sketch, "E456.0.5", {"start": v(-15.74, 2.5) * mm, "mid": v(-15.56, 2.58) * mm, "end": v(-15.49, 2.75) * mm});
            skLineSegment(sketch, "E456.0.6", {"start": v(-15.49, 2.75) * mm, "end": v(-15.49, 4.45) * mm});
            skArc(sketch, "E456.0.7", {"start": v(-15.49, 4.45) * mm, "mid": v(-14.8, 5.46) * mm, "end": v(-13.6, 5.22) * mm});
            skLineSegment(sketch, "E456.0.8", {"start": v(-13.6, 5.22) * mm, "end": v(-11.33, 2.94) * mm});
            skArc(sketch, "E456.0.9", {"start": v(-11.33, 2.94) * mm, "mid": v(-11, 2.45) * mm, "end": v(-10.89, 1.88) * mm});
            skLineSegment(sketch, "E456.0.10", {"start": v(-10.89, 1.88) * mm, "end": v(-10.89, -1.88) * mm});
            skArc(sketch, "E456.0.11", {"start": v(-10.89, -1.88) * mm, "mid": v(-11, -2.45) * mm, "end": v(-11.33, -2.94) * mm});
            skLineSegment(sketch, "E456.0.12", {"start": v(-11.33, -2.94) * mm, "end": v(-13.6, -5.22) * mm});
            skArc(sketch, "E456.0.13", {"start": v(-13.6, -5.22) * mm, "mid": v(-14.8, -5.46) * mm, "end": v(-15.49, -4.44) * mm});
            skLineSegment(sketch, "E456.0.14", {"start": v(-15.49, -4.44) * mm, "end": v(-15.49, -2.75) * mm});
            skArc(sketch, "E456.0.15", {"start": v(-15.49, -2.75) * mm, "mid": v(-15.56, -2.57) * mm, "end": v(-15.74, -2.5) * mm});
            skLineSegment(sketch, "E456.0.16", {"start": v(-15.74, -2.5) * mm, "end": v(-16.79, -2.5) * mm});
            skArc(sketch, "E456.0.17", {"start": v(-16.79, -2.5) * mm, "mid": v(-17.14, -2.64) * mm, "end": v(-17.29, -3) * mm});
            skLineSegment(sketch, "E456.0.18", {"start": v(-17.29, -3) * mm, "end": v(-17.29, -8.5) * mm});
            skArc(sketch, "E456.0.19", {"start": v(-17.29, -8.5) * mm, "mid": v(-16.85, -9.56) * mm, "end": v(-15.79, -10) * mm});
            skLineSegment(sketch, "E456.0.20", {"start": v(-15.79, -10) * mm, "end": v(-10.29, -10) * mm});
            skArc(sketch, "E456.0.21", {"start": v(-10.29, -10) * mm, "mid": v(-9.93, -9.85) * mm, "end": v(-9.79, -9.5) * mm});
            skLineSegment(sketch, "E456.0.22", {"start": v(-9.79, -9.5) * mm, "end": v(-9.79, -8.45) * mm});
            skArc(sketch, "E456.0.23", {"start": v(-9.79, -8.45) * mm, "mid": v(-9.86, -8.27) * mm, "end": v(-10.04, -8.2) * mm});
            skLineSegment(sketch, "E456.0.24", {"start": v(-10.04, -8.2) * mm, "end": v(-11.73, -8.2) * mm});
            skArc(sketch, "E456.0.25", {"start": v(-11.73, -8.2) * mm, "mid": v(-12.75, -7.52) * mm, "end": v(-12.5, -6.32) * mm});
            skLineSegment(sketch, "E456.0.26", {"start": v(-12.5, -6.32) * mm, "end": v(-10.23, -4.04) * mm});
            skArc(sketch, "E456.0.27", {"start": v(-10.23, -4.04) * mm, "mid": v(-9.74, -3.71) * mm, "end": v(-9.16, -3.6) * mm});
            skLineSegment(sketch, "E456.0.28", {"start": v(-9.16, -3.6) * mm, "end": v(-5.4, -3.6) * mm});
            skArc(sketch, "E456.0.29", {"start": v(-5.4, -3.6) * mm, "mid": v(-4.83, -3.71) * mm, "end": v(-4.35, -4.04) * mm});
            skLineSegment(sketch, "E456.0.30", {"start": v(-4.35, -4.04) * mm, "end": v(-2.06, -6.32) * mm});
            skArc(sketch, "E456.0.31", {"start": v(-2.06, -6.32) * mm, "mid": v(-1.83, -7.52) * mm, "end": v(-2.84, -8.2) * mm});
            skLineSegment(sketch, "E456.0.32", {"start": v(-2.84, -8.2) * mm, "end": v(-4.54, -8.2) * mm});
            skArc(sketch, "E456.0.33", {"start": v(-4.54, -8.2) * mm, "mid": v(-4.71, -8.27) * mm, "end": v(-4.79, -8.45) * mm});
            skLineSegment(sketch, "E456.0.34", {"start": v(-4.79, -8.45) * mm, "end": v(-4.79, -9.5) * mm});
            skArc(sketch, "E456.0.35", {"start": v(-4.79, -9.5) * mm, "mid": v(-4.64, -9.85) * mm, "end": v(-4.29, -10) * mm});
            skLineSegment(sketch, "E456.0.36", {"start": v(-4.29, -10) * mm, "end": v(9.71, -10) * mm});
            skArc(sketch, "E456.0.37", {"start": v(9.71, -10) * mm, "mid": v(10.07, -9.85) * mm, "end": v(10.21, -9.5) * mm});
            skLineSegment(sketch, "E456.0.38", {"start": v(10.21, -9.5) * mm, "end": v(10.21, -8.45) * mm});
            skArc(sketch, "E456.0.39", {"start": v(10.21, -8.45) * mm, "mid": v(10.14, -8.27) * mm, "end": v(9.96, -8.2) * mm});
            skLineSegment(sketch, "E456.0.40", {"start": v(9.96, -8.2) * mm, "end": v(8.27, -8.2) * mm});
            skArc(sketch, "E456.0.41", {"start": v(8.27, -8.2) * mm, "mid": v(7.25, -7.52) * mm, "end": v(7.5, -6.32) * mm});
            skLineSegment(sketch, "E456.0.42", {"start": v(7.5, -6.32) * mm, "end": v(9.77, -4.04) * mm});
            skArc(sketch, "E456.0.43", {"start": v(9.77, -4.04) * mm, "mid": v(10.26, -3.71) * mm, "end": v(10.84, -3.6) * mm});
            skLineSegment(sketch, "E456.0.44", {"start": v(10.84, -3.6) * mm, "end": v(14.6, -3.6) * mm});
            skArc(sketch, "E456.0.45", {"start": v(14.6, -3.6) * mm, "mid": v(15.17, -3.71) * mm, "end": v(15.65, -4.04) * mm});
            skLineSegment(sketch, "E456.0.46", {"start": v(15.65, -4.04) * mm, "end": v(17.94, -6.32) * mm});
            skArc(sketch, "E456.0.47", {"start": v(17.94, -6.32) * mm, "mid": v(18.17, -7.52) * mm, "end": v(17.16, -8.2) * mm});
            skLineSegment(sketch, "E456.0.48", {"start": v(17.16, -8.2) * mm, "end": v(15.46, -8.2) * mm});
            skArc(sketch, "E456.0.49", {"start": v(15.46, -8.2) * mm, "mid": v(15.29, -8.27) * mm, "end": v(15.21, -8.45) * mm});
            skLineSegment(sketch, "E456.0.50", {"start": v(15.21, -8.45) * mm, "end": v(15.21, -9.5) * mm});
            skArc(sketch, "E456.0.51", {"start": v(15.21, -9.5) * mm, "mid": v(15.36, -9.85) * mm, "end": v(15.71, -10) * mm});
            skArc(sketch, "E456.0.61", {"start": v(16.75, -2.94) * mm, "mid": v(16.43, -2.45) * mm, "end": v(16.31, -1.88) * mm});
            skLineSegment(sketch, "E456.0.62", {"start": v(16.31, -1.88) * mm, "end": v(16.31, 1.88) * mm});
            skArc(sketch, "E456.0.63", {"start": v(16.31, 1.88) * mm, "mid": v(16.43, 2.45) * mm, "end": v(16.75, 2.94) * mm});
            skArc(sketch, "E456.0.73", {"start": v(15.71, 10) * mm, "mid": v(15.36, 9.86) * mm, "end": v(15.21, 9.5) * mm});
            skLineSegment(sketch, "E456.0.74", {"start": v(15.21, 9.5) * mm, "end": v(15.21, 8.45) * mm});
            skArc(sketch, "E456.0.75", {"start": v(15.21, 8.45) * mm, "mid": v(15.29, 8.28) * mm, "end": v(15.46, 8.2) * mm});
            skLineSegment(sketch, "E456.0.76", {"start": v(15.46, 8.2) * mm, "end": v(17.16, 8.2) * mm});
            skArc(sketch, "E456.0.77", {"start": v(17.16, 8.2) * mm, "mid": v(18.17, 7.52) * mm, "end": v(17.94, 6.32) * mm});
            skLineSegment(sketch, "E456.0.78", {"start": v(17.94, 6.32) * mm, "end": v(15.65, 4.04) * mm});
            skArc(sketch, "E456.0.79", {"start": v(15.65, 4.04) * mm, "mid": v(15.17, 3.72) * mm, "end": v(14.6, 3.6) * mm});
            skLineSegment(sketch, "E456.0.80", {"start": v(14.6, 3.6) * mm, "end": v(10.84, 3.6) * mm});
            skArc(sketch, "E456.0.81", {"start": v(10.84, 3.6) * mm, "mid": v(10.26, 3.72) * mm, "end": v(9.77, 4.04) * mm});
            skLineSegment(sketch, "E456.0.82", {"start": v(9.77, 4.04) * mm, "end": v(7.5, 6.32) * mm});
            skArc(sketch, "E456.0.83", {"start": v(7.5, 6.32) * mm, "mid": v(7.25, 7.52) * mm, "end": v(8.27, 8.2) * mm});
            skLineSegment(sketch, "E456.0.84", {"start": v(8.27, 8.2) * mm, "end": v(9.96, 8.2) * mm});
            skArc(sketch, "E456.0.85", {"start": v(9.96, 8.2) * mm, "mid": v(10.14, 8.28) * mm, "end": v(10.21, 8.45) * mm});
            skLineSegment(sketch, "E456.0.86", {"start": v(10.21, 8.45) * mm, "end": v(10.21, 9.5) * mm});
            skArc(sketch, "E456.0.87", {"start": v(10.21, 9.5) * mm, "mid": v(10.07, 9.86) * mm, "end": v(9.71, 10) * mm});
            skLineSegment(sketch, "E456.0.88", {"start": v(9.71, 10) * mm, "end": v(-4.29, 10) * mm});
            skArc(sketch, "E456.0.89", {"start": v(-4.29, 10) * mm, "mid": v(-4.64, 9.86) * mm, "end": v(-4.79, 9.5) * mm});
            skLineSegment(sketch, "E456.0.90", {"start": v(-4.79, 9.5) * mm, "end": v(-4.79, 8.45) * mm});
            skArc(sketch, "E456.0.91", {"start": v(-4.79, 8.45) * mm, "mid": v(-4.71, 8.28) * mm, "end": v(-4.54, 8.2) * mm});
            skLineSegment(sketch, "E456.0.92", {"start": v(-4.54, 8.2) * mm, "end": v(-2.84, 8.2) * mm});
            skArc(sketch, "E456.0.93", {"start": v(-2.84, 8.2) * mm, "mid": v(-1.83, 7.52) * mm, "end": v(-2.06, 6.32) * mm});
            skLineSegment(sketch, "E456.0.94", {"start": v(-2.06, 6.32) * mm, "end": v(-4.35, 4.04) * mm});
            skArc(sketch, "E456.0.95", {"start": v(-4.35, 4.04) * mm, "mid": v(-4.83, 3.72) * mm, "end": v(-5.4, 3.6) * mm});
            skLineSegment(sketch, "E456.0.96", {"start": v(-5.4, 3.6) * mm, "end": v(-9.16, 3.6) * mm});
            skArc(sketch, "E456.0.97", {"start": v(-9.16, 3.6) * mm, "mid": v(-9.74, 3.72) * mm, "end": v(-10.23, 4.04) * mm});
            skLineSegment(sketch, "E456.0.98", {"start": v(-10.23, 4.04) * mm, "end": v(-12.5, 6.32) * mm});
            skArc(sketch, "E456.0.99", {"start": v(-12.5, 6.32) * mm, "mid": v(-12.75, 7.52) * mm, "end": v(-11.73, 8.2) * mm});
            skLineSegment(sketch, "E456.0.100", {"start": v(-11.73, 8.2) * mm, "end": v(-10.04, 8.2) * mm});
            skArc(sketch, "E456.0.101", {"start": v(-10.04, 8.2) * mm, "mid": v(-9.86, 8.28) * mm, "end": v(-9.79, 8.45) * mm});
            skLineSegment(sketch, "E456.0.102", {"start": v(-9.79, 8.45) * mm, "end": v(-9.79, 9.5) * mm});
            skArc(sketch, "E456.0.103", {"start": v(-9.79, 9.5) * mm, "mid": v(-9.93, 9.86) * mm, "end": v(-10.29, 10) * mm});
            skCircle(sketch, "E457.0.0", {"center": v(-7.29, 0) * mm, "radius": 2.15 * mm});
            skCircle(sketch, "E458.0.0", {"center": v(12.71, 0) * mm, "radius": 2.15 * mm});
            skLineSegment(sketch, "E459.0.0", {"start": v(1.57, 7.76) * mm, "end": v(-3.25, 2.94) * mm});
            skArc(sketch, "E459.0.1", {"start": v(-3.25, 2.94) * mm, "mid": v(-3.57, 2.45) * mm, "end": v(-3.69, 1.88) * mm});
            skLineSegment(sketch, "E459.0.2", {"start": v(-3.69, 1.88) * mm, "end": v(-3.69, -1.88) * mm});
            skArc(sketch, "E459.0.3", {"start": v(-3.69, -1.88) * mm, "mid": v(-3.57, -2.45) * mm, "end": v(-3.25, -2.94) * mm});
            skLineSegment(sketch, "E459.0.4", {"start": v(-3.25, -2.94) * mm, "end": v(1.57, -7.76) * mm});
            skArc(sketch, "E459.0.5", {"start": v(1.57, -7.76) * mm, "mid": v(2.06, -8.08) * mm, "end": v(2.64, -8.2) * mm});
            skLineSegment(sketch, "E459.0.6", {"start": v(2.64, -8.2) * mm, "end": v(2.8, -8.2) * mm});
            skArc(sketch, "E459.0.7", {"start": v(2.8, -8.2) * mm, "mid": v(3.37, -8.08) * mm, "end": v(3.85, -7.76) * mm});
            skLineSegment(sketch, "E459.0.8", {"start": v(3.85, -7.76) * mm, "end": v(8.67, -2.94) * mm});
            skArc(sketch, "E459.0.9", {"start": v(8.67, -2.94) * mm, "mid": v(9, -2.45) * mm, "end": v(9.11, -1.88) * mm});
            skLineSegment(sketch, "E459.0.10", {"start": v(9.11, -1.88) * mm, "end": v(9.11, 1.88) * mm});
            skArc(sketch, "E459.0.11", {"start": v(9.11, 1.88) * mm, "mid": v(9, 2.45) * mm, "end": v(8.67, 2.94) * mm});
            skLineSegment(sketch, "E459.0.12", {"start": v(8.67, 2.94) * mm, "end": v(3.85, 7.76) * mm});
            skArc(sketch, "E459.0.13", {"start": v(3.85, 7.76) * mm, "mid": v(3.37, 8.09) * mm, "end": v(2.8, 8.2) * mm});
            skLineSegment(sketch, "E459.0.14", {"start": v(2.8, 8.2) * mm, "end": v(2.64, 8.2) * mm});
            skArc(sketch, "E459.0.15", {"start": v(2.64, 8.2) * mm, "mid": v(2.06, 8.09) * mm, "end": v(1.57, 7.76) * mm});
            skLineSegment(sketch, "E460", {"start": v(22.71, 12.69) * mm, "end": v(22.71, -12.08) * mm, "construction": true});
            skCircle(sketch, "E461.0.MirrorC", {"center": v(32.71, 0) * mm, "radius": 2.15 * mm});
            skCircle(sketch, "E462.0.MirrorC", {"center": v(52.71, 0) * mm, "radius": 2.15 * mm});
            skArc(sketch, "E463.0.MirrorCS", {"start": v(29.11, 1.88) * mm, "mid": v(29, 2.45) * mm, "end": v(28.67, 2.94) * mm});
            skLineSegment(sketch, "E464.0.MirrorCS", {"start": v(29.11, -1.88) * mm, "end": v(29.11, 1.88) * mm});
            skArc(sketch, "E465.0.MirrorCS", {"start": v(28.67, -2.94) * mm, "mid": v(29, -2.45) * mm, "end": v(29.11, -1.88) * mm});
            skArc(sketch, "E466.0.MirrorCS", {"start": v(29.71, 10) * mm, "mid": v(30.07, 9.86) * mm, "end": v(30.21, 9.5) * mm});
            skLineSegment(sketch, "E467.0.MirrorCS", {"start": v(30.21, 9.5) * mm, "end": v(30.21, 8.45) * mm});
            skArc(sketch, "E468.0.MirrorCS", {"start": v(30.21, 8.45) * mm, "mid": v(30.14, 8.28) * mm, "end": v(29.96, 8.2) * mm});
            skLineSegment(sketch, "E469.0.MirrorCS", {"start": v(29.96, 8.2) * mm, "end": v(28.27, 8.2) * mm});
            skArc(sketch, "E470.0.MirrorCS", {"start": v(28.27, 8.2) * mm, "mid": v(27.25, 7.52) * mm, "end": v(27.5, 6.32) * mm});
            skLineSegment(sketch, "E471.0.MirrorCS", {"start": v(27.5, 6.32) * mm, "end": v(29.77, 4.04) * mm});
            skArc(sketch, "E472.0.MirrorCS", {"start": v(29.77, 4.04) * mm, "mid": v(30.26, 3.72) * mm, "end": v(30.84, 3.6) * mm});
            skLineSegment(sketch, "E473.0.MirrorCS", {"start": v(30.84, 3.6) * mm, "end": v(34.6, 3.6) * mm});
            skArc(sketch, "E474.0.MirrorCS", {"start": v(34.6, 3.6) * mm, "mid": v(35.17, 3.72) * mm, "end": v(35.65, 4.04) * mm});
            skLineSegment(sketch, "E475.0.MirrorCS", {"start": v(35.65, 4.04) * mm, "end": v(37.94, 6.32) * mm});
            skArc(sketch, "E476.0.MirrorCS", {"start": v(37.94, 6.32) * mm, "mid": v(38.17, 7.52) * mm, "end": v(37.16, 8.2) * mm});
            skLineSegment(sketch, "E477.0.MirrorCS", {"start": v(37.16, 8.2) * mm, "end": v(35.46, 8.2) * mm});
            skArc(sketch, "E478.0.MirrorCS", {"start": v(35.46, 8.2) * mm, "mid": v(35.29, 8.28) * mm, "end": v(35.21, 8.45) * mm});
            skLineSegment(sketch, "E479.0.MirrorCS", {"start": v(35.21, 8.45) * mm, "end": v(35.21, 9.5) * mm});
            skArc(sketch, "E480.0.MirrorCS", {"start": v(35.21, 9.5) * mm, "mid": v(35.36, 9.86) * mm, "end": v(35.71, 10) * mm});
            skLineSegment(sketch, "E481.0.MirrorCS", {"start": v(35.71, 10) * mm, "end": v(49.71, 10) * mm});
            skArc(sketch, "E482.0.MirrorCS", {"start": v(49.71, 10) * mm, "mid": v(50.07, 9.86) * mm, "end": v(50.21, 9.5) * mm});
            skLineSegment(sketch, "E483.0.MirrorCS", {"start": v(50.21, 9.5) * mm, "end": v(50.21, 8.45) * mm});
            skArc(sketch, "E484.0.MirrorCS", {"start": v(50.21, 8.45) * mm, "mid": v(50.14, 8.28) * mm, "end": v(49.96, 8.2) * mm});
            skLineSegment(sketch, "E485.0.MirrorCS", {"start": v(49.96, 8.2) * mm, "end": v(48.27, 8.2) * mm});
            skArc(sketch, "E486.0.MirrorCS", {"start": v(48.27, 8.2) * mm, "mid": v(47.25, 7.52) * mm, "end": v(47.5, 6.32) * mm});
            skLineSegment(sketch, "E487.0.MirrorCS", {"start": v(47.5, 6.32) * mm, "end": v(49.77, 4.04) * mm});
            skArc(sketch, "E488.0.MirrorCS", {"start": v(49.77, 4.04) * mm, "mid": v(50.26, 3.72) * mm, "end": v(50.84, 3.6) * mm});
            skLineSegment(sketch, "E489.0.MirrorCS", {"start": v(50.84, 3.6) * mm, "end": v(54.6, 3.6) * mm});
            skArc(sketch, "E490.0.MirrorCS", {"start": v(54.6, 3.6) * mm, "mid": v(55.17, 3.72) * mm, "end": v(55.65, 4.04) * mm});
            skLineSegment(sketch, "E491.0.MirrorCS", {"start": v(55.65, 4.04) * mm, "end": v(57.94, 6.32) * mm});
            skArc(sketch, "E492.0.MirrorCS", {"start": v(57.94, 6.32) * mm, "mid": v(58.17, 7.52) * mm, "end": v(57.16, 8.2) * mm});
            skLineSegment(sketch, "E493.0.MirrorCS", {"start": v(57.16, 8.2) * mm, "end": v(55.46, 8.2) * mm});
            skArc(sketch, "E494.0.MirrorCS", {"start": v(55.46, 8.2) * mm, "mid": v(55.29, 8.28) * mm, "end": v(55.21, 8.45) * mm});
            skLineSegment(sketch, "E495.0.MirrorCS", {"start": v(55.21, 8.45) * mm, "end": v(55.21, 9.5) * mm});
            skArc(sketch, "E496.0.MirrorCS", {"start": v(55.21, 9.5) * mm, "mid": v(55.36, 9.86) * mm, "end": v(55.71, 10) * mm});
            skLineSegment(sketch, "E497.0.MirrorCS", {"start": v(55.71, 10) * mm, "end": v(61.21, 10) * mm});
            skArc(sketch, "E498.0.MirrorCS", {"start": v(61.21, 10) * mm, "mid": v(62.27, 9.56) * mm, "end": v(62.71, 8.5) * mm});
            skLineSegment(sketch, "E499.0.MirrorCS", {"start": v(62.71, 8.5) * mm, "end": v(62.71, 3) * mm});
            skArc(sketch, "E500.0.MirrorCS", {"start": v(62.71, 3) * mm, "mid": v(62.57, 2.65) * mm, "end": v(62.21, 2.5) * mm});
            skLineSegment(sketch, "E501.0.MirrorCS", {"start": v(62.21, 2.5) * mm, "end": v(61.16, 2.5) * mm});
            skArc(sketch, "E502.0.MirrorCS", {"start": v(61.16, 2.5) * mm, "mid": v(60.99, 2.58) * mm, "end": v(60.91, 2.75) * mm});
            skLineSegment(sketch, "E503.0.MirrorCS", {"start": v(60.91, 2.75) * mm, "end": v(60.91, 4.45) * mm});
            skArc(sketch, "E504.0.MirrorCS", {"start": v(60.91, 4.45) * mm, "mid": v(60.23, 5.46) * mm, "end": v(59.04, 5.22) * mm});
            skLineSegment(sketch, "E505.0.MirrorCS", {"start": v(59.04, 5.22) * mm, "end": v(56.75, 2.94) * mm});
            skArc(sketch, "E506.0.MirrorCS", {"start": v(56.75, 2.94) * mm, "mid": v(56.43, 2.45) * mm, "end": v(56.31, 1.88) * mm});
            skLineSegment(sketch, "E507.0.MirrorCS", {"start": v(56.31, 1.88) * mm, "end": v(56.31, -1.88) * mm});
            skArc(sketch, "E508.0.MirrorCS", {"start": v(56.31, -1.88) * mm, "mid": v(56.43, -2.45) * mm, "end": v(56.75, -2.94) * mm});
            skLineSegment(sketch, "E509.0.MirrorCS", {"start": v(56.75, -2.94) * mm, "end": v(59.04, -5.22) * mm});
            skArc(sketch, "E510.0.MirrorCS", {"start": v(59.04, -5.22) * mm, "mid": v(60.23, -5.46) * mm, "end": v(60.91, -4.44) * mm});
            skLineSegment(sketch, "E511.0.MirrorCS", {"start": v(60.91, -4.44) * mm, "end": v(60.91, -2.75) * mm});
            skArc(sketch, "E512.0.MirrorCS", {"start": v(60.91, -2.75) * mm, "mid": v(60.99, -2.57) * mm, "end": v(61.16, -2.5) * mm});
            skLineSegment(sketch, "E513.0.MirrorCS", {"start": v(61.16, -2.5) * mm, "end": v(62.21, -2.5) * mm});
            skArc(sketch, "E514.0.MirrorCS", {"start": v(62.21, -2.5) * mm, "mid": v(62.57, -2.64) * mm, "end": v(62.71, -3) * mm});
            skLineSegment(sketch, "E515.0.MirrorCS", {"start": v(62.71, -3) * mm, "end": v(62.71, -8.5) * mm});
            skArc(sketch, "E516.0.MirrorCS", {"start": v(62.71, -8.5) * mm, "mid": v(62.27, -9.56) * mm, "end": v(61.21, -10) * mm});
            skLineSegment(sketch, "E517.0.MirrorCS", {"start": v(61.21, -10) * mm, "end": v(55.71, -10) * mm});
            skArc(sketch, "E518.0.MirrorCS", {"start": v(55.71, -10) * mm, "mid": v(55.36, -9.85) * mm, "end": v(55.21, -9.5) * mm});
            skLineSegment(sketch, "E519.0.MirrorCS", {"start": v(55.21, -9.5) * mm, "end": v(55.21, -8.45) * mm});
            skArc(sketch, "E520.0.MirrorCS", {"start": v(55.21, -8.45) * mm, "mid": v(55.29, -8.27) * mm, "end": v(55.46, -8.2) * mm});
            skLineSegment(sketch, "E521.0.MirrorCS", {"start": v(55.46, -8.2) * mm, "end": v(57.16, -8.2) * mm});
            skArc(sketch, "E522.0.MirrorCS", {"start": v(57.16, -8.2) * mm, "mid": v(58.17, -7.52) * mm, "end": v(57.94, -6.32) * mm});
            skLineSegment(sketch, "E523.0.MirrorCS", {"start": v(57.94, -6.32) * mm, "end": v(55.65, -4.04) * mm});
            skArc(sketch, "E524.0.MirrorCS", {"start": v(55.65, -4.04) * mm, "mid": v(55.17, -3.71) * mm, "end": v(54.6, -3.6) * mm});
            skLineSegment(sketch, "E525.0.MirrorCS", {"start": v(54.6, -3.6) * mm, "end": v(50.84, -3.6) * mm});
            skArc(sketch, "E526.0.MirrorCS", {"start": v(50.84, -3.6) * mm, "mid": v(50.26, -3.71) * mm, "end": v(49.77, -4.04) * mm});
            skLineSegment(sketch, "E527.0.MirrorCS", {"start": v(49.77, -4.04) * mm, "end": v(47.5, -6.32) * mm});
            skArc(sketch, "E528.0.MirrorCS", {"start": v(47.5, -6.32) * mm, "mid": v(47.25, -7.52) * mm, "end": v(48.27, -8.2) * mm});
            skLineSegment(sketch, "E529.0.MirrorCS", {"start": v(48.27, -8.2) * mm, "end": v(49.96, -8.2) * mm});
            skArc(sketch, "E530.0.MirrorCS", {"start": v(49.96, -8.2) * mm, "mid": v(50.14, -8.27) * mm, "end": v(50.21, -8.45) * mm});
            skLineSegment(sketch, "E531.0.MirrorCS", {"start": v(50.21, -8.45) * mm, "end": v(50.21, -9.5) * mm});
            skArc(sketch, "E532.0.MirrorCS", {"start": v(50.21, -9.5) * mm, "mid": v(50.07, -9.85) * mm, "end": v(49.71, -10) * mm});
            skLineSegment(sketch, "E533.0.MirrorCS", {"start": v(49.71, -10) * mm, "end": v(35.71, -10) * mm});
            skArc(sketch, "E534.0.MirrorCS", {"start": v(35.71, -10) * mm, "mid": v(35.36, -9.85) * mm, "end": v(35.21, -9.5) * mm});
            skLineSegment(sketch, "E535.0.MirrorCS", {"start": v(35.21, -9.5) * mm, "end": v(35.21, -8.45) * mm});
            skArc(sketch, "E536.0.MirrorCS", {"start": v(35.21, -8.45) * mm, "mid": v(35.29, -8.27) * mm, "end": v(35.46, -8.2) * mm});
            skLineSegment(sketch, "E537.0.MirrorCS", {"start": v(35.46, -8.2) * mm, "end": v(37.16, -8.2) * mm});
            skArc(sketch, "E538.0.MirrorCS", {"start": v(37.16, -8.2) * mm, "mid": v(38.17, -7.52) * mm, "end": v(37.94, -6.32) * mm});
            skLineSegment(sketch, "E539.0.MirrorCS", {"start": v(37.94, -6.32) * mm, "end": v(35.65, -4.04) * mm});
            skArc(sketch, "E540.0.MirrorCS", {"start": v(35.65, -4.04) * mm, "mid": v(35.17, -3.71) * mm, "end": v(34.6, -3.6) * mm});
            skLineSegment(sketch, "E541.0.MirrorCS", {"start": v(34.6, -3.6) * mm, "end": v(30.84, -3.6) * mm});
            skArc(sketch, "E542.0.MirrorCS", {"start": v(30.84, -3.6) * mm, "mid": v(30.26, -3.71) * mm, "end": v(29.77, -4.04) * mm});
            skLineSegment(sketch, "E543.0.MirrorCS", {"start": v(29.77, -4.04) * mm, "end": v(27.5, -6.32) * mm});
            skArc(sketch, "E544.0.MirrorCS", {"start": v(27.5, -6.32) * mm, "mid": v(27.25, -7.52) * mm, "end": v(28.27, -8.2) * mm});
            skLineSegment(sketch, "E545.0.MirrorCS", {"start": v(28.27, -8.2) * mm, "end": v(29.96, -8.2) * mm});
            skArc(sketch, "E546.0.MirrorCS", {"start": v(29.96, -8.2) * mm, "mid": v(30.14, -8.27) * mm, "end": v(30.21, -8.45) * mm});
            skLineSegment(sketch, "E547.0.MirrorCS", {"start": v(30.21, -8.45) * mm, "end": v(30.21, -9.5) * mm});
            skArc(sketch, "E548.0.MirrorCS", {"start": v(30.21, -9.5) * mm, "mid": v(30.07, -9.85) * mm, "end": v(29.71, -10) * mm});
            skLineSegment(sketch, "E549.0.MirrorCS", {"start": v(36.31, -1.88) * mm, "end": v(36.31, 1.88) * mm});
            skArc(sketch, "E550.0.MirrorCS", {"start": v(36.31, 1.88) * mm, "mid": v(36.43, 2.45) * mm, "end": v(36.75, 2.94) * mm});
            skLineSegment(sketch, "E551.0.MirrorCS", {"start": v(36.75, 2.94) * mm, "end": v(41.57, 7.76) * mm});
            skArc(sketch, "E552.0.MirrorCS", {"start": v(41.57, 7.76) * mm, "mid": v(42.06, 8.09) * mm, "end": v(42.64, 8.2) * mm});
            skLineSegment(sketch, "E553.0.MirrorCS", {"start": v(42.64, 8.2) * mm, "end": v(42.8, 8.2) * mm});
            skArc(sketch, "E554.0.MirrorCS", {"start": v(42.8, 8.2) * mm, "mid": v(43.37, 8.09) * mm, "end": v(43.85, 7.76) * mm});
            skLineSegment(sketch, "E555.0.MirrorCS", {"start": v(43.85, 7.76) * mm, "end": v(48.67, 2.94) * mm});
            skArc(sketch, "E556.0.MirrorCS", {"start": v(48.67, 2.94) * mm, "mid": v(49, 2.45) * mm, "end": v(49.11, 1.88) * mm});
            skLineSegment(sketch, "E557.0.MirrorCS", {"start": v(49.11, 1.88) * mm, "end": v(49.11, -1.88) * mm});
            skArc(sketch, "E558.0.MirrorCS", {"start": v(49.11, -1.88) * mm, "mid": v(49, -2.45) * mm, "end": v(48.67, -2.94) * mm});
            skLineSegment(sketch, "E559.0.MirrorCS", {"start": v(48.67, -2.94) * mm, "end": v(43.85, -7.76) * mm});
            skArc(sketch, "E560.0.MirrorCS", {"start": v(43.85, -7.76) * mm, "mid": v(43.37, -8.08) * mm, "end": v(42.8, -8.2) * mm});
            skLineSegment(sketch, "E561.0.MirrorCS", {"start": v(42.8, -8.2) * mm, "end": v(42.64, -8.2) * mm});
            skArc(sketch, "E562.0.MirrorCS", {"start": v(42.64, -8.2) * mm, "mid": v(42.06, -8.08) * mm, "end": v(41.57, -7.76) * mm});
            skLineSegment(sketch, "E563.0.MirrorCS", {"start": v(41.57, -7.76) * mm, "end": v(36.75, -2.94) * mm});
            skArc(sketch, "E564.0.MirrorCS", {"start": v(36.75, -2.94) * mm, "mid": v(36.43, -2.45) * mm, "end": v(36.31, -1.88) * mm});
            skLineSegment(sketch, "E565", {"start": v(15.71, 10) * mm, "end": v(29.71, 10) * mm});
            skLineSegment(sketch, "E566", {"start": v(15.71, -10) * mm, "end": v(29.71, -10) * mm});
            skLineSegment(sketch, "E567", {"start": v(12.71, 12.57) * mm, "end": v(12.71, -12.54) * mm, "construction": true});
            skLineSegment(sketch, "E568.0.MirrorCS", {"start": v(21.57, -7.76) * mm, "end": v(16.75, -2.94) * mm});
            skLineSegment(sketch, "E569.0.MirrorCS", {"start": v(16.75, 2.94) * mm, "end": v(21.57, 7.76) * mm});
            skLineSegment(sketch, "E570.0.MirrorCS", {"start": v(23.85, 7.76) * mm, "end": v(28.67, 2.94) * mm});
            skLineSegment(sketch, "E571.0.MirrorCS", {"start": v(28.67, -2.94) * mm, "end": v(23.85, -7.76) * mm});
            skArc(sketch, "E572.0.MirrorCS", {"start": v(22.8, 8.2) * mm, "mid": v(23.37, 8.09) * mm, "end": v(23.85, 7.76) * mm});
            skArc(sketch, "E573.0.MirrorCS", {"start": v(21.57, 7.76) * mm, "mid": v(22.06, 8.09) * mm, "end": v(22.64, 8.2) * mm});
            skArc(sketch, "E574.0.MirrorCS", {"start": v(23.85, -7.76) * mm, "mid": v(23.37, -8.08) * mm, "end": v(22.8, -8.2) * mm});
            skArc(sketch, "E575.0.MirrorCS", {"start": v(22.64, -8.2) * mm, "mid": v(22.06, -8.08) * mm, "end": v(21.57, -7.76) * mm});
            skLineSegment(sketch, "E576.0.MirrorCS", {"start": v(22.8, -8.2) * mm, "end": v(22.64, -8.2) * mm});
            skLineSegment(sketch, "E577.0.MirrorCS", {"start": v(22.64, 8.2) * mm, "end": v(22.8, 8.2) * mm});
            skSolve(sketch);
        }
        {
            var Q0;
            Q0=qCreatedBy(makeId("Front.planeOp"),FACE);
            var sketch = newSketch(context, id + "F6", { "sketchPlane" : qUnion([Q0])});
            skLineSegment(sketch, "E578.0.0", {"start": v(-10.29, 10) * mm, "end": v(-15.79, 10) * mm});
            skArc(sketch, "E578.0.1", {"start": v(-15.79, 10) * mm, "mid": v(-16.85, 9.56) * mm, "end": v(-17.29, 8.5) * mm});
            skLineSegment(sketch, "E578.0.2", {"start": v(-17.29, 8.5) * mm, "end": v(-17.29, 3) * mm});
            skArc(sketch, "E578.0.3", {"start": v(-17.29, 3) * mm, "mid": v(-17.14, 2.65) * mm, "end": v(-16.79, 2.5) * mm});
            skLineSegment(sketch, "E578.0.4", {"start": v(-16.79, 2.5) * mm, "end": v(-15.74, 2.5) * mm});
            skArc(sketch, "E578.0.5", {"start": v(-15.74, 2.5) * mm, "mid": v(-15.56, 2.58) * mm, "end": v(-15.49, 2.75) * mm});
            skLineSegment(sketch, "E578.0.6", {"start": v(-15.49, 2.75) * mm, "end": v(-15.49, 4.45) * mm});
            skArc(sketch, "E578.0.7", {"start": v(-15.49, 4.45) * mm, "mid": v(-14.8, 5.46) * mm, "end": v(-13.6, 5.22) * mm});
            skLineSegment(sketch, "E578.0.8", {"start": v(-13.6, 5.22) * mm, "end": v(-11.33, 2.94) * mm});
            skArc(sketch, "E578.0.9", {"start": v(-11.33, 2.94) * mm, "mid": v(-11, 2.45) * mm, "end": v(-10.89, 1.88) * mm});
            skLineSegment(sketch, "E578.0.10", {"start": v(-10.89, 1.88) * mm, "end": v(-10.89, -1.88) * mm});
            skArc(sketch, "E578.0.11", {"start": v(-10.89, -1.88) * mm, "mid": v(-11, -2.45) * mm, "end": v(-11.33, -2.94) * mm});
            skLineSegment(sketch, "E578.0.12", {"start": v(-11.33, -2.94) * mm, "end": v(-13.6, -5.22) * mm});
            skArc(sketch, "E578.0.13", {"start": v(-13.6, -5.22) * mm, "mid": v(-14.8, -5.46) * mm, "end": v(-15.49, -4.44) * mm});
            skLineSegment(sketch, "E578.0.14", {"start": v(-15.49, -4.44) * mm, "end": v(-15.49, -2.75) * mm});
            skArc(sketch, "E578.0.15", {"start": v(-15.49, -2.75) * mm, "mid": v(-15.56, -2.57) * mm, "end": v(-15.74, -2.5) * mm});
            skLineSegment(sketch, "E578.0.16", {"start": v(-15.74, -2.5) * mm, "end": v(-16.79, -2.5) * mm});
            skArc(sketch, "E578.0.17", {"start": v(-16.79, -2.5) * mm, "mid": v(-17.14, -2.64) * mm, "end": v(-17.29, -3) * mm});
            skArc(sketch, "E578.0.27", {"start": v(-10.23, -4.04) * mm, "mid": v(-9.74, -3.71) * mm, "end": v(-9.16, -3.6) * mm});
            skLineSegment(sketch, "E578.0.28", {"start": v(-9.16, -3.6) * mm, "end": v(-5.4, -3.6) * mm});
            skLineSegment(sketch, "E578.0.44", {"start": v(10.84, -3.6) * mm, "end": v(14.6, -3.6) * mm});
            skArc(sketch, "E578.0.45", {"start": v(14.6, -3.6) * mm, "mid": v(15.17, -3.71) * mm, "end": v(15.65, -4.04) * mm});
            skArc(sketch, "E578.0.55", {"start": v(22.71, -3) * mm, "mid": v(22.57, -2.64) * mm, "end": v(22.21, -2.5) * mm});
            skLineSegment(sketch, "E578.0.56", {"start": v(22.21, -2.5) * mm, "end": v(21.16, -2.5) * mm});
            skArc(sketch, "E578.0.57", {"start": v(21.16, -2.5) * mm, "mid": v(20.99, -2.57) * mm, "end": v(20.91, -2.75) * mm});
            skLineSegment(sketch, "E578.0.58", {"start": v(20.91, -2.75) * mm, "end": v(20.91, -4.44) * mm});
            skArc(sketch, "E578.0.59", {"start": v(20.91, -4.44) * mm, "mid": v(20.23, -5.46) * mm, "end": v(19.04, -5.22) * mm});
            skLineSegment(sketch, "E578.0.60", {"start": v(19.04, -5.22) * mm, "end": v(16.75, -2.94) * mm});
            skArc(sketch, "E578.0.61", {"start": v(16.75, -2.94) * mm, "mid": v(16.43, -2.45) * mm, "end": v(16.31, -1.88) * mm});
            skLineSegment(sketch, "E578.0.62", {"start": v(16.31, -1.88) * mm, "end": v(16.31, 1.88) * mm});
            skArc(sketch, "E578.0.63", {"start": v(16.31, 1.88) * mm, "mid": v(16.43, 2.45) * mm, "end": v(16.75, 2.94) * mm});
            skLineSegment(sketch, "E578.0.64", {"start": v(16.75, 2.94) * mm, "end": v(19.04, 5.22) * mm});
            skArc(sketch, "E578.0.65", {"start": v(19.04, 5.22) * mm, "mid": v(20.23, 5.46) * mm, "end": v(20.91, 4.45) * mm});
            skLineSegment(sketch, "E578.0.66", {"start": v(20.91, 4.45) * mm, "end": v(20.91, 2.75) * mm});
            skArc(sketch, "E578.0.67", {"start": v(20.91, 2.75) * mm, "mid": v(20.99, 2.58) * mm, "end": v(21.16, 2.5) * mm});
            skLineSegment(sketch, "E578.0.68", {"start": v(21.16, 2.5) * mm, "end": v(22.21, 2.5) * mm});
            skArc(sketch, "E578.0.69", {"start": v(22.21, 2.5) * mm, "mid": v(22.57, 2.65) * mm, "end": v(22.71, 3) * mm});
            skLineSegment(sketch, "E578.0.70", {"start": v(22.71, 3) * mm, "end": v(22.71, 8.5) * mm});
            skArc(sketch, "E578.0.71", {"start": v(22.71, 8.5) * mm, "mid": v(22.27, 9.56) * mm, "end": v(21.21, 10) * mm});
            skLineSegment(sketch, "E578.0.72", {"start": v(21.21, 10) * mm, "end": v(15.71, 10) * mm});
            skArc(sketch, "E578.0.73", {"start": v(15.71, 10) * mm, "mid": v(15.36, 9.86) * mm, "end": v(15.21, 9.5) * mm});
            skLineSegment(sketch, "E578.0.74", {"start": v(15.21, 9.5) * mm, "end": v(15.21, 8.45) * mm});
            skArc(sketch, "E578.0.75", {"start": v(15.21, 8.45) * mm, "mid": v(15.29, 8.28) * mm, "end": v(15.46, 8.2) * mm});
            skLineSegment(sketch, "E578.0.76", {"start": v(15.46, 8.2) * mm, "end": v(17.16, 8.2) * mm});
            skArc(sketch, "E578.0.77", {"start": v(17.16, 8.2) * mm, "mid": v(18.17, 7.52) * mm, "end": v(17.94, 6.32) * mm});
            skLineSegment(sketch, "E578.0.78", {"start": v(17.94, 6.32) * mm, "end": v(15.65, 4.04) * mm});
            skArc(sketch, "E578.0.79", {"start": v(15.65, 4.04) * mm, "mid": v(15.17, 3.72) * mm, "end": v(14.6, 3.6) * mm});
            skLineSegment(sketch, "E578.0.80", {"start": v(14.6, 3.6) * mm, "end": v(10.84, 3.6) * mm});
            skArc(sketch, "E578.0.81", {"start": v(10.84, 3.6) * mm, "mid": v(10.26, 3.72) * mm, "end": v(9.77, 4.04) * mm});
            skLineSegment(sketch, "E578.0.82", {"start": v(9.77, 4.04) * mm, "end": v(7.5, 6.32) * mm});
            skArc(sketch, "E578.0.83", {"start": v(7.5, 6.32) * mm, "mid": v(7.25, 7.52) * mm, "end": v(8.27, 8.2) * mm});
            skLineSegment(sketch, "E578.0.84", {"start": v(8.27, 8.2) * mm, "end": v(9.96, 8.2) * mm});
            skArc(sketch, "E578.0.85", {"start": v(9.96, 8.2) * mm, "mid": v(10.14, 8.28) * mm, "end": v(10.21, 8.45) * mm});
            skLineSegment(sketch, "E578.0.86", {"start": v(10.21, 8.45) * mm, "end": v(10.21, 9.5) * mm});
            skArc(sketch, "E578.0.87", {"start": v(10.21, 9.5) * mm, "mid": v(10.07, 9.86) * mm, "end": v(9.71, 10) * mm});
            skLineSegment(sketch, "E578.0.88", {"start": v(9.71, 10) * mm, "end": v(-4.29, 10) * mm});
            skArc(sketch, "E578.0.89", {"start": v(-4.29, 10) * mm, "mid": v(-4.64, 9.86) * mm, "end": v(-4.79, 9.5) * mm});
            skLineSegment(sketch, "E578.0.90", {"start": v(-4.79, 9.5) * mm, "end": v(-4.79, 8.45) * mm});
            skArc(sketch, "E578.0.91", {"start": v(-4.79, 8.45) * mm, "mid": v(-4.71, 8.28) * mm, "end": v(-4.54, 8.2) * mm});
            skLineSegment(sketch, "E578.0.92", {"start": v(-4.54, 8.2) * mm, "end": v(-2.84, 8.2) * mm});
            skArc(sketch, "E578.0.93", {"start": v(-2.84, 8.2) * mm, "mid": v(-1.83, 7.52) * mm, "end": v(-2.06, 6.32) * mm});
            skLineSegment(sketch, "E578.0.94", {"start": v(-2.06, 6.32) * mm, "end": v(-4.35, 4.04) * mm});
            skArc(sketch, "E578.0.95", {"start": v(-4.35, 4.04) * mm, "mid": v(-4.83, 3.72) * mm, "end": v(-5.4, 3.6) * mm});
            skLineSegment(sketch, "E578.0.96", {"start": v(-5.4, 3.6) * mm, "end": v(-9.16, 3.6) * mm});
            skArc(sketch, "E578.0.97", {"start": v(-9.16, 3.6) * mm, "mid": v(-9.74, 3.72) * mm, "end": v(-10.23, 4.04) * mm});
            skLineSegment(sketch, "E578.0.98", {"start": v(-10.23, 4.04) * mm, "end": v(-12.5, 6.32) * mm});
            skArc(sketch, "E578.0.99", {"start": v(-12.5, 6.32) * mm, "mid": v(-12.75, 7.52) * mm, "end": v(-11.73, 8.2) * mm});
            skLineSegment(sketch, "E578.0.100", {"start": v(-11.73, 8.2) * mm, "end": v(-10.04, 8.2) * mm});
            skArc(sketch, "E578.0.101", {"start": v(-10.04, 8.2) * mm, "mid": v(-9.86, 8.28) * mm, "end": v(-9.79, 8.45) * mm});
            skLineSegment(sketch, "E578.0.102", {"start": v(-9.79, 8.45) * mm, "end": v(-9.79, 9.5) * mm});
            skArc(sketch, "E578.0.103", {"start": v(-9.79, 9.5) * mm, "mid": v(-9.93, 9.86) * mm, "end": v(-10.29, 10) * mm});
            skCircle(sketch, "E579.0", {"center": v(-7.29, 0) * mm, "radius": 2.15 * mm});
            skLineSegment(sketch, "E580.0.0", {"start": v(1.57, 7.76) * mm, "end": v(-3.25, 2.94) * mm});
            skArc(sketch, "E580.0.1", {"start": v(-3.25, 2.94) * mm, "mid": v(-3.57, 2.45) * mm, "end": v(-3.69, 1.88) * mm});
            skLineSegment(sketch, "E580.0.2", {"start": v(-3.69, 1.88) * mm, "end": v(-3.69, -1.88) * mm});
            skLineSegment(sketch, "E580.0.10", {"start": v(9.11, -1.88) * mm, "end": v(9.11, 1.88) * mm});
            skArc(sketch, "E580.0.11", {"start": v(9.11, 1.88) * mm, "mid": v(9, 2.45) * mm, "end": v(8.67, 2.94) * mm});
            skLineSegment(sketch, "E580.0.12", {"start": v(8.67, 2.94) * mm, "end": v(3.85, 7.76) * mm});
            skArc(sketch, "E580.0.13", {"start": v(3.85, 7.76) * mm, "mid": v(3.37, 8.09) * mm, "end": v(2.8, 8.2) * mm});
            skLineSegment(sketch, "E580.0.14", {"start": v(2.8, 8.2) * mm, "end": v(2.64, 8.2) * mm});
            skArc(sketch, "E580.0.15", {"start": v(2.64, 8.2) * mm, "mid": v(2.06, 8.09) * mm, "end": v(1.57, 7.76) * mm});
            skCircle(sketch, "E581.0.0", {"center": v(12.71, 0) * mm, "radius": 2.15 * mm});
            skLineSegment(sketch, "E582.1", {"start": v(-15.79, 10) * mm, "end": v(-10.29, 10) * mm});
            skLineSegment(sketch, "E582.3", {"start": v(-9.79, 9.5) * mm, "end": v(-9.79, 8.45) * mm});
            skLineSegment(sketch, "E582.5", {"start": v(-10.04, 8.2) * mm, "end": v(-11.73, 8.2) * mm});
            skArc(sketch, "E582.6", {"start": v(-11.73, 8.2) * mm, "mid": v(-12.75, 7.52) * mm, "end": v(-12.5, 6.32) * mm});
            skArc(sketch, "E582.8", {"start": v(-10.23, 4.04) * mm, "mid": v(-9.74, 3.72) * mm, "end": v(-9.16, 3.6) * mm});
            skLineSegment(sketch, "E582.9", {"start": v(-9.16, 3.6) * mm, "end": v(-5.4, 3.6) * mm});
            skArc(sketch, "E582.10", {"start": v(-5.4, 3.6) * mm, "mid": v(-4.83, 3.72) * mm, "end": v(-4.35, 4.04) * mm});
            skLineSegment(sketch, "E582.11", {"start": v(-4.35, 4.04) * mm, "end": v(-2.06, 6.32) * mm});
            skArc(sketch, "E582.12", {"start": v(-2.06, 6.32) * mm, "mid": v(-1.83, 7.52) * mm, "end": v(-2.84, 8.2) * mm});
            skLineSegment(sketch, "E582.13", {"start": v(-2.84, 8.2) * mm, "end": v(-4.54, 8.2) * mm});
            skLineSegment(sketch, "E582.19", {"start": v(-15.74, 2.5) * mm, "end": v(-16.79, 2.5) * mm});
            skLineSegment(sketch, "E582.21", {"start": v(-15.49, 4.45) * mm, "end": v(-15.49, 2.75) * mm});
            skArc(sketch, "E582.22", {"start": v(-13.6, 5.22) * mm, "mid": v(-14.8, 5.46) * mm, "end": v(-15.49, 4.45) * mm});
            skLineSegment(sketch, "E582.23", {"start": v(-11.33, 2.94) * mm, "end": v(-13.6, 5.22) * mm});
            skArc(sketch, "E582.24", {"start": v(-10.89, 1.88) * mm, "mid": v(-11, 2.45) * mm, "end": v(-11.33, 2.94) * mm});
            skArc(sketch, "E582.26", {"start": v(-11.33, -2.94) * mm, "mid": v(-11, -2.45) * mm, "end": v(-10.89, -1.88) * mm});
            skArc(sketch, "E582.28", {"start": v(-15.49, -4.44) * mm, "mid": v(-14.8, -5.46) * mm, "end": v(-13.6, -5.22) * mm});
            skLineSegment(sketch, "E582.29", {"start": v(-15.49, -2.75) * mm, "end": v(-15.49, -4.44) * mm});
            skArc(sketch, "E582.42", {"start": v(-9.16, -3.6) * mm, "mid": v(-9.74, -3.71) * mm, "end": v(-10.23, -4.04) * mm});
            skArc(sketch, "E582.57", {"start": v(8.67, 2.94) * mm, "mid": v(9, 2.45) * mm, "end": v(9.11, 1.88) * mm});
            skLineSegment(sketch, "E582.58", {"start": v(9.11, 1.88) * mm, "end": v(9.11, -1.88) * mm});
            skArc(sketch, "E582.64", {"start": v(9.71, 10) * mm, "mid": v(10.07, 9.86) * mm, "end": v(10.21, 9.5) * mm});
            skLineSegment(sketch, "E582.65", {"start": v(10.21, 9.5) * mm, "end": v(10.21, 8.45) * mm});
            skArc(sketch, "E582.66", {"start": v(10.21, 8.45) * mm, "mid": v(10.14, 8.28) * mm, "end": v(9.96, 8.2) * mm});
            skLineSegment(sketch, "E582.73", {"start": v(15.65, 4.04) * mm, "end": v(17.94, 6.32) * mm});
            skArc(sketch, "E582.76", {"start": v(15.46, 8.2) * mm, "mid": v(15.29, 8.28) * mm, "end": v(15.21, 8.45) * mm});
            skArc(sketch, "E582.78", {"start": v(15.21, 9.5) * mm, "mid": v(15.36, 9.86) * mm, "end": v(15.71, 10) * mm});
            skArc(sketch, "E582.80", {"start": v(21.21, 10) * mm, "mid": v(22.27, 9.56) * mm, "end": v(22.71, 8.5) * mm});
            skLineSegment(sketch, "E582.81", {"start": v(22.71, 8.5) * mm, "end": v(22.71, 3) * mm});
            skArc(sketch, "E582.82", {"start": v(22.71, 3) * mm, "mid": v(22.57, 2.65) * mm, "end": v(22.21, 2.5) * mm});
            skArc(sketch, "E582.84", {"start": v(21.16, 2.5) * mm, "mid": v(20.99, 2.58) * mm, "end": v(20.91, 2.75) * mm});
            skLineSegment(sketch, "E582.89", {"start": v(16.31, 1.88) * mm, "end": v(16.31, -1.88) * mm});
            skLineSegment(sketch, "E582.92", {"start": v(16.75, -2.94) * mm, "end": v(19.04, -5.22) * mm});
            skArc(sketch, "E582.95", {"start": v(20.91, -2.75) * mm, "mid": v(20.99, -2.57) * mm, "end": v(21.16, -2.5) * mm});
            skLineSegment(sketch, "E582.96", {"start": v(21.16, -2.5) * mm, "end": v(22.21, -2.5) * mm});
            skArc(sketch, "E582.97", {"start": v(22.21, -2.5) * mm, "mid": v(22.57, -2.64) * mm, "end": v(22.71, -3) * mm});
            skLineSegment(sketch, "E582.108", {"start": v(14.6, -3.6) * mm, "end": v(10.84, -3.6) * mm});
            skLineSegment(sketch, "E582.116", {"start": v(-4.29, 10) * mm, "end": v(9.71, 10) * mm});
            skLineSegment(sketch, "E582.117", {"start": v(-3.25, 2.94) * mm, "end": v(1.57, 7.76) * mm});
            skLineSegment(sketch, "E582.118", {"start": v(3.85, 7.76) * mm, "end": v(8.67, 2.94) * mm});
            skLineSegment(sketch, "E583", {"start": v(-19.41, -10) * mm, "end": v(25.27, -10) * mm, "construction": true});
            skLineSegment(sketch, "E584", {"start": v(-15.79, 8.5) * mm, "end": v(6.66, -13.95) * mm, "construction": true});
            skArc(sketch, "E585.0.MirrorCS", {"start": v(-16.79, -17.5) * mm, "mid": v(-17.14, -17.35) * mm, "end": v(-17.29, -17) * mm});
            skLineSegment(sketch, "E586.0.MirrorCS", {"start": v(-15.74, -17.5) * mm, "end": v(-16.79, -17.5) * mm});
            skArc(sketch, "E587.0.MirrorCS", {"start": v(-15.49, -17.25) * mm, "mid": v(-15.56, -17.42) * mm, "end": v(-15.74, -17.5) * mm});
            skLineSegment(sketch, "E588.0.MirrorCS", {"start": v(-15.49, -17.25) * mm, "end": v(-15.49, -15.55) * mm});
            skArc(sketch, "E589.0.MirrorCS", {"start": v(-13.6, -14.78) * mm, "mid": v(-14.8, -14.54) * mm, "end": v(-15.49, -15.55) * mm});
            skLineSegment(sketch, "E590.0.MirrorCS", {"start": v(-11.33, -17.06) * mm, "end": v(-13.6, -14.78) * mm});
            skArc(sketch, "E591.0.MirrorCS", {"start": v(-10.89, -18.12) * mm, "mid": v(-11, -17.55) * mm, "end": v(-11.33, -17.06) * mm});
            skLineSegment(sketch, "E592.0.MirrorCS", {"start": v(-10.89, -21.88) * mm, "end": v(-10.89, -18.12) * mm});
            skArc(sketch, "E593.0.MirrorCS", {"start": v(-11.33, -22.94) * mm, "mid": v(-11, -22.45) * mm, "end": v(-10.89, -21.88) * mm});
            skLineSegment(sketch, "E594.0.MirrorCS", {"start": v(-13.6, -25.22) * mm, "end": v(-11.33, -22.94) * mm});
            skArc(sketch, "E595.0.MirrorCS", {"start": v(-15.49, -24.44) * mm, "mid": v(-14.8, -25.46) * mm, "end": v(-13.6, -25.22) * mm});
            skLineSegment(sketch, "E596.0.MirrorCS", {"start": v(-15.49, -22.75) * mm, "end": v(-15.49, -24.44) * mm});
            skArc(sketch, "E597.0.MirrorCS", {"start": v(-15.74, -22.5) * mm, "mid": v(-15.56, -22.57) * mm, "end": v(-15.49, -22.75) * mm});
            skLineSegment(sketch, "E598.0.MirrorCS", {"start": v(-16.79, -22.5) * mm, "end": v(-15.74, -22.5) * mm});
            skArc(sketch, "E599.0.MirrorCS", {"start": v(-17.29, -23) * mm, "mid": v(-17.14, -22.64) * mm, "end": v(-16.79, -22.5) * mm});
            skLineSegment(sketch, "E600.0.MirrorCS", {"start": v(-17.29, -28.5) * mm, "end": v(-17.29, -23) * mm});
            skArc(sketch, "E601.0.MirrorCS", {"start": v(-15.79, -30) * mm, "mid": v(-16.85, -29.56) * mm, "end": v(-17.29, -28.5) * mm});
            skLineSegment(sketch, "E602.0.MirrorCS", {"start": v(-15.79, -30) * mm, "end": v(-10.29, -30) * mm});
            skArc(sketch, "E603.0.MirrorCS", {"start": v(-9.79, -29.5) * mm, "mid": v(-9.93, -29.85) * mm, "end": v(-10.29, -30) * mm});
            skLineSegment(sketch, "E604.0.MirrorCS", {"start": v(-9.79, -29.5) * mm, "end": v(-9.79, -28.45) * mm});
            skArc(sketch, "E605.0.MirrorCS", {"start": v(-10.04, -28.2) * mm, "mid": v(-9.86, -28.27) * mm, "end": v(-9.79, -28.45) * mm});
            skLineSegment(sketch, "E606.0.MirrorCS", {"start": v(-10.04, -28.2) * mm, "end": v(-11.73, -28.2) * mm});
            skArc(sketch, "E607.0.MirrorCS", {"start": v(-11.73, -28.2) * mm, "mid": v(-12.75, -27.52) * mm, "end": v(-12.5, -26.32) * mm});
            skLineSegment(sketch, "E608.0.MirrorCS", {"start": v(-10.23, -24.04) * mm, "end": v(-12.5, -26.32) * mm});
            skArc(sketch, "E609.0.MirrorCS", {"start": v(-10.23, -24.04) * mm, "mid": v(-9.74, -23.71) * mm, "end": v(-9.16, -23.6) * mm});
            skLineSegment(sketch, "E610.0.MirrorCS", {"start": v(-5.4, -23.6) * mm, "end": v(-9.16, -23.6) * mm});
            skArc(sketch, "E611.0.MirrorCS", {"start": v(-4.35, -24.04) * mm, "mid": v(-4.83, -23.71) * mm, "end": v(-5.4, -23.6) * mm});
            skLineSegment(sketch, "E612.0.MirrorCS", {"start": v(-2.06, -26.32) * mm, "end": v(-4.35, -24.04) * mm});
            skArc(sketch, "E613.0.MirrorCS", {"start": v(-2.84, -28.2) * mm, "mid": v(-1.83, -27.52) * mm, "end": v(-2.06, -26.32) * mm});
            skLineSegment(sketch, "E614.0.MirrorCS", {"start": v(-2.84, -28.2) * mm, "end": v(-4.54, -28.2) * mm});
            skArc(sketch, "E615.0.MirrorCS", {"start": v(-4.79, -28.45) * mm, "mid": v(-4.71, -28.27) * mm, "end": v(-4.54, -28.2) * mm});
            skLineSegment(sketch, "E616.0.MirrorCS", {"start": v(-4.79, -29.5) * mm, "end": v(-4.79, -28.45) * mm});
            skArc(sketch, "E617.0.MirrorCS", {"start": v(-4.29, -30) * mm, "mid": v(-4.64, -29.85) * mm, "end": v(-4.79, -29.5) * mm});
            skLineSegment(sketch, "E618.0.MirrorCS", {"start": v(-4.29, -30) * mm, "end": v(9.71, -30) * mm});
            skArc(sketch, "E619.0.MirrorCS", {"start": v(9.71, -30) * mm, "mid": v(10.07, -29.85) * mm, "end": v(10.21, -29.5) * mm});
            skLineSegment(sketch, "E620.0.MirrorCS", {"start": v(10.21, -28.45) * mm, "end": v(10.21, -29.5) * mm});
            skArc(sketch, "E621.0.MirrorCS", {"start": v(9.96, -28.2) * mm, "mid": v(10.14, -28.27) * mm, "end": v(10.21, -28.45) * mm});
            skLineSegment(sketch, "E622.0.MirrorCS", {"start": v(8.27, -28.2) * mm, "end": v(9.96, -28.2) * mm});
            skArc(sketch, "E623.0.MirrorCS", {"start": v(7.5, -26.32) * mm, "mid": v(7.25, -27.52) * mm, "end": v(8.27, -28.2) * mm});
            skLineSegment(sketch, "E624.0.MirrorCS", {"start": v(9.77, -24.04) * mm, "end": v(7.5, -26.32) * mm});
            skArc(sketch, "E625.0.MirrorCS", {"start": v(10.84, -23.6) * mm, "mid": v(10.26, -23.71) * mm, "end": v(9.77, -24.04) * mm});
            skLineSegment(sketch, "E626.0.MirrorCS", {"start": v(14.6, -23.6) * mm, "end": v(10.84, -23.6) * mm});
            skArc(sketch, "E627.0.MirrorCS", {"start": v(15.65, -24.04) * mm, "mid": v(15.17, -23.71) * mm, "end": v(14.6, -23.6) * mm});
            skLineSegment(sketch, "E628.0.MirrorCS", {"start": v(17.94, -26.32) * mm, "end": v(15.65, -24.04) * mm});
            skArc(sketch, "E629.0.MirrorCS", {"start": v(17.16, -28.2) * mm, "mid": v(18.17, -27.52) * mm, "end": v(17.94, -26.32) * mm});
            skLineSegment(sketch, "E630.0.MirrorCS", {"start": v(15.46, -28.2) * mm, "end": v(17.16, -28.2) * mm});
            skArc(sketch, "E631.0.MirrorCS", {"start": v(15.46, -28.2) * mm, "mid": v(15.29, -28.27) * mm, "end": v(15.21, -28.45) * mm});
            skLineSegment(sketch, "E632.0.MirrorCS", {"start": v(15.21, -29.5) * mm, "end": v(15.21, -28.45) * mm});
            skArc(sketch, "E633.0.MirrorCS", {"start": v(15.71, -30) * mm, "mid": v(15.36, -29.85) * mm, "end": v(15.21, -29.5) * mm});
            skLineSegment(sketch, "E634.0.MirrorCS", {"start": v(21.21, -30) * mm, "end": v(15.71, -30) * mm});
            skArc(sketch, "E635.0.MirrorCS", {"start": v(21.21, -30) * mm, "mid": v(22.27, -29.56) * mm, "end": v(22.71, -28.5) * mm});
            skLineSegment(sketch, "E636.0.MirrorCS", {"start": v(22.71, -23) * mm, "end": v(22.71, -28.5) * mm});
            skArc(sketch, "E637.0.MirrorCS", {"start": v(22.21, -22.5) * mm, "mid": v(22.57, -22.64) * mm, "end": v(22.71, -23) * mm});
            skLineSegment(sketch, "E638.0.MirrorCS", {"start": v(21.16, -22.5) * mm, "end": v(22.21, -22.5) * mm});
            skArc(sketch, "E639.0.MirrorCS", {"start": v(21.16, -22.5) * mm, "mid": v(20.99, -22.57) * mm, "end": v(20.91, -22.75) * mm});
            skLineSegment(sketch, "E640.0.MirrorCS", {"start": v(20.91, -24.44) * mm, "end": v(20.91, -22.75) * mm});
            skArc(sketch, "E641.0.MirrorCS", {"start": v(19.04, -25.22) * mm, "mid": v(20.23, -25.46) * mm, "end": v(20.91, -24.44) * mm});
            skLineSegment(sketch, "E642.0.MirrorCS", {"start": v(16.75, -22.94) * mm, "end": v(19.04, -25.22) * mm});
            skArc(sketch, "E643.0.MirrorCS", {"start": v(16.31, -21.88) * mm, "mid": v(16.43, -22.45) * mm, "end": v(16.75, -22.94) * mm});
            skLineSegment(sketch, "E644.0.MirrorCS", {"start": v(16.31, -18.12) * mm, "end": v(16.31, -21.88) * mm});
            skArc(sketch, "E645.0.MirrorCS", {"start": v(16.75, -17.06) * mm, "mid": v(16.43, -17.55) * mm, "end": v(16.31, -18.12) * mm});
            skLineSegment(sketch, "E646.0.MirrorCS", {"start": v(16.75, -17.06) * mm, "end": v(19.04, -14.78) * mm});
            skArc(sketch, "E647.0.MirrorCS", {"start": v(20.91, -15.55) * mm, "mid": v(20.23, -14.54) * mm, "end": v(19.04, -14.78) * mm});
            skLineSegment(sketch, "E648.0.MirrorCS", {"start": v(20.91, -17.25) * mm, "end": v(20.91, -15.55) * mm});
            skArc(sketch, "E649.0.MirrorCS", {"start": v(20.91, -17.25) * mm, "mid": v(20.99, -17.42) * mm, "end": v(21.16, -17.5) * mm});
            skLineSegment(sketch, "E650.0.MirrorCS", {"start": v(21.16, -17.5) * mm, "end": v(22.21, -17.5) * mm});
            skArc(sketch, "E651.0.MirrorCS", {"start": v(22.71, -17) * mm, "mid": v(22.57, -17.35) * mm, "end": v(22.21, -17.5) * mm});
            skCircle(sketch, "E652.0.MirrorC", {"center": v(12.71, -20) * mm, "radius": 2.15 * mm});
            skCircle(sketch, "E653.0.MirrorC", {"center": v(-7.29, -20) * mm, "radius": 2.15 * mm});
            skArc(sketch, "E654.0.MirrorCS", {"start": v(-3.25, -22.94) * mm, "mid": v(-3.57, -22.45) * mm, "end": v(-3.69, -21.88) * mm});
            skLineSegment(sketch, "E655.0.MirrorCS", {"start": v(-3.25, -22.94) * mm, "end": v(1.57, -27.76) * mm});
            skArc(sketch, "E656.0.MirrorCS", {"start": v(2.64, -28.2) * mm, "mid": v(2.06, -28.08) * mm, "end": v(1.57, -27.76) * mm});
            skLineSegment(sketch, "E657.0.MirrorCS", {"start": v(2.8, -28.2) * mm, "end": v(2.64, -28.2) * mm});
            skArc(sketch, "E658.0.MirrorCS", {"start": v(3.85, -27.76) * mm, "mid": v(3.37, -28.08) * mm, "end": v(2.8, -28.2) * mm});
            skLineSegment(sketch, "E659.0.MirrorCS", {"start": v(3.85, -27.76) * mm, "end": v(8.67, -22.94) * mm});
            skArc(sketch, "E660.0.MirrorCS", {"start": v(9.11, -21.88) * mm, "mid": v(9, -22.45) * mm, "end": v(8.67, -22.94) * mm});
            skArc(sketch, "E661.0.MirrorCS", {"start": v(14.6, -16.4) * mm, "mid": v(15.17, -16.28) * mm, "end": v(15.65, -15.96) * mm});
            skLineSegment(sketch, "E662.0.MirrorCS", {"start": v(14.6, -16.4) * mm, "end": v(10.84, -16.4) * mm});
            skLineSegment(sketch, "E663.0.MirrorCS", {"start": v(9.11, -21.88) * mm, "end": v(9.11, -18.12) * mm});
            skLineSegment(sketch, "E664.0.MirrorCS", {"start": v(-3.69, -21.88) * mm, "end": v(-3.69, -18.12) * mm});
            skLineSegment(sketch, "E665.0.MirrorCS", {"start": v(-9.16, -16.4) * mm, "end": v(-5.4, -16.4) * mm});
            skArc(sketch, "E666.0.MirrorCS", {"start": v(-9.16, -16.4) * mm, "mid": v(-9.74, -16.28) * mm, "end": v(-10.23, -15.96) * mm});
            skLineSegment(sketch, "E667.0.MirrorCS", {"start": v(-15.05, -8.86) * mm, "end": v(-10.23, -4.04) * mm});
            skArc(sketch, "E668.0.MirrorCS", {"start": v(-15.49, -9.92) * mm, "mid": v(-15.37, -9.35) * mm, "end": v(-15.05, -8.86) * mm});
            skLineSegment(sketch, "E669.0.MirrorCS", {"start": v(-15.49, -10.08) * mm, "end": v(-15.49, -9.92) * mm});
            skArc(sketch, "E670.0.MirrorCS", {"start": v(-15.05, -11.14) * mm, "mid": v(-15.37, -10.65) * mm, "end": v(-15.49, -10.08) * mm});
            skLineSegment(sketch, "E671.0.MirrorCS", {"start": v(-15.05, -11.14) * mm, "end": v(-10.23, -15.96) * mm});
            skLineSegment(sketch, "E672", {"start": v(2.71, -10) * mm, "end": v(21.21, 8.5) * mm, "construction": true});
            skLineSegment(sketch, "E673.0.MirrorCS", {"start": v(20.47, -8.86) * mm, "end": v(15.65, -4.04) * mm});
            skArc(sketch, "E674.0.MirrorCS", {"start": v(20.47, -8.86) * mm, "mid": v(20.8, -9.35) * mm, "end": v(20.91, -9.92) * mm});
            skLineSegment(sketch, "E675.0.MirrorCS", {"start": v(20.91, -9.92) * mm, "end": v(20.91, -10.08) * mm});
            skArc(sketch, "E676.0.MirrorCS", {"start": v(20.91, -10.08) * mm, "mid": v(20.8, -10.65) * mm, "end": v(20.47, -11.14) * mm});
            skLineSegment(sketch, "E677.0.MirrorCS", {"start": v(20.47, -11.14) * mm, "end": v(15.65, -15.96) * mm});
            skLineSegment(sketch, "E678", {"start": v(-5.4, -3.6) * mm, "end": v(-3.69, -1.88) * mm});
            skLineSegment(sketch, "E679", {"start": v(9.11, -1.88) * mm, "end": v(10.84, -3.6) * mm});
            skLineSegment(sketch, "E680", {"start": v(-3.69, -18.12) * mm, "end": v(-5.4, -16.4) * mm});
            skLineSegment(sketch, "E681", {"start": v(10.84, -16.4) * mm, "end": v(9.11, -18.12) * mm});
            skLineSegment(sketch, "E682", {"start": v(-17.29, -3) * mm, "end": v(-17.29, -17) * mm});
            skLineSegment(sketch, "E683", {"start": v(22.71, -3) * mm, "end": v(22.71, -17) * mm});
            skSolve(sketch);
        }
        {
            var Q0;
            Q0=qCreatedBy(makeId("Front.planeOp"),FACE);
            var sketch = newSketch(context, id + "F7", { "sketchPlane" : qUnion([Q0])});
            skLineSegment(sketch, "E684.0.0", {"start": v(-10.29, 10) * mm, "end": v(-15.79, 10) * mm});
            skArc(sketch, "E684.0.1", {"start": v(-15.79, 10) * mm, "mid": v(-16.85, 9.56) * mm, "end": v(-17.29, 8.5) * mm});
            skLineSegment(sketch, "E684.0.2", {"start": v(-17.29, 8.5) * mm, "end": v(-17.29, 3) * mm});
            skArc(sketch, "E684.0.3", {"start": v(-17.29, 3) * mm, "mid": v(-17.14, 2.65) * mm, "end": v(-16.79, 2.5) * mm});
            skLineSegment(sketch, "E684.0.4", {"start": v(-16.79, 2.5) * mm, "end": v(-15.74, 2.5) * mm});
            skArc(sketch, "E684.0.5", {"start": v(-15.74, 2.5) * mm, "mid": v(-15.56, 2.58) * mm, "end": v(-15.49, 2.75) * mm});
            skLineSegment(sketch, "E684.0.6", {"start": v(-15.49, 2.75) * mm, "end": v(-15.49, 4.45) * mm});
            skArc(sketch, "E684.0.7", {"start": v(-15.49, 4.45) * mm, "mid": v(-14.8, 5.46) * mm, "end": v(-13.6, 5.22) * mm});
            skLineSegment(sketch, "E684.0.8", {"start": v(-13.6, 5.22) * mm, "end": v(-11.33, 2.94) * mm});
            skArc(sketch, "E684.0.9", {"start": v(-11.33, 2.94) * mm, "mid": v(-11, 2.45) * mm, "end": v(-10.89, 1.88) * mm});
            skLineSegment(sketch, "E684.0.10", {"start": v(-10.89, 1.88) * mm, "end": v(-10.89, -1.88) * mm});
            skArc(sketch, "E684.0.11", {"start": v(-10.89, -1.88) * mm, "mid": v(-11, -2.45) * mm, "end": v(-11.33, -2.94) * mm});
            skLineSegment(sketch, "E684.0.12", {"start": v(-11.33, -2.94) * mm, "end": v(-13.6, -5.22) * mm});
            skArc(sketch, "E684.0.13", {"start": v(-13.6, -5.22) * mm, "mid": v(-14.8, -5.46) * mm, "end": v(-15.49, -4.44) * mm});
            skLineSegment(sketch, "E684.0.14", {"start": v(-15.49, -4.44) * mm, "end": v(-15.49, -2.75) * mm});
            skArc(sketch, "E684.0.15", {"start": v(-15.49, -2.75) * mm, "mid": v(-15.56, -2.57) * mm, "end": v(-15.74, -2.5) * mm});
            skLineSegment(sketch, "E684.0.16", {"start": v(-15.74, -2.5) * mm, "end": v(-16.79, -2.5) * mm});
            skArc(sketch, "E684.0.17", {"start": v(-16.79, -2.5) * mm, "mid": v(-17.14, -2.64) * mm, "end": v(-17.29, -3) * mm});
            skLineSegment(sketch, "E684.0.18", {"start": v(-17.29, -3) * mm, "end": v(-17.29, -17) * mm});
            skArc(sketch, "E684.0.19", {"start": v(-17.29, -17) * mm, "mid": v(-17.14, -17.35) * mm, "end": v(-16.79, -17.5) * mm});
            skLineSegment(sketch, "E684.0.20", {"start": v(-16.79, -17.5) * mm, "end": v(-15.74, -17.5) * mm});
            skArc(sketch, "E684.0.21", {"start": v(-15.74, -17.5) * mm, "mid": v(-15.56, -17.42) * mm, "end": v(-15.49, -17.25) * mm});
            skLineSegment(sketch, "E684.0.22", {"start": v(-15.49, -17.25) * mm, "end": v(-15.49, -15.55) * mm});
            skArc(sketch, "E684.0.23", {"start": v(-15.49, -15.55) * mm, "mid": v(-14.8, -14.54) * mm, "end": v(-13.6, -14.78) * mm});
            skLineSegment(sketch, "E684.0.24", {"start": v(-13.6, -14.78) * mm, "end": v(-11.33, -17.06) * mm});
            skArc(sketch, "E684.0.25", {"start": v(-11.33, -17.06) * mm, "mid": v(-11, -17.55) * mm, "end": v(-10.89, -18.12) * mm});
            skLineSegment(sketch, "E684.0.26", {"start": v(-10.89, -18.12) * mm, "end": v(-10.89, -21.88) * mm});
            skArc(sketch, "E684.0.27", {"start": v(-10.89, -21.88) * mm, "mid": v(-11, -22.45) * mm, "end": v(-11.33, -22.94) * mm});
            skLineSegment(sketch, "E684.0.28", {"start": v(-11.33, -22.94) * mm, "end": v(-13.6, -25.22) * mm});
            skArc(sketch, "E684.0.29", {"start": v(-13.6, -25.22) * mm, "mid": v(-14.8, -25.46) * mm, "end": v(-15.49, -24.44) * mm});
            skLineSegment(sketch, "E684.0.30", {"start": v(-15.49, -24.44) * mm, "end": v(-15.49, -22.75) * mm});
            skArc(sketch, "E684.0.31", {"start": v(-15.49, -22.75) * mm, "mid": v(-15.56, -22.57) * mm, "end": v(-15.74, -22.5) * mm});
            skLineSegment(sketch, "E684.0.32", {"start": v(-15.74, -22.5) * mm, "end": v(-16.79, -22.5) * mm});
            skArc(sketch, "E684.0.33", {"start": v(-16.79, -22.5) * mm, "mid": v(-17.14, -22.64) * mm, "end": v(-17.29, -23) * mm});
            skLineSegment(sketch, "E684.0.34", {"start": v(-17.29, -23) * mm, "end": v(-17.29, -28.5) * mm});
            skArc(sketch, "E684.0.35", {"start": v(-17.29, -28.5) * mm, "mid": v(-16.85, -29.56) * mm, "end": v(-15.79, -30) * mm});
            skLineSegment(sketch, "E684.0.36", {"start": v(-15.79, -30) * mm, "end": v(-10.29, -30) * mm});
            skArc(sketch, "E684.0.37", {"start": v(-10.29, -30) * mm, "mid": v(-9.93, -29.85) * mm, "end": v(-9.79, -29.5) * mm});
            skLineSegment(sketch, "E684.0.38", {"start": v(-9.79, -29.5) * mm, "end": v(-9.79, -28.45) * mm});
            skArc(sketch, "E684.0.39", {"start": v(-9.79, -28.45) * mm, "mid": v(-9.86, -28.27) * mm, "end": v(-10.04, -28.2) * mm});
            skLineSegment(sketch, "E684.0.40", {"start": v(-10.04, -28.2) * mm, "end": v(-11.73, -28.2) * mm});
            skArc(sketch, "E684.0.41", {"start": v(-11.73, -28.2) * mm, "mid": v(-12.75, -27.52) * mm, "end": v(-12.5, -26.32) * mm});
            skLineSegment(sketch, "E684.0.42", {"start": v(-12.5, -26.32) * mm, "end": v(-10.23, -24.04) * mm});
            skArc(sketch, "E684.0.43", {"start": v(-10.23, -24.04) * mm, "mid": v(-9.74, -23.71) * mm, "end": v(-9.16, -23.6) * mm});
            skLineSegment(sketch, "E684.0.44", {"start": v(-9.16, -23.6) * mm, "end": v(-5.4, -23.6) * mm});
            skArc(sketch, "E684.0.45", {"start": v(-5.4, -23.6) * mm, "mid": v(-4.83, -23.71) * mm, "end": v(-4.35, -24.04) * mm});
            skLineSegment(sketch, "E684.0.46", {"start": v(-4.35, -24.04) * mm, "end": v(-2.06, -26.32) * mm});
            skArc(sketch, "E684.0.47", {"start": v(-2.06, -26.32) * mm, "mid": v(-1.83, -27.52) * mm, "end": v(-2.84, -28.2) * mm});
            skLineSegment(sketch, "E684.0.48", {"start": v(-2.84, -28.2) * mm, "end": v(-4.54, -28.2) * mm});
            skArc(sketch, "E684.0.49", {"start": v(-4.54, -28.2) * mm, "mid": v(-4.71, -28.27) * mm, "end": v(-4.79, -28.45) * mm});
            skLineSegment(sketch, "E684.0.50", {"start": v(-4.79, -28.45) * mm, "end": v(-4.79, -29.5) * mm});
            skArc(sketch, "E684.0.51", {"start": v(-4.79, -29.5) * mm, "mid": v(-4.64, -29.85) * mm, "end": v(-4.29, -30) * mm});
            skLineSegment(sketch, "E684.0.52", {"start": v(-4.29, -30) * mm, "end": v(9.71, -30) * mm});
            skArc(sketch, "E684.0.53", {"start": v(9.71, -30) * mm, "mid": v(10.07, -29.85) * mm, "end": v(10.21, -29.5) * mm});
            skLineSegment(sketch, "E684.0.54", {"start": v(10.21, -29.5) * mm, "end": v(10.21, -28.45) * mm});
            skArc(sketch, "E684.0.55", {"start": v(10.21, -28.45) * mm, "mid": v(10.14, -28.27) * mm, "end": v(9.96, -28.2) * mm});
            skLineSegment(sketch, "E684.0.56", {"start": v(9.96, -28.2) * mm, "end": v(8.27, -28.2) * mm});
            skArc(sketch, "E684.0.57", {"start": v(8.27, -28.2) * mm, "mid": v(7.25, -27.52) * mm, "end": v(7.5, -26.32) * mm});
            skLineSegment(sketch, "E684.0.58", {"start": v(7.5, -26.32) * mm, "end": v(9.77, -24.04) * mm});
            skArc(sketch, "E684.0.59", {"start": v(9.77, -24.04) * mm, "mid": v(10.26, -23.71) * mm, "end": v(10.84, -23.6) * mm});
            skLineSegment(sketch, "E684.0.60", {"start": v(10.84, -23.6) * mm, "end": v(14.6, -23.6) * mm});
            skArc(sketch, "E684.0.61", {"start": v(14.6, -23.6) * mm, "mid": v(15.17, -23.71) * mm, "end": v(15.65, -24.04) * mm});
            skLineSegment(sketch, "E684.0.62", {"start": v(15.65, -24.04) * mm, "end": v(17.94, -26.32) * mm});
            skArc(sketch, "E684.0.63", {"start": v(17.94, -26.32) * mm, "mid": v(18.17, -27.52) * mm, "end": v(17.16, -28.2) * mm});
            skLineSegment(sketch, "E684.0.64", {"start": v(17.16, -28.2) * mm, "end": v(15.46, -28.2) * mm});
            skArc(sketch, "E684.0.65", {"start": v(15.46, -28.2) * mm, "mid": v(15.29, -28.27) * mm, "end": v(15.21, -28.45) * mm});
            skLineSegment(sketch, "E684.0.66", {"start": v(15.21, -28.45) * mm, "end": v(15.21, -29.5) * mm});
            skArc(sketch, "E684.0.67", {"start": v(15.21, -29.5) * mm, "mid": v(15.36, -29.85) * mm, "end": v(15.71, -30) * mm});
            skArc(sketch, "E684.0.77", {"start": v(16.75, -22.94) * mm, "mid": v(16.43, -22.45) * mm, "end": v(16.31, -21.88) * mm});
            skLineSegment(sketch, "E684.0.78", {"start": v(16.31, -21.88) * mm, "end": v(16.31, -18.12) * mm});
            skArc(sketch, "E684.0.79", {"start": v(16.31, -18.12) * mm, "mid": v(16.43, -17.55) * mm, "end": v(16.75, -17.06) * mm});
            skArc(sketch, "E684.0.93", {"start": v(16.75, -2.94) * mm, "mid": v(16.43, -2.45) * mm, "end": v(16.31, -1.88) * mm});
            skLineSegment(sketch, "E684.0.94", {"start": v(16.31, -1.88) * mm, "end": v(16.31, 1.88) * mm});
            skArc(sketch, "E684.0.95", {"start": v(16.31, 1.88) * mm, "mid": v(16.43, 2.45) * mm, "end": v(16.75, 2.94) * mm});
            skArc(sketch, "E684.0.105", {"start": v(15.71, 10) * mm, "mid": v(15.36, 9.86) * mm, "end": v(15.21, 9.5) * mm});
            skLineSegment(sketch, "E684.0.106", {"start": v(15.21, 9.5) * mm, "end": v(15.21, 8.45) * mm});
            skArc(sketch, "E684.0.107", {"start": v(15.21, 8.45) * mm, "mid": v(15.29, 8.28) * mm, "end": v(15.46, 8.2) * mm});
            skLineSegment(sketch, "E684.0.108", {"start": v(15.46, 8.2) * mm, "end": v(17.16, 8.2) * mm});
            skArc(sketch, "E684.0.109", {"start": v(17.16, 8.2) * mm, "mid": v(18.17, 7.52) * mm, "end": v(17.94, 6.32) * mm});
            skLineSegment(sketch, "E684.0.110", {"start": v(17.94, 6.32) * mm, "end": v(15.65, 4.04) * mm});
            skArc(sketch, "E684.0.111", {"start": v(15.65, 4.04) * mm, "mid": v(15.17, 3.72) * mm, "end": v(14.6, 3.6) * mm});
            skLineSegment(sketch, "E684.0.112", {"start": v(14.6, 3.6) * mm, "end": v(10.84, 3.6) * mm});
            skArc(sketch, "E684.0.113", {"start": v(10.84, 3.6) * mm, "mid": v(10.26, 3.72) * mm, "end": v(9.77, 4.04) * mm});
            skLineSegment(sketch, "E684.0.114", {"start": v(9.77, 4.04) * mm, "end": v(7.5, 6.32) * mm});
            skArc(sketch, "E684.0.115", {"start": v(7.5, 6.32) * mm, "mid": v(7.25, 7.52) * mm, "end": v(8.27, 8.2) * mm});
            skLineSegment(sketch, "E684.0.116", {"start": v(8.27, 8.2) * mm, "end": v(9.96, 8.2) * mm});
            skArc(sketch, "E684.0.117", {"start": v(9.96, 8.2) * mm, "mid": v(10.14, 8.28) * mm, "end": v(10.21, 8.45) * mm});
            skLineSegment(sketch, "E684.0.118", {"start": v(10.21, 8.45) * mm, "end": v(10.21, 9.5) * mm});
            skArc(sketch, "E684.0.119", {"start": v(10.21, 9.5) * mm, "mid": v(10.07, 9.86) * mm, "end": v(9.71, 10) * mm});
            skLineSegment(sketch, "E684.0.120", {"start": v(9.71, 10) * mm, "end": v(-4.29, 10) * mm});
            skArc(sketch, "E684.0.121", {"start": v(-4.29, 10) * mm, "mid": v(-4.64, 9.86) * mm, "end": v(-4.79, 9.5) * mm});
            skLineSegment(sketch, "E684.0.122", {"start": v(-4.79, 9.5) * mm, "end": v(-4.79, 8.45) * mm});
            skArc(sketch, "E684.0.123", {"start": v(-4.79, 8.45) * mm, "mid": v(-4.71, 8.28) * mm, "end": v(-4.54, 8.2) * mm});
            skLineSegment(sketch, "E684.0.124", {"start": v(-4.54, 8.2) * mm, "end": v(-2.84, 8.2) * mm});
            skArc(sketch, "E684.0.125", {"start": v(-2.84, 8.2) * mm, "mid": v(-1.83, 7.52) * mm, "end": v(-2.06, 6.32) * mm});
            skLineSegment(sketch, "E684.0.126", {"start": v(-2.06, 6.32) * mm, "end": v(-4.35, 4.04) * mm});
            skArc(sketch, "E684.0.127", {"start": v(-4.35, 4.04) * mm, "mid": v(-4.83, 3.72) * mm, "end": v(-5.4, 3.6) * mm});
            skLineSegment(sketch, "E684.0.128", {"start": v(-5.4, 3.6) * mm, "end": v(-9.16, 3.6) * mm});
            skArc(sketch, "E684.0.129", {"start": v(-9.16, 3.6) * mm, "mid": v(-9.74, 3.72) * mm, "end": v(-10.23, 4.04) * mm});
            skLineSegment(sketch, "E684.0.130", {"start": v(-10.23, 4.04) * mm, "end": v(-12.5, 6.32) * mm});
            skArc(sketch, "E684.0.131", {"start": v(-12.5, 6.32) * mm, "mid": v(-12.75, 7.52) * mm, "end": v(-11.73, 8.2) * mm});
            skLineSegment(sketch, "E684.0.132", {"start": v(-11.73, 8.2) * mm, "end": v(-10.04, 8.2) * mm});
            skArc(sketch, "E684.0.133", {"start": v(-10.04, 8.2) * mm, "mid": v(-9.86, 8.28) * mm, "end": v(-9.79, 8.45) * mm});
            skLineSegment(sketch, "E684.0.134", {"start": v(-9.79, 8.45) * mm, "end": v(-9.79, 9.5) * mm});
            skArc(sketch, "E684.0.135", {"start": v(-9.79, 9.5) * mm, "mid": v(-9.93, 9.86) * mm, "end": v(-10.29, 10) * mm});
            skLineSegment(sketch, "E685.0.0", {"start": v(-5.4, -3.6) * mm, "end": v(-9.16, -3.6) * mm});
            skArc(sketch, "E685.0.1", {"start": v(-9.16, -3.6) * mm, "mid": v(-9.74, -3.71) * mm, "end": v(-10.23, -4.04) * mm});
            skLineSegment(sketch, "E685.0.2", {"start": v(-10.23, -4.04) * mm, "end": v(-15.05, -8.86) * mm});
            skArc(sketch, "E685.0.3", {"start": v(-15.05, -8.86) * mm, "mid": v(-15.37, -9.35) * mm, "end": v(-15.49, -9.92) * mm});
            skLineSegment(sketch, "E685.0.4", {"start": v(-15.49, -9.92) * mm, "end": v(-15.49, -10.08) * mm});
            skArc(sketch, "E685.0.5", {"start": v(-15.49, -10.08) * mm, "mid": v(-15.37, -10.65) * mm, "end": v(-15.05, -11.14) * mm});
            skLineSegment(sketch, "E685.0.6", {"start": v(-15.05, -11.14) * mm, "end": v(-10.23, -15.96) * mm});
            skArc(sketch, "E685.0.7", {"start": v(-10.23, -15.96) * mm, "mid": v(-9.74, -16.28) * mm, "end": v(-9.16, -16.4) * mm});
            skLineSegment(sketch, "E685.0.8", {"start": v(-9.16, -16.4) * mm, "end": v(-5.4, -16.4) * mm});
            skLineSegment(sketch, "E685.0.9", {"start": v(-5.4, -16.4) * mm, "end": v(-3.69, -18.12) * mm});
            skLineSegment(sketch, "E685.0.10", {"start": v(-3.69, -18.12) * mm, "end": v(-3.69, -21.88) * mm});
            skArc(sketch, "E685.0.11", {"start": v(-3.69, -21.88) * mm, "mid": v(-3.57, -22.45) * mm, "end": v(-3.25, -22.94) * mm});
            skLineSegment(sketch, "E685.0.12", {"start": v(-3.25, -22.94) * mm, "end": v(1.57, -27.76) * mm});
            skArc(sketch, "E685.0.13", {"start": v(1.57, -27.76) * mm, "mid": v(2.06, -28.08) * mm, "end": v(2.64, -28.2) * mm});
            skLineSegment(sketch, "E685.0.14", {"start": v(2.64, -28.2) * mm, "end": v(2.8, -28.2) * mm});
            skArc(sketch, "E685.0.15", {"start": v(2.8, -28.2) * mm, "mid": v(3.37, -28.08) * mm, "end": v(3.85, -27.76) * mm});
            skLineSegment(sketch, "E685.0.16", {"start": v(3.85, -27.76) * mm, "end": v(8.67, -22.94) * mm});
            skArc(sketch, "E685.0.17", {"start": v(8.67, -22.94) * mm, "mid": v(9, -22.45) * mm, "end": v(9.11, -21.88) * mm});
            skLineSegment(sketch, "E685.0.18", {"start": v(9.11, -21.88) * mm, "end": v(9.11, -18.12) * mm});
            skLineSegment(sketch, "E685.0.19", {"start": v(9.11, -18.12) * mm, "end": v(10.84, -16.4) * mm});
            skLineSegment(sketch, "E685.0.20", {"start": v(10.84, -16.4) * mm, "end": v(14.6, -16.4) * mm});
            skArc(sketch, "E685.0.21", {"start": v(14.6, -16.4) * mm, "mid": v(15.17, -16.28) * mm, "end": v(15.65, -15.96) * mm});
            skLineSegment(sketch, "E685.0.22", {"start": v(15.65, -15.96) * mm, "end": v(20.47, -11.14) * mm});
            skArc(sketch, "E685.0.23", {"start": v(20.47, -11.14) * mm, "mid": v(20.8, -10.65) * mm, "end": v(20.91, -10.08) * mm});
            skLineSegment(sketch, "E685.0.24", {"start": v(20.91, -10.08) * mm, "end": v(20.91, -9.92) * mm});
            skArc(sketch, "E685.0.25", {"start": v(20.91, -9.92) * mm, "mid": v(20.8, -9.35) * mm, "end": v(20.47, -8.86) * mm});
            skLineSegment(sketch, "E685.0.26", {"start": v(20.47, -8.86) * mm, "end": v(15.65, -4.04) * mm});
            skArc(sketch, "E685.0.27", {"start": v(15.65, -4.04) * mm, "mid": v(15.17, -3.71) * mm, "end": v(14.6, -3.6) * mm});
            skLineSegment(sketch, "E685.0.28", {"start": v(14.6, -3.6) * mm, "end": v(10.84, -3.6) * mm});
            skLineSegment(sketch, "E685.0.29", {"start": v(10.84, -3.6) * mm, "end": v(9.11, -1.88) * mm});
            skLineSegment(sketch, "E685.0.30", {"start": v(9.11, -1.88) * mm, "end": v(9.11, 1.88) * mm});
            skArc(sketch, "E685.0.31", {"start": v(9.11, 1.88) * mm, "mid": v(9, 2.45) * mm, "end": v(8.67, 2.94) * mm});
            skLineSegment(sketch, "E685.0.32", {"start": v(8.67, 2.94) * mm, "end": v(3.85, 7.76) * mm});
            skArc(sketch, "E685.0.33", {"start": v(3.85, 7.76) * mm, "mid": v(3.37, 8.09) * mm, "end": v(2.8, 8.2) * mm});
            skLineSegment(sketch, "E685.0.34", {"start": v(2.8, 8.2) * mm, "end": v(2.64, 8.2) * mm});
            skArc(sketch, "E685.0.35", {"start": v(2.64, 8.2) * mm, "mid": v(2.06, 8.09) * mm, "end": v(1.57, 7.76) * mm});
            skLineSegment(sketch, "E685.0.36", {"start": v(1.57, 7.76) * mm, "end": v(-3.25, 2.94) * mm});
            skArc(sketch, "E685.0.37", {"start": v(-3.25, 2.94) * mm, "mid": v(-3.57, 2.45) * mm, "end": v(-3.69, 1.88) * mm});
            skLineSegment(sketch, "E685.0.38", {"start": v(-3.69, 1.88) * mm, "end": v(-3.69, -1.88) * mm});
            skLineSegment(sketch, "E685.0.39", {"start": v(-3.69, -1.88) * mm, "end": v(-5.4, -3.6) * mm});
            skCircle(sketch, "E686.0", {"center": v(-7.29, 0) * mm, "radius": 2.15 * mm});
            skCircle(sketch, "E687.0", {"center": v(12.71, 0) * mm, "radius": 2.15 * mm});
            skCircle(sketch, "E688.0", {"center": v(12.71, -20) * mm, "radius": 2.15 * mm});
            skCircle(sketch, "E689.0", {"center": v(-7.29, -20) * mm, "radius": 2.15 * mm});
            skLineSegment(sketch, "E690.0", {"start": v(-19.41, -10) * mm, "end": v(25.27, -10) * mm, "construction": true});
            skLineSegment(sketch, "E691.0", {"start": v(-15.79, 8.5) * mm, "end": v(6.66, -13.95) * mm, "construction": true});
            skLineSegment(sketch, "E692.0", {"start": v(2.71, -10) * mm, "end": v(21.21, 8.5) * mm, "construction": true});
            skLineSegment(sketch, "E693", {"start": v(12.71, 12.48) * mm, "end": v(12.71, -32.12) * mm, "construction": true});
            skLineSegment(sketch, "E694.0.MirrorCS", {"start": v(16.75, 2.94) * mm, "end": v(21.57, 7.76) * mm});
            skLineSegment(sketch, "E695.0.MirrorCS", {"start": v(15.71, 10) * mm, "end": v(29.71, 10) * mm});
            skLineSegment(sketch, "E696.0.MirrorCS", {"start": v(21.57, -27.76) * mm, "end": v(16.75, -22.94) * mm});
            skLineSegment(sketch, "E697.0.MirrorCS", {"start": v(29.71, -30) * mm, "end": v(15.71, -30) * mm});
            skArc(sketch, "E698.0.MirrorCS", {"start": v(29.71, 10) * mm, "mid": v(30.07, 9.86) * mm, "end": v(30.21, 9.5) * mm});
            skLineSegment(sketch, "E699.0.MirrorCS", {"start": v(30.21, 9.5) * mm, "end": v(30.21, 8.45) * mm});
            skArc(sketch, "E700.0.MirrorCS", {"start": v(30.21, 8.45) * mm, "mid": v(30.14, 8.28) * mm, "end": v(29.96, 8.2) * mm});
            skLineSegment(sketch, "E701.0.MirrorCS", {"start": v(29.96, 8.2) * mm, "end": v(28.27, 8.2) * mm});
            skArc(sketch, "E702.0.MirrorCS", {"start": v(28.27, 8.2) * mm, "mid": v(27.25, 7.52) * mm, "end": v(27.5, 6.32) * mm});
            skLineSegment(sketch, "E703.0.MirrorCS", {"start": v(27.5, 6.32) * mm, "end": v(29.77, 4.04) * mm});
            skArc(sketch, "E704.0.MirrorCS", {"start": v(29.77, 4.04) * mm, "mid": v(30.26, 3.72) * mm, "end": v(30.84, 3.6) * mm});
            skLineSegment(sketch, "E705.0.MirrorCS", {"start": v(30.84, 3.6) * mm, "end": v(34.6, 3.6) * mm});
            skArc(sketch, "E706.0.MirrorCS", {"start": v(34.6, 3.6) * mm, "mid": v(35.17, 3.72) * mm, "end": v(35.65, 4.04) * mm});
            skLineSegment(sketch, "E707.0.MirrorCS", {"start": v(35.65, 4.04) * mm, "end": v(37.94, 6.32) * mm});
            skArc(sketch, "E708.0.MirrorCS", {"start": v(37.94, 6.32) * mm, "mid": v(38.17, 7.52) * mm, "end": v(37.16, 8.2) * mm});
            skLineSegment(sketch, "E709.0.MirrorCS", {"start": v(37.16, 8.2) * mm, "end": v(35.46, 8.2) * mm});
            skArc(sketch, "E710.0.MirrorCS", {"start": v(35.46, 8.2) * mm, "mid": v(35.29, 8.28) * mm, "end": v(35.21, 8.45) * mm});
            skLineSegment(sketch, "E711.0.MirrorCS", {"start": v(35.21, 8.45) * mm, "end": v(35.21, 9.5) * mm});
            skArc(sketch, "E712.0.MirrorCS", {"start": v(35.21, 9.5) * mm, "mid": v(35.36, 9.86) * mm, "end": v(35.71, 10) * mm});
            skLineSegment(sketch, "E713.0.MirrorCS", {"start": v(35.71, 10) * mm, "end": v(41.21, 10) * mm});
            skArc(sketch, "E714.0.MirrorCS", {"start": v(41.21, 10) * mm, "mid": v(42.27, 9.56) * mm, "end": v(42.71, 8.5) * mm});
            skLineSegment(sketch, "E715.0.MirrorCS", {"start": v(42.71, 8.5) * mm, "end": v(42.71, 3) * mm});
            skArc(sketch, "E716.0.MirrorCS", {"start": v(42.71, 3) * mm, "mid": v(42.57, 2.65) * mm, "end": v(42.21, 2.5) * mm});
            skLineSegment(sketch, "E717.0.MirrorCS", {"start": v(42.21, 2.5) * mm, "end": v(41.16, 2.5) * mm});
            skArc(sketch, "E718.0.MirrorCS", {"start": v(41.16, 2.5) * mm, "mid": v(40.99, 2.58) * mm, "end": v(40.91, 2.75) * mm});
            skLineSegment(sketch, "E719.0.MirrorCS", {"start": v(40.91, 2.75) * mm, "end": v(40.91, 4.45) * mm});
            skArc(sketch, "E720.0.MirrorCS", {"start": v(40.91, 4.45) * mm, "mid": v(40.23, 5.46) * mm, "end": v(39.04, 5.22) * mm});
            skLineSegment(sketch, "E721.0.MirrorCS", {"start": v(39.04, 5.22) * mm, "end": v(36.75, 2.94) * mm});
            skArc(sketch, "E722.0.MirrorCS", {"start": v(36.75, 2.94) * mm, "mid": v(36.43, 2.45) * mm, "end": v(36.31, 1.88) * mm});
            skLineSegment(sketch, "E723.0.MirrorCS", {"start": v(36.31, 1.88) * mm, "end": v(36.31, -1.88) * mm});
            skArc(sketch, "E724.0.MirrorCS", {"start": v(36.31, -1.88) * mm, "mid": v(36.43, -2.45) * mm, "end": v(36.75, -2.94) * mm});
            skLineSegment(sketch, "E725.0.MirrorCS", {"start": v(36.75, -2.94) * mm, "end": v(39.04, -5.22) * mm});
            skArc(sketch, "E726.0.MirrorCS", {"start": v(39.04, -5.22) * mm, "mid": v(40.23, -5.46) * mm, "end": v(40.91, -4.44) * mm});
            skLineSegment(sketch, "E727.0.MirrorCS", {"start": v(40.91, -4.44) * mm, "end": v(40.91, -2.75) * mm});
            skArc(sketch, "E728.0.MirrorCS", {"start": v(40.91, -2.75) * mm, "mid": v(40.99, -2.57) * mm, "end": v(41.16, -2.5) * mm});
            skLineSegment(sketch, "E729.0.MirrorCS", {"start": v(41.16, -2.5) * mm, "end": v(42.21, -2.5) * mm});
            skArc(sketch, "E730.0.MirrorCS", {"start": v(42.21, -2.5) * mm, "mid": v(42.57, -2.64) * mm, "end": v(42.71, -3) * mm});
            skLineSegment(sketch, "E731.0.MirrorCS", {"start": v(42.71, -3) * mm, "end": v(42.71, -17) * mm});
            skArc(sketch, "E732.0.MirrorCS", {"start": v(42.71, -17) * mm, "mid": v(42.57, -17.35) * mm, "end": v(42.21, -17.5) * mm});
            skLineSegment(sketch, "E733.0.MirrorCS", {"start": v(42.21, -17.5) * mm, "end": v(41.16, -17.5) * mm});
            skArc(sketch, "E734.0.MirrorCS", {"start": v(41.16, -17.5) * mm, "mid": v(40.99, -17.42) * mm, "end": v(40.91, -17.25) * mm});
            skLineSegment(sketch, "E735.0.MirrorCS", {"start": v(40.91, -17.25) * mm, "end": v(40.91, -15.55) * mm});
            skArc(sketch, "E736.0.MirrorCS", {"start": v(40.91, -15.55) * mm, "mid": v(40.23, -14.54) * mm, "end": v(39.04, -14.78) * mm});
            skLineSegment(sketch, "E737.0.MirrorCS", {"start": v(39.04, -14.78) * mm, "end": v(36.75, -17.06) * mm});
            skArc(sketch, "E738.0.MirrorCS", {"start": v(36.75, -17.06) * mm, "mid": v(36.43, -17.55) * mm, "end": v(36.31, -18.12) * mm});
            skLineSegment(sketch, "E739.0.MirrorCS", {"start": v(36.31, -18.12) * mm, "end": v(36.31, -21.88) * mm});
            skArc(sketch, "E740.0.MirrorCS", {"start": v(36.31, -21.88) * mm, "mid": v(36.43, -22.45) * mm, "end": v(36.75, -22.94) * mm});
            skLineSegment(sketch, "E741.0.MirrorCS", {"start": v(36.75, -22.94) * mm, "end": v(39.04, -25.22) * mm});
            skArc(sketch, "E742.0.MirrorCS", {"start": v(39.04, -25.22) * mm, "mid": v(40.23, -25.46) * mm, "end": v(40.91, -24.44) * mm});
            skLineSegment(sketch, "E743.0.MirrorCS", {"start": v(40.91, -24.44) * mm, "end": v(40.91, -22.75) * mm});
            skArc(sketch, "E744.0.MirrorCS", {"start": v(40.91, -22.75) * mm, "mid": v(40.99, -22.57) * mm, "end": v(41.16, -22.5) * mm});
            skLineSegment(sketch, "E745.0.MirrorCS", {"start": v(41.16, -22.5) * mm, "end": v(42.21, -22.5) * mm});
            skArc(sketch, "E746.0.MirrorCS", {"start": v(42.21, -22.5) * mm, "mid": v(42.57, -22.64) * mm, "end": v(42.71, -23) * mm});
            skLineSegment(sketch, "E747.0.MirrorCS", {"start": v(42.71, -23) * mm, "end": v(42.71, -28.5) * mm});
            skArc(sketch, "E748.0.MirrorCS", {"start": v(42.71, -28.5) * mm, "mid": v(42.27, -29.56) * mm, "end": v(41.21, -30) * mm});
            skLineSegment(sketch, "E749.0.MirrorCS", {"start": v(41.21, -30) * mm, "end": v(35.71, -30) * mm});
            skArc(sketch, "E750.0.MirrorCS", {"start": v(35.71, -30) * mm, "mid": v(35.36, -29.85) * mm, "end": v(35.21, -29.5) * mm});
            skLineSegment(sketch, "E751.0.MirrorCS", {"start": v(35.21, -29.5) * mm, "end": v(35.21, -28.45) * mm});
            skArc(sketch, "E752.0.MirrorCS", {"start": v(35.21, -28.45) * mm, "mid": v(35.29, -28.27) * mm, "end": v(35.46, -28.2) * mm});
            skLineSegment(sketch, "E753.0.MirrorCS", {"start": v(35.46, -28.2) * mm, "end": v(37.16, -28.2) * mm});
            skArc(sketch, "E754.0.MirrorCS", {"start": v(37.16, -28.2) * mm, "mid": v(38.17, -27.52) * mm, "end": v(37.94, -26.32) * mm});
            skLineSegment(sketch, "E755.0.MirrorCS", {"start": v(37.94, -26.32) * mm, "end": v(35.65, -24.04) * mm});
            skArc(sketch, "E756.0.MirrorCS", {"start": v(35.65, -24.04) * mm, "mid": v(35.17, -23.71) * mm, "end": v(34.6, -23.6) * mm});
            skLineSegment(sketch, "E757.0.MirrorCS", {"start": v(34.6, -23.6) * mm, "end": v(30.84, -23.6) * mm});
            skArc(sketch, "E758.0.MirrorCS", {"start": v(30.84, -23.6) * mm, "mid": v(30.26, -23.71) * mm, "end": v(29.77, -24.04) * mm});
            skLineSegment(sketch, "E759.0.MirrorCS", {"start": v(29.77, -24.04) * mm, "end": v(27.5, -26.32) * mm});
            skArc(sketch, "E760.0.MirrorCS", {"start": v(27.5, -26.32) * mm, "mid": v(27.25, -27.52) * mm, "end": v(28.27, -28.2) * mm});
            skLineSegment(sketch, "E761.0.MirrorCS", {"start": v(28.27, -28.2) * mm, "end": v(29.96, -28.2) * mm});
            skArc(sketch, "E762.0.MirrorCS", {"start": v(29.96, -28.2) * mm, "mid": v(30.14, -28.27) * mm, "end": v(30.21, -28.45) * mm});
            skLineSegment(sketch, "E763.0.MirrorCS", {"start": v(30.21, -28.45) * mm, "end": v(30.21, -29.5) * mm});
            skArc(sketch, "E764.0.MirrorCS", {"start": v(30.21, -29.5) * mm, "mid": v(30.07, -29.85) * mm, "end": v(29.71, -30) * mm});
            skCircle(sketch, "E765.0.MirrorC", {"center": v(32.71, 0) * mm, "radius": 2.15 * mm});
            skCircle(sketch, "E766.0.MirrorC", {"center": v(32.71, -20) * mm, "radius": 2.15 * mm});
            skArc(sketch, "E767.0.MirrorCS", {"start": v(21.57, 7.76) * mm, "mid": v(22.06, 8.09) * mm, "end": v(22.64, 8.2) * mm});
            skLineSegment(sketch, "E768.0.MirrorCS", {"start": v(22.64, 8.2) * mm, "end": v(22.8, 8.2) * mm});
            skArc(sketch, "E769.0.MirrorCS", {"start": v(22.8, 8.2) * mm, "mid": v(23.37, 8.09) * mm, "end": v(23.85, 7.76) * mm});
            skLineSegment(sketch, "E770.0.MirrorCS", {"start": v(23.85, 7.76) * mm, "end": v(28.67, 2.94) * mm});
            skArc(sketch, "E771.0.MirrorCS", {"start": v(28.67, 2.94) * mm, "mid": v(29, 2.45) * mm, "end": v(29.11, 1.88) * mm});
            skLineSegment(sketch, "E772.0.MirrorCS", {"start": v(29.11, 1.88) * mm, "end": v(29.11, -1.88) * mm});
            skArc(sketch, "E773.0.MirrorCS", {"start": v(22.64, -28.2) * mm, "mid": v(22.06, -28.08) * mm, "end": v(21.57, -27.76) * mm});
            skLineSegment(sketch, "E774.0.MirrorCS", {"start": v(22.8, -28.2) * mm, "end": v(22.64, -28.2) * mm});
            skArc(sketch, "E775.0.MirrorCS", {"start": v(23.85, -27.76) * mm, "mid": v(23.37, -28.08) * mm, "end": v(22.8, -28.2) * mm});
            skLineSegment(sketch, "E776.0.MirrorCS", {"start": v(28.67, -22.94) * mm, "end": v(23.85, -27.76) * mm});
            skArc(sketch, "E777.0.MirrorCS", {"start": v(29.11, -21.88) * mm, "mid": v(29, -22.45) * mm, "end": v(28.67, -22.94) * mm});
            skLineSegment(sketch, "E778.0.MirrorCS", {"start": v(29.11, -18.12) * mm, "end": v(29.11, -21.88) * mm});
            skLineSegment(sketch, "E779.0.MirrorCS", {"start": v(30.84, -3.6) * mm, "end": v(34.6, -3.6) * mm});
            skArc(sketch, "E780.0.MirrorCS", {"start": v(34.6, -3.6) * mm, "mid": v(35.17, -3.71) * mm, "end": v(35.65, -4.04) * mm});
            skLineSegment(sketch, "E781.0.MirrorCS", {"start": v(35.65, -4.04) * mm, "end": v(40.47, -8.86) * mm});
            skArc(sketch, "E782.0.MirrorCS", {"start": v(40.47, -8.86) * mm, "mid": v(40.8, -9.35) * mm, "end": v(40.91, -9.92) * mm});
            skLineSegment(sketch, "E783.0.MirrorCS", {"start": v(40.91, -9.92) * mm, "end": v(40.91, -10.08) * mm});
            skArc(sketch, "E784.0.MirrorCS", {"start": v(40.91, -10.08) * mm, "mid": v(40.8, -10.65) * mm, "end": v(40.47, -11.14) * mm});
            skLineSegment(sketch, "E785.0.MirrorCS", {"start": v(40.47, -11.14) * mm, "end": v(35.65, -15.96) * mm});
            skArc(sketch, "E786.0.MirrorCS", {"start": v(35.65, -15.96) * mm, "mid": v(35.17, -16.28) * mm, "end": v(34.6, -16.4) * mm});
            skLineSegment(sketch, "E787.0.MirrorCS", {"start": v(34.6, -16.4) * mm, "end": v(30.84, -16.4) * mm});
            skLineSegment(sketch, "E788.0.MirrorCS", {"start": v(23.85, -7.76) * mm, "end": v(28.67, -2.94) * mm});
            skLineSegment(sketch, "E789.0.MirrorCS", {"start": v(16.75, -2.94) * mm, "end": v(21.57, -7.76) * mm});
            skArc(sketch, "E790.0.MirrorCS", {"start": v(23.85, -7.76) * mm, "mid": v(23.37, -8.08) * mm, "end": v(22.8, -8.2) * mm});
            skArc(sketch, "E791.0.MirrorCS", {"start": v(22.64, -8.2) * mm, "mid": v(22.06, -8.08) * mm, "end": v(21.57, -7.76) * mm});
            skLineSegment(sketch, "E792.0.MirrorCS", {"start": v(22.64, -8.2) * mm, "end": v(22.8, -8.2) * mm});
            skArc(sketch, "E793.0.MirrorCS", {"start": v(29.11, -1.88) * mm, "mid": v(29, -2.45) * mm, "end": v(28.67, -2.94) * mm});
            skLineSegment(sketch, "E794.0.MirrorCS", {"start": v(16.75, -17.06) * mm, "end": v(21.57, -12.24) * mm});
            skLineSegment(sketch, "E795.0.MirrorCS", {"start": v(23.85, -12.24) * mm, "end": v(28.67, -17.06) * mm});
            skArc(sketch, "E796.0.MirrorCS", {"start": v(29.11, -18.12) * mm, "mid": v(29, -17.55) * mm, "end": v(28.67, -17.06) * mm});
            skArc(sketch, "E797.0.MirrorCS", {"start": v(22.64, -11.8) * mm, "mid": v(22.06, -11.91) * mm, "end": v(21.57, -12.24) * mm});
            skArc(sketch, "E798.0.MirrorCS", {"start": v(23.85, -12.24) * mm, "mid": v(23.37, -11.91) * mm, "end": v(22.8, -11.8) * mm});
            skLineSegment(sketch, "E799.0.MirrorCS", {"start": v(22.64, -11.8) * mm, "end": v(22.8, -11.8) * mm});
            skLineSegment(sketch, "E800", {"start": v(32.71, 13.24) * mm, "end": v(32.71, -32.64) * mm, "construction": true});
            skArc(sketch, "E801.0.MirrorCS", {"start": v(30.84, -3.6) * mm, "mid": v(30.26, -3.71) * mm, "end": v(29.77, -4.04) * mm});
            skLineSegment(sketch, "E802.0.MirrorCS", {"start": v(29.77, -4.04) * mm, "end": v(24.95, -8.86) * mm});
            skArc(sketch, "E803.0.MirrorCS", {"start": v(24.95, -8.86) * mm, "mid": v(24.63, -9.35) * mm, "end": v(24.51, -9.92) * mm});
            skLineSegment(sketch, "E804.0.MirrorCS", {"start": v(24.51, -9.92) * mm, "end": v(24.51, -10.08) * mm});
            skArc(sketch, "E805.0.MirrorCS", {"start": v(24.51, -10.08) * mm, "mid": v(24.63, -10.65) * mm, "end": v(24.95, -11.14) * mm});
            skLineSegment(sketch, "E806.0.MirrorCS", {"start": v(24.95, -11.14) * mm, "end": v(29.77, -15.96) * mm});
            skArc(sketch, "E807.0.MirrorCS", {"start": v(29.77, -15.96) * mm, "mid": v(30.26, -16.28) * mm, "end": v(30.84, -16.4) * mm});
            skSolve(sketch);
        }
        {
            var Q0;
            Q0=qSketchRegion(id+"F1",true);
            extrude(context, id + "F8", {"entities" : qUnion([Q0]), "depth" : 500 * mm});
        }
        {
            var Q0;
            Q0=qSketchRegion(id+"F2",true);
            extrude(context, id + "F9", {"entities" : qUnion([Q0]), "depth" : 450 * mm});
        }
        {
            var Q0;
            Q0=qSketchRegion(id+"F3",true);
            extrude(context, id + "F10", {"entities" : qUnion([Q0]), "depth" : 400 * mm});
        }
        {
            var Q0;
            Q0=qSketchRegion(id+"F4",true);
            extrude(context, id + "F11", {"entities" : qUnion([Q0]), "depth" : 350 * mm});
        }
        {
            var Q0;
            Q0=qSketchRegion(id+"F5",true);
            extrude(context, id + "F12", {"entities" : qUnion([Q0]), "depth" : 300 * mm});
        }
        {
            var Q0;
            Q0=qSketchRegion(id+"F6",true);
            extrude(context, id + "F13", {"entities" : qUnion([Q0]), "depth" : 250 * mm});
        }
        {
            var Q0;
            Q0=qSketchRegion(id+"F7",true);
            extrude(context, id + "F14", {"entities" : qUnion([Q0]), "depth" : 200 * mm});
        }
    });
